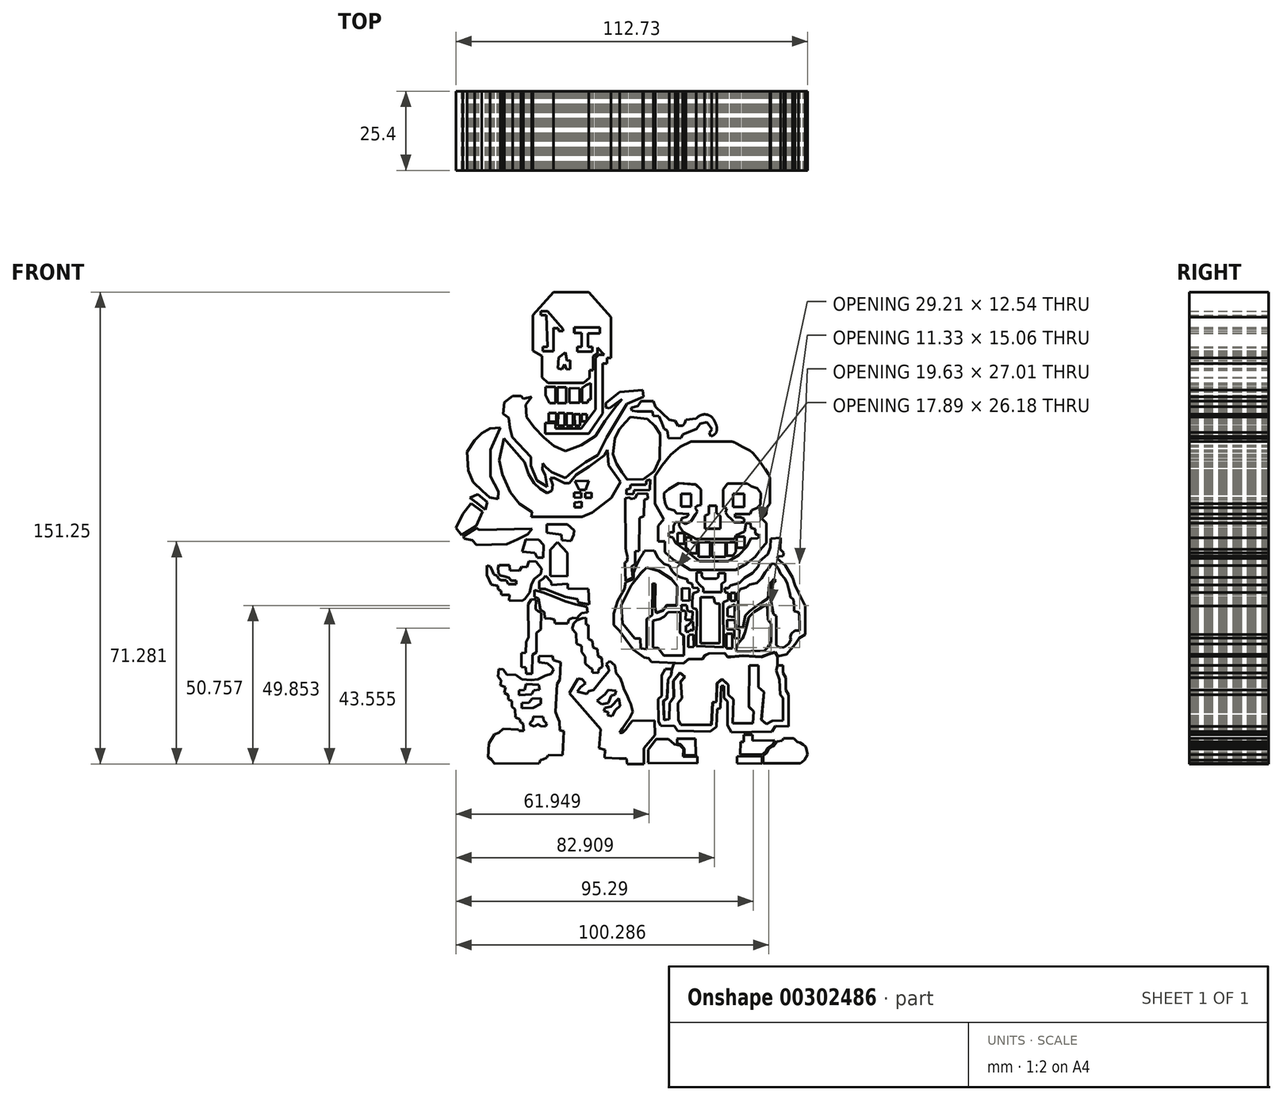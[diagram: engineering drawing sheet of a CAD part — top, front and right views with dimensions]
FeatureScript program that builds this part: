
annotation { "Feature Type Name" : "Feature", "Feature Type Description" : "" }
export const myFeature = defineFeature(function(context is Context, id is Id, definition is map)
    precondition{}
    {
        {
            var Q0;
            Q0=qCreatedBy(makeId("Front.planeOp"),FACE);
            var sketch = newSketch(context, id + "F0", { "sketchPlane" : qUnion([Q0])});
            skLineSegment(sketch, "E0", {"start": v(-16.69, 75) * mm, "end": v(-28, 75) * mm});
            skLineSegment(sketch, "E1", {"start": v(-28, 75) * mm, "end": v(-34.64, 67.58) * mm});
            skLineSegment(sketch, "E2", {"start": v(-34.64, 67.58) * mm, "end": v(-34.64, 56.21) * mm});
            skLineSegment(sketch, "E3", {"start": v(-34.64, 56.21) * mm, "end": v(-31.66, 54.56) * mm});
            skLineSegment(sketch, "E4", {"start": v(-31.66, 54.56) * mm, "end": v(-31.66, 47.68) * mm});
            skLineSegment(sketch, "E5", {"start": v(-31.66, 47.68) * mm, "end": v(-29.8, 45.82) * mm});
            skLineSegment(sketch, "E6", {"start": v(-29.8, 45.82) * mm, "end": v(-18.33, 45.82) * mm});
            skLineSegment(sketch, "E7", {"start": v(-18.33, 45.82) * mm, "end": v(-16.52, 47.56) * mm});
            skLineSegment(sketch, "E8", {"start": v(-16.52, 47.56) * mm, "end": v(-16.52, 49.98) * mm});
            skLineSegment(sketch, "E9", {"start": v(-16.52, 49.98) * mm, "end": v(-15.38, 49.98) * mm});
            skLineSegment(sketch, "E10", {"start": v(-15.38, 49.98) * mm, "end": v(-15.38, 54.44) * mm});
            skLineSegment(sketch, "E11", {"start": v(-15.38, 54.44) * mm, "end": v(-14.6, 54.44) * mm});
            skLineSegment(sketch, "E12", {"start": v(-14.6, 54.44) * mm, "end": v(-14.6, 37.31) * mm});
            skLineSegment(sketch, "E13", {"start": v(-14.6, 37.31) * mm, "end": v(-19.11, 31.33) * mm});
            skLineSegment(sketch, "E14", {"start": v(-19.11, 31.33) * mm, "end": v(-27.42, 31.33) * mm});
            skLineSegment(sketch, "E15", {"start": v(-27.42, 31.33) * mm, "end": v(-27.42, 32.99) * mm});
            skLineSegment(sketch, "E16", {"start": v(-27.42, 32.99) * mm, "end": v(-30.74, 32.99) * mm});
            skLineSegment(sketch, "E17", {"start": v(-30.74, 32.99) * mm, "end": v(-30.74, 29.66) * mm});
            skLineSegment(sketch, "E18", {"start": v(-30.74, 29.66) * mm, "end": v(-16.75, 29.66) * mm});
            skLineSegment(sketch, "E19", {"start": v(-16.75, 29.66) * mm, "end": v(-12.34, 36.12) * mm});
            skLineSegment(sketch, "E20", {"start": v(-12.34, 36.12) * mm, "end": v(-12.34, 52.15) * mm});
            skLineSegment(sketch, "E21", {"start": v(-12.34, 52.15) * mm, "end": v(-10.87, 52.15) * mm});
            skLineSegment(sketch, "E22", {"start": v(-10.87, 52.15) * mm, "end": v(-10.87, 53.88) * mm});
            skLineSegment(sketch, "E23", {"start": v(-10.87, 53.88) * mm, "end": v(-9.6, 53.88) * mm});
            skLineSegment(sketch, "E24", {"start": v(-9.6, 53.88) * mm, "end": v(-9.6, 66.91) * mm});
            skLineSegment(sketch, "E25", {"start": v(-9.6, 66.91) * mm, "end": v(-16.69, 75) * mm});
            skLineSegment(sketch, "E26", {"start": v(-29.94, 57.5) * mm, "end": v(-31.48, 57.5) * mm});
            skLineSegment(sketch, "E27", {"start": v(-31.48, 57.5) * mm, "end": v(-31.48, 56.06) * mm});
            skLineSegment(sketch, "E28", {"start": v(-31.48, 56.06) * mm, "end": v(-28.08, 56.06) * mm});
            skLineSegment(sketch, "E29", {"start": v(-28.08, 56.06) * mm, "end": v(-28.08, 63.46) * mm});
            skLineSegment(sketch, "E30", {"start": v(-28.08, 63.46) * mm, "end": v(-26.52, 63.46) * mm});
            skLineSegment(sketch, "E31", {"start": v(-26.52, 63.46) * mm, "end": v(-26.44, 62.47) * mm});
            skLineSegment(sketch, "E32", {"start": v(-26.44, 62.47) * mm, "end": v(-24.97, 62.47) * mm});
            skLineSegment(sketch, "E33", {"start": v(-24.97, 62.47) * mm, "end": v(-24.97, 63.1) * mm});
            skLineSegment(sketch, "E34", {"start": v(-24.97, 63.1) * mm, "end": v(-29.96, 68.9) * mm});
            skLineSegment(sketch, "E35", {"start": v(-29.96, 68.9) * mm, "end": v(-32.1, 68.9) * mm});
            skLineSegment(sketch, "E36", {"start": v(-32.1, 68.9) * mm, "end": v(-32.1, 67.6) * mm});
            skLineSegment(sketch, "E37", {"start": v(-32.1, 67.6) * mm, "end": v(-30.3, 67.6) * mm});
            skLineSegment(sketch, "E38", {"start": v(-30.3, 67.6) * mm, "end": v(-29.94, 57.5) * mm});
            skLineSegment(sketch, "E39", {"start": v(-21.37, 63.41) * mm, "end": v(-21.37, 61.88) * mm});
            skLineSegment(sketch, "E40", {"start": v(-21.37, 61.88) * mm, "end": v(-19.04, 61.88) * mm});
            skLineSegment(sketch, "E41", {"start": v(-19.04, 61.88) * mm, "end": v(-19.04, 57.4) * mm});
            skLineSegment(sketch, "E42", {"start": v(-19.04, 57.4) * mm, "end": v(-20.43, 57.4) * mm});
            skLineSegment(sketch, "E43", {"start": v(-20.43, 57.4) * mm, "end": v(-20.43, 55.93) * mm});
            skLineSegment(sketch, "E44", {"start": v(-20.43, 55.93) * mm, "end": v(-15.62, 55.93) * mm});
            skLineSegment(sketch, "E45", {"start": v(-15.62, 55.93) * mm, "end": v(-15.62, 57.47) * mm});
            skLineSegment(sketch, "E46", {"start": v(-15.62, 57.47) * mm, "end": v(-16.99, 57.47) * mm});
            skLineSegment(sketch, "E47", {"start": v(-16.99, 57.47) * mm, "end": v(-16.99, 61.76) * mm});
            skLineSegment(sketch, "E48", {"start": v(-16.99, 61.76) * mm, "end": v(-13.12, 61.76) * mm});
            skLineSegment(sketch, "E49", {"start": v(-13.12, 61.76) * mm, "end": v(-13.12, 63.61) * mm});
            skLineSegment(sketch, "E50", {"start": v(-13.12, 63.61) * mm, "end": v(-21.37, 63.61) * mm});
            skLineSegment(sketch, "E51", {"start": v(-21.37, 63.61) * mm, "end": v(-21.37, 63.41) * mm});
            skLineSegment(sketch, "E52", {"start": v(-24.17, 55.7) * mm, "end": v(-23.76, 52.96) * mm});
            skLineSegment(sketch, "E53", {"start": v(-23.76, 52.96) * mm, "end": v(-22.73, 53.11) * mm});
            skLineSegment(sketch, "E54", {"start": v(-22.73, 53.11) * mm, "end": v(-22.73, 50.35) * mm});
            skLineSegment(sketch, "E55", {"start": v(-22.73, 50.35) * mm, "end": v(-23.86, 50.22) * mm});
            skLineSegment(sketch, "E56", {"start": v(-23.86, 50.22) * mm, "end": v(-24.5, 51.88) * mm});
            skLineSegment(sketch, "E57", {"start": v(-24.5, 51.88) * mm, "end": v(-25.32, 50.18) * mm});
            skLineSegment(sketch, "E58", {"start": v(-25.32, 50.18) * mm, "end": v(-26.67, 50.56) * mm});
            skLineSegment(sketch, "E59", {"start": v(-26.67, 50.56) * mm, "end": v(-26.33, 54.04) * mm});
            skLineSegment(sketch, "E60", {"start": v(-26.33, 54.04) * mm, "end": v(-24.17, 55.7) * mm});
            skLineSegment(sketch, "E61", {"start": v(-13.91, 57.13) * mm, "end": v(-13.91, 54.9) * mm});
            skLineSegment(sketch, "E62", {"start": v(-13.91, 54.9) * mm, "end": v(-11.83, 54.86) * mm});
            skLineSegment(sketch, "E63", {"start": v(-11.83, 54.86) * mm, "end": v(-13.91, 57.13) * mm});
            skLineSegment(sketch, "E64", {"start": v(-15.38, 54.44) * mm, "end": v(-13.91, 55.31) * mm});
            skLineSegment(sketch, "E65", {"start": v(-13.91, 55.31) * mm, "end": v(-13.91, 54.9) * mm});
            skLineSegment(sketch, "E66", {"start": v(-14.6, 53.9) * mm, "end": v(-13.52, 54.89) * mm});
            skLineSegment(sketch, "E67", {"start": v(-13.52, 54.89) * mm, "end": v(-13.91, 54.9) * mm});
            skLineSegment(sketch, "E68", {"start": v(-30.64, 44.3) * mm, "end": v(-30.64, 41.9) * mm});
            skLineSegment(sketch, "E69", {"start": v(-30.64, 41.9) * mm, "end": v(-29.36, 39.43) * mm});
            skLineSegment(sketch, "E70", {"start": v(-29.36, 39.43) * mm, "end": v(-27.4, 39.43) * mm});
            skLineSegment(sketch, "E71", {"start": v(-27.4, 39.43) * mm, "end": v(-27.4, 44.55) * mm});
            skLineSegment(sketch, "E72", {"start": v(-27.4, 44.55) * mm, "end": v(-30.64, 44.55) * mm});
            skLineSegment(sketch, "E73", {"start": v(-30.64, 44.55) * mm, "end": v(-30.64, 44.3) * mm});
            skLineSegment(sketch, "E74", {"start": v(-26.73, 44.47) * mm, "end": v(-26.73, 39.36) * mm});
            skLineSegment(sketch, "E75", {"start": v(-26.73, 39.36) * mm, "end": v(-23.91, 39.36) * mm});
            skLineSegment(sketch, "E76", {"start": v(-23.91, 39.36) * mm, "end": v(-23.91, 44.44) * mm});
            skLineSegment(sketch, "E77", {"start": v(-23.91, 44.44) * mm, "end": v(-26.73, 44.47) * mm});
            skLineSegment(sketch, "E78", {"start": v(-22.96, 44.18) * mm, "end": v(-22.96, 39.55) * mm});
            skLineSegment(sketch, "E79", {"start": v(-22.96, 39.55) * mm, "end": v(-19.7, 39.55) * mm});
            skLineSegment(sketch, "E80", {"start": v(-19.7, 39.55) * mm, "end": v(-19.7, 44.15) * mm});
            skLineSegment(sketch, "E81", {"start": v(-19.7, 44.15) * mm, "end": v(-22.96, 44.18) * mm});
            skLineSegment(sketch, "E82", {"start": v(-18.87, 44.28) * mm, "end": v(-18.87, 39.55) * mm});
            skLineSegment(sketch, "E83", {"start": v(-18.87, 39.55) * mm, "end": v(-17.17, 39.55) * mm});
            skLineSegment(sketch, "E84", {"start": v(-17.17, 39.55) * mm, "end": v(-16.82, 40.54) * mm});
            skLineSegment(sketch, "E85", {"start": v(-16.82, 40.54) * mm, "end": v(-16.15, 40.54) * mm});
            skLineSegment(sketch, "E86", {"start": v(-16.15, 40.54) * mm, "end": v(-16.15, 45.78) * mm});
            skLineSegment(sketch, "E87", {"start": v(-16.15, 45.78) * mm, "end": v(-17.5, 45.27) * mm});
            skLineSegment(sketch, "E88", {"start": v(-17.5, 45.27) * mm, "end": v(-18.87, 44.28) * mm});
            skLineSegment(sketch, "E89", {"start": v(-29.52, 33.48) * mm, "end": v(-29.52, 36.2) * mm});
            skLineSegment(sketch, "E90", {"start": v(-29.52, 36.2) * mm, "end": v(-27.18, 36.2) * mm});
            skLineSegment(sketch, "E91", {"start": v(-27.18, 36.2) * mm, "end": v(-27.18, 33.48) * mm});
            skLineSegment(sketch, "E92", {"start": v(-27.18, 33.48) * mm, "end": v(-29.52, 33.48) * mm});
            skLineSegment(sketch, "E93", {"start": v(-26.62, 32.2) * mm, "end": v(-24.53, 32.2) * mm});
            skLineSegment(sketch, "E94", {"start": v(-24.53, 32.2) * mm, "end": v(-24.53, 36.2) * mm});
            skLineSegment(sketch, "E95", {"start": v(-24.53, 36.2) * mm, "end": v(-26.54, 36.2) * mm});
            skLineSegment(sketch, "E96", {"start": v(-26.54, 36.2) * mm, "end": v(-26.62, 32.2) * mm});
            skLineSegment(sketch, "E97", {"start": v(-23.9, 32.2) * mm, "end": v(-21.85, 32.2) * mm});
            skLineSegment(sketch, "E98", {"start": v(-21.85, 32.2) * mm, "end": v(-21.85, 36.03) * mm});
            skLineSegment(sketch, "E99", {"start": v(-21.85, 36.03) * mm, "end": v(-23.85, 36.03) * mm});
            skLineSegment(sketch, "E100", {"start": v(-23.85, 36.03) * mm, "end": v(-23.9, 32.2) * mm});
            skLineSegment(sketch, "E101", {"start": v(-21.17, 32.15) * mm, "end": v(-19.55, 32.15) * mm});
            skLineSegment(sketch, "E102", {"start": v(-19.55, 32.15) * mm, "end": v(-19.55, 35.86) * mm});
            skLineSegment(sketch, "E103", {"start": v(-19.55, 35.86) * mm, "end": v(-21.25, 35.86) * mm});
            skLineSegment(sketch, "E104", {"start": v(-21.25, 35.86) * mm, "end": v(-21.17, 32.15) * mm});
            skLineSegment(sketch, "E105", {"start": v(-19.03, 35.57) * mm, "end": v(-19.03, 33.6) * mm});
            skLineSegment(sketch, "E106", {"start": v(-19.03, 33.6) * mm, "end": v(-17.4, 33.6) * mm});
            skLineSegment(sketch, "E107", {"start": v(-17.4, 33.6) * mm, "end": v(-17.4, 35.86) * mm});
            skLineSegment(sketch, "E108", {"start": v(-17.4, 35.86) * mm, "end": v(-19.03, 35.86) * mm});
            skLineSegment(sketch, "E109", {"start": v(-19.03, 35.86) * mm, "end": v(-19.03, 35.57) * mm});
            skLineSegment(sketch, "E110", {"start": v(-35.03, 41.37) * mm, "end": v(-36.94, 38.85) * mm});
            skLineSegment(sketch, "E111", {"start": v(-36.94, 38.85) * mm, "end": v(-36.63, 34.91) * mm});
            skLineSegment(sketch, "E112", {"start": v(-36.63, 34.91) * mm, "end": v(-34.2, 31.65) * mm});
            skLineSegment(sketch, "E113", {"start": v(-34.2, 31.65) * mm, "end": v(-31.08, 28.3) * mm});
            skLineSegment(sketch, "E114", {"start": v(-31.08, 28.3) * mm, "end": v(-27.97, 25.64) * mm});
            skLineSegment(sketch, "E115", {"start": v(-27.97, 25.64) * mm, "end": v(-24.17, 24.05) * mm});
            skLineSegment(sketch, "E116", {"start": v(-24.17, 24.05) * mm, "end": v(-19.15, 25.87) * mm});
            skLineSegment(sketch, "E117", {"start": v(-19.15, 25.87) * mm, "end": v(-14.52, 28.83) * mm});
            skLineSegment(sketch, "E118", {"start": v(-14.52, 28.83) * mm, "end": v(-11.48, 33.7) * mm});
            skLineSegment(sketch, "E119", {"start": v(-11.48, 33.7) * mm, "end": v(-7.76, 38.71) * mm});
            skLineSegment(sketch, "E120", {"start": v(-7.76, 38.71) * mm, "end": v(-6.09, 40.61) * mm});
            skLineSegment(sketch, "E121", {"start": v(-6.09, 40.61) * mm, "end": v(-10.11, 37.72) * mm});
            skLineSegment(sketch, "E122", {"start": v(-10.11, 37.72) * mm, "end": v(-11.33, 38.03) * mm});
            skLineSegment(sketch, "E123", {"start": v(-11.33, 38.03) * mm, "end": v(-11.33, 39.4) * mm});
            skLineSegment(sketch, "E124", {"start": v(-11.33, 39.4) * mm, "end": v(-6.85, 42.97) * mm});
            skLineSegment(sketch, "E125", {"start": v(-6.85, 42.97) * mm, "end": v(0.6, 43.57) * mm});
            skLineSegment(sketch, "E126", {"start": v(0.6, 43.57) * mm, "end": v(0.77, 41.46) * mm});
            skLineSegment(sketch, "E127", {"start": v(0.77, 41.46) * mm, "end": v(-4.5, 39.1) * mm});
            skLineSegment(sketch, "E128", {"start": v(-4.5, 39.1) * mm, "end": v(-10.96, 28.4) * mm});
            skLineSegment(sketch, "E129", {"start": v(-10.96, 28.4) * mm, "end": v(-13.86, 22.7) * mm});
            skLineSegment(sketch, "E130", {"start": v(-13.86, 22.7) * mm, "end": v(-17.73, 20.45) * mm});
            skLineSegment(sketch, "E131", {"start": v(-17.73, 20.45) * mm, "end": v(-21.97, 17.44) * mm});
            skLineSegment(sketch, "E132", {"start": v(-21.97, 17.44) * mm, "end": v(-24.18, 15.4) * mm});
            skLineSegment(sketch, "E133", {"start": v(-24.18, 15.4) * mm, "end": v(-28.69, 17.33) * mm});
            skLineSegment(sketch, "E134", {"start": v(-28.69, 17.33) * mm, "end": v(-30.62, 18.95) * mm});
            skLineSegment(sketch, "E135", {"start": v(-30.62, 18.95) * mm, "end": v(-31.43, 20.08) * mm});
            skLineSegment(sketch, "E136", {"start": v(-31.43, 20.08) * mm, "end": v(-31.55, 18.1) * mm});
            skLineSegment(sketch, "E137", {"start": v(-31.55, 18.1) * mm, "end": v(-30.65, 16.38) * mm});
            skLineSegment(sketch, "E138", {"start": v(-30.65, 16.38) * mm, "end": v(-30.1, 12.59) * mm});
            skLineSegment(sketch, "E139", {"start": v(-30.1, 12.59) * mm, "end": v(-33.36, 14.66) * mm});
            skLineSegment(sketch, "E140", {"start": v(-33.36, 14.66) * mm, "end": v(-35.26, 19.36) * mm});
            skLineSegment(sketch, "E141", {"start": v(-35.26, 19.36) * mm, "end": v(-35.26, 22.16) * mm});
            skLineSegment(sketch, "E142", {"start": v(-35.26, 22.16) * mm, "end": v(-41.3, 28.49) * mm});
            skLineSegment(sketch, "E143", {"start": v(-41.3, 28.49) * mm, "end": v(-42.03, 31.47) * mm});
            skLineSegment(sketch, "E144", {"start": v(-42.03, 31.47) * mm, "end": v(-42.4, 34.72) * mm});
            skLineSegment(sketch, "E145", {"start": v(-42.4, 34.72) * mm, "end": v(-44.2, 35.99) * mm});
            skLineSegment(sketch, "E146", {"start": v(-44.2, 35.99) * mm, "end": v(-43.75, 39.6) * mm});
            skLineSegment(sketch, "E147", {"start": v(-43.75, 39.6) * mm, "end": v(-41.13, 41.68) * mm});
            skLineSegment(sketch, "E148", {"start": v(-41.13, 41.68) * mm, "end": v(-38.42, 41.68) * mm});
            skLineSegment(sketch, "E149", {"start": v(-38.42, 41.68) * mm, "end": v(-37.7, 40.78) * mm});
            skLineSegment(sketch, "E150", {"start": v(-37.7, 40.78) * mm, "end": v(-35.03, 41.37) * mm});
            skLineSegment(sketch, "E151", {"start": v(-3.09, 37.93) * mm, "end": v(-0.94, 38.5) * mm});
            skLineSegment(sketch, "E152", {"start": v(-0.94, 38.5) * mm, "end": v(0, 40.09) * mm});
            skLineSegment(sketch, "E153", {"start": v(0, 40.09) * mm, "end": v(3.94, 40.09) * mm});
            skLineSegment(sketch, "E154", {"start": v(3.94, 40.09) * mm, "end": v(4.66, 38.3) * mm});
            skLineSegment(sketch, "E155", {"start": v(4.66, 38.3) * mm, "end": v(9.1, 34.06) * mm});
            skLineSegment(sketch, "E156", {"start": v(9.1, 34.06) * mm, "end": v(10.9, 33.7) * mm});
            skLineSegment(sketch, "E157", {"start": v(10.9, 33.7) * mm, "end": v(11.83, 32.13) * mm});
            skLineSegment(sketch, "E158", {"start": v(11.83, 32.13) * mm, "end": v(13.4, 32.2) * mm});
            skLineSegment(sketch, "E159", {"start": v(13.4, 32.2) * mm, "end": v(13.98, 32.91) * mm});
            skLineSegment(sketch, "E160", {"start": v(13.98, 32.91) * mm, "end": v(14.4, 34.06) * mm});
            skLineSegment(sketch, "E161", {"start": v(14.4, 34.06) * mm, "end": v(17.64, 34.42) * mm});
            skLineSegment(sketch, "E162", {"start": v(17.64, 34.42) * mm, "end": v(18.5, 35.78) * mm});
            skLineSegment(sketch, "E163", {"start": v(18.5, 35.78) * mm, "end": v(21.72, 35.78) * mm});
            skLineSegment(sketch, "E164", {"start": v(21.72, 35.78) * mm, "end": v(23.09, 34.56) * mm});
            skLineSegment(sketch, "E165", {"start": v(23.09, 34.56) * mm, "end": v(24.02, 32.63) * mm});
            skLineSegment(sketch, "E166", {"start": v(24.02, 32.63) * mm, "end": v(24.6, 30.76) * mm});
            skLineSegment(sketch, "E167", {"start": v(24.6, 30.76) * mm, "end": v(23.66, 29.04) * mm});
            skLineSegment(sketch, "E168", {"start": v(23.66, 29.04) * mm, "end": v(22.44, 28.76) * mm});
            skLineSegment(sketch, "E169", {"start": v(22.44, 28.76) * mm, "end": v(21.87, 29.83) * mm});
            skLineSegment(sketch, "E170", {"start": v(21.87, 29.83) * mm, "end": v(22.73, 31.05) * mm});
            skLineSegment(sketch, "E171", {"start": v(22.73, 31.05) * mm, "end": v(21.15, 33.34) * mm});
            skLineSegment(sketch, "E172", {"start": v(21.15, 33.34) * mm, "end": v(19, 32.77) * mm});
            skLineSegment(sketch, "E173", {"start": v(19, 32.77) * mm, "end": v(17.78, 31.2) * mm});
            skLineSegment(sketch, "E174", {"start": v(17.78, 31.2) * mm, "end": v(15.05, 30.05) * mm});
            skLineSegment(sketch, "E175", {"start": v(15.05, 30.05) * mm, "end": v(13.4, 29.33) * mm});
            skLineSegment(sketch, "E176", {"start": v(13.4, 29.33) * mm, "end": v(12.83, 28.25) * mm});
            skLineSegment(sketch, "E177", {"start": v(12.83, 28.25) * mm, "end": v(8.81, 28.04) * mm});
            skLineSegment(sketch, "E178", {"start": v(8.81, 28.04) * mm, "end": v(8.38, 30.62) * mm});
            skLineSegment(sketch, "E179", {"start": v(8.38, 30.62) * mm, "end": v(7.38, 31.2) * mm});
            skLineSegment(sketch, "E180", {"start": v(7.38, 31.2) * mm, "end": v(6.66, 33.2) * mm});
            skLineSegment(sketch, "E181", {"start": v(6.66, 33.2) * mm, "end": v(5.8, 35.2) * mm});
            skLineSegment(sketch, "E182", {"start": v(5.8, 35.2) * mm, "end": v(3.87, 35.35) * mm});
            skLineSegment(sketch, "E183", {"start": v(3.87, 35.35) * mm, "end": v(3.72, 36.79) * mm});
            skLineSegment(sketch, "E184", {"start": v(3.72, 36.79) * mm, "end": v(-1.22, 36.79) * mm});
            skLineSegment(sketch, "E185", {"start": v(-1.22, 36.79) * mm, "end": v(-2.95, 36.93) * mm});
            skLineSegment(sketch, "E186", {"start": v(-2.95, 36.93) * mm, "end": v(-3.16, 37.8) * mm});
            skLineSegment(sketch, "E187", {"start": v(-3.16, 37.8) * mm, "end": v(-3.09, 37.93) * mm});
            skLineSegment(sketch, "E188", {"start": v(-3.09, 35.2) * mm, "end": v(-5.01, 33.2) * mm});
            skLineSegment(sketch, "E189", {"start": v(-5.01, 33.2) * mm, "end": v(-6.77, 31.12) * mm});
            skLineSegment(sketch, "E190", {"start": v(-6.77, 31.12) * mm, "end": v(-8.4, 28.28) * mm});
            skLineSegment(sketch, "E191", {"start": v(-8.4, 28.28) * mm, "end": v(-8.94, 23) * mm});
            skLineSegment(sketch, "E192", {"start": v(-8.94, 23) * mm, "end": v(-7.85, 20.02) * mm});
            skLineSegment(sketch, "E193", {"start": v(-7.85, 20.02) * mm, "end": v(-6.1, 17.1) * mm});
            skLineSegment(sketch, "E194", {"start": v(-6.1, 17.1) * mm, "end": v(-4.47, 14.87) * mm});
            skLineSegment(sketch, "E195", {"start": v(-4.47, 14.87) * mm, "end": v(0.81, 15.01) * mm});
            skLineSegment(sketch, "E196", {"start": v(0.81, 15.01) * mm, "end": v(4.2, 17.58) * mm});
            skLineSegment(sketch, "E197", {"start": v(4.2, 17.58) * mm, "end": v(5.95, 21.5) * mm});
            skLineSegment(sketch, "E198", {"start": v(5.95, 21.5) * mm, "end": v(6.1, 29.43) * mm});
            skLineSegment(sketch, "E199", {"start": v(6.1, 29.43) * mm, "end": v(4.53, 32.07) * mm});
            skLineSegment(sketch, "E200", {"start": v(4.53, 32.07) * mm, "end": v(2.03, 34.37) * mm});
            skLineSegment(sketch, "E201", {"start": v(2.03, 34.37) * mm, "end": v(-3.38, 34.9) * mm});
            skLineSegment(sketch, "E202", {"start": v(-3.38, 34.9) * mm, "end": v(-5.01, 33.2) * mm});
            skLineSegment(sketch, "E203", {"start": v(-43.86, 28.08) * mm, "end": v(-37.36, 20.49) * mm});
            skLineSegment(sketch, "E204", {"start": v(-37.36, 20.49) * mm, "end": v(-36.1, 16.7) * mm});
            skLineSegment(sketch, "E205", {"start": v(-36.1, 16.7) * mm, "end": v(-34.29, 13.8) * mm});
            skLineSegment(sketch, "E206", {"start": v(-34.29, 13.8) * mm, "end": v(-32.3, 12) * mm});
            skLineSegment(sketch, "E207", {"start": v(-32.3, 12) * mm, "end": v(-30.13, 10.55) * mm});
            skLineSegment(sketch, "E208", {"start": v(-30.13, 10.55) * mm, "end": v(-28.6, 11.27) * mm});
            skLineSegment(sketch, "E209", {"start": v(-28.6, 11.27) * mm, "end": v(-28.32, 13.26) * mm});
            skLineSegment(sketch, "E210", {"start": v(-28.32, 13.26) * mm, "end": v(-29.05, 15.34) * mm});
            skLineSegment(sketch, "E211", {"start": v(-29.05, 15.34) * mm, "end": v(-27.78, 15.34) * mm});
            skLineSegment(sketch, "E212", {"start": v(-27.78, 15.34) * mm, "end": v(-24.53, 13.7) * mm});
            skLineSegment(sketch, "E213", {"start": v(-24.53, 13.7) * mm, "end": v(-23, 13.7) * mm});
            skLineSegment(sketch, "E214", {"start": v(-23, 13.7) * mm, "end": v(-20.82, 16.42) * mm});
            skLineSegment(sketch, "E215", {"start": v(-20.82, 16.42) * mm, "end": v(-16.67, 19.13) * mm});
            skLineSegment(sketch, "E216", {"start": v(-16.67, 19.13) * mm, "end": v(-11.79, 22.65) * mm});
            skLineSegment(sketch, "E217", {"start": v(-11.79, 22.65) * mm, "end": v(-10.8, 24.37) * mm});
            skLineSegment(sketch, "E218", {"start": v(-10.8, 24.37) * mm, "end": v(-10.43, 19.4) * mm});
            skLineSegment(sketch, "E219", {"start": v(-10.43, 19.4) * mm, "end": v(-6.55, 14.16) * mm});
            skLineSegment(sketch, "E220", {"start": v(-6.55, 14.16) * mm, "end": v(-9.53, 9.1) * mm});
            skLineSegment(sketch, "E221", {"start": v(-9.53, 9.1) * mm, "end": v(-15.65, 4.36) * mm});
            skLineSegment(sketch, "E222", {"start": v(-15.65, 4.36) * mm, "end": v(-18.9, 2.9) * mm});
            skLineSegment(sketch, "E223", {"start": v(-18.9, 2.9) * mm, "end": v(-35.1, 2.9) * mm});
            skLineSegment(sketch, "E224", {"start": v(-35.1, 2.9) * mm, "end": v(-34.92, 4.53) * mm});
            skLineSegment(sketch, "E225", {"start": v(-34.92, 4.53) * mm, "end": v(-39.02, 7.09) * mm});
            skLineSegment(sketch, "E226", {"start": v(-39.02, 7.09) * mm, "end": v(-41.92, 10.84) * mm});
            skLineSegment(sketch, "E227", {"start": v(-41.92, 10.84) * mm, "end": v(-44.47, 16.55) * mm});
            skLineSegment(sketch, "E228", {"start": v(-44.47, 16.55) * mm, "end": v(-45.5, 21.07) * mm});
            skLineSegment(sketch, "E229", {"start": v(-45.5, 21.07) * mm, "end": v(-43.86, 28.08) * mm});
            skLineSegment(sketch, "E230", {"start": v(-20.94, 13.9) * mm, "end": v(-19.74, 11.6) * mm});
            skLineSegment(sketch, "E231", {"start": v(-19.74, 11.6) * mm, "end": v(-17.78, 11.6) * mm});
            skLineSegment(sketch, "E232", {"start": v(-17.78, 11.6) * mm, "end": v(-16.67, 14.5) * mm});
            skLineSegment(sketch, "E233", {"start": v(-16.67, 14.5) * mm, "end": v(-21.2, 14.42) * mm});
            skLineSegment(sketch, "E234", {"start": v(-21.2, 14.42) * mm, "end": v(-20.94, 13.9) * mm});
            skLineSegment(sketch, "E235", {"start": v(-21.4, 10.65) * mm, "end": v(-21.4, 9.15) * mm});
            skLineSegment(sketch, "E236", {"start": v(-21.4, 9.15) * mm, "end": v(-19.16, 9) * mm});
            skLineSegment(sketch, "E237", {"start": v(-19.16, 9) * mm, "end": v(-19.16, 10.65) * mm});
            skLineSegment(sketch, "E238", {"start": v(-19.16, 10.65) * mm, "end": v(-21.4, 10.65) * mm});
            skLineSegment(sketch, "E239", {"start": v(-17.82, 10.59) * mm, "end": v(-17.82, 9.05) * mm});
            skLineSegment(sketch, "E240", {"start": v(-17.82, 9.05) * mm, "end": v(-15.9, 9.05) * mm});
            skLineSegment(sketch, "E241", {"start": v(-15.9, 9.05) * mm, "end": v(-15.9, 10.65) * mm});
            skLineSegment(sketch, "E242", {"start": v(-15.9, 10.65) * mm, "end": v(-17.82, 10.59) * mm});
            skLineSegment(sketch, "E243", {"start": v(-21.27, 7.52) * mm, "end": v(-21.27, 5.96) * mm});
            skLineSegment(sketch, "E244", {"start": v(-21.27, 5.96) * mm, "end": v(-18.97, 5.96) * mm});
            skLineSegment(sketch, "E245", {"start": v(-18.97, 5.96) * mm, "end": v(-18.97, 7.71) * mm});
            skLineSegment(sketch, "E246", {"start": v(-18.97, 7.71) * mm, "end": v(-21.27, 7.52) * mm});
            skLineSegment(sketch, "E247", {"start": v(-45.15, 31.32) * mm, "end": v(-48.21, 24.4) * mm});
            skLineSegment(sketch, "E248", {"start": v(-48.21, 24.4) * mm, "end": v(-48.21, 15.87) * mm});
            skLineSegment(sketch, "E249", {"start": v(-48.21, 15.87) * mm, "end": v(-45.64, 11.04) * mm});
            skLineSegment(sketch, "E250", {"start": v(-45.64, 11.04) * mm, "end": v(-45.8, 8.63) * mm});
            skLineSegment(sketch, "E251", {"start": v(-45.8, 8.63) * mm, "end": v(-48.53, 9.1) * mm});
            skLineSegment(sketch, "E252", {"start": v(-48.53, 9.1) * mm, "end": v(-50.79, 11.2) * mm});
            skLineSegment(sketch, "E253", {"start": v(-50.79, 11.2) * mm, "end": v(-53.85, 14.1) * mm});
            skLineSegment(sketch, "E254", {"start": v(-53.85, 14.1) * mm, "end": v(-55.38, 17.8) * mm});
            skLineSegment(sketch, "E255", {"start": v(-55.38, 17.8) * mm, "end": v(-55.7, 23.76) * mm});
            skLineSegment(sketch, "E256", {"start": v(-55.7, 23.76) * mm, "end": v(-53.35, 27.5) * mm});
            skLineSegment(sketch, "E257", {"start": v(-53.35, 27.5) * mm, "end": v(-50.97, 29.74) * mm});
            skLineSegment(sketch, "E258", {"start": v(-50.97, 29.74) * mm, "end": v(-48.4, 31.3) * mm});
            skLineSegment(sketch, "E259", {"start": v(-48.4, 31.3) * mm, "end": v(-45, 31.49) * mm});
            skLineSegment(sketch, "E260", {"start": v(-45, 31.49) * mm, "end": v(-45.15, 31.32) * mm});
            skLineSegment(sketch, "E261", {"start": v(-54.84, 9.08) * mm, "end": v(-52.57, 7.43) * mm});
            skLineSegment(sketch, "E262", {"start": v(-52.57, 7.43) * mm, "end": v(-49.9, 5.21) * mm});
            skLineSegment(sketch, "E263", {"start": v(-49.9, 5.21) * mm, "end": v(-49.27, 7.6) * mm});
            skLineSegment(sketch, "E264", {"start": v(-49.27, 7.6) * mm, "end": v(-52.34, 10.17) * mm});
            skLineSegment(sketch, "E265", {"start": v(-52.34, 10.17) * mm, "end": v(-54.84, 9.08) * mm});
            skLineSegment(sketch, "E266", {"start": v(-54.44, 7.23) * mm, "end": v(-50.8, 4.6) * mm});
            skLineSegment(sketch, "E267", {"start": v(-50.8, 4.6) * mm, "end": v(-52.83, 0) * mm});
            skLineSegment(sketch, "E268", {"start": v(-52.83, 0) * mm, "end": v(-57.45, -2.87) * mm});
            skLineSegment(sketch, "E269", {"start": v(-57.45, -2.87) * mm, "end": v(-59.33, -0.67) * mm});
            skLineSegment(sketch, "E270", {"start": v(-59.33, -0.67) * mm, "end": v(-57.13, 3.8) * mm});
            skLineSegment(sketch, "E271", {"start": v(-57.13, 3.8) * mm, "end": v(-54.44, 7.23) * mm});
            skLineSegment(sketch, "E272", {"start": v(-56.92, -3.3) * mm, "end": v(-52.62, -0.61) * mm});
            skLineSegment(sketch, "E273", {"start": v(-52.62, -0.61) * mm, "end": v(-51.87, -1.26) * mm});
            skLineSegment(sketch, "E274", {"start": v(-51.87, -1.26) * mm, "end": v(-34.89, -0.83) * mm});
            skLineSegment(sketch, "E275", {"start": v(-34.89, -0.83) * mm, "end": v(-36.23, -2.66) * mm});
            skLineSegment(sketch, "E276", {"start": v(-36.23, -2.66) * mm, "end": v(-39.56, -4.27) * mm});
            skLineSegment(sketch, "E277", {"start": v(-39.56, -4.27) * mm, "end": v(-43.05, -5.88) * mm});
            skLineSegment(sketch, "E278", {"start": v(-43.05, -5.88) * mm, "end": v(-52.62, -6.1) * mm});
            skLineSegment(sketch, "E279", {"start": v(-52.62, -6.1) * mm, "end": v(-54.07, -4.48) * mm});
            skLineSegment(sketch, "E280", {"start": v(-54.07, -4.48) * mm, "end": v(-56.65, -4.05) * mm});
            skLineSegment(sketch, "E281", {"start": v(-56.65, -4.05) * mm, "end": v(-56.92, -3.3) * mm});
            skLineSegment(sketch, "E282", {"start": v(-36.96, -4.31) * mm, "end": v(-38, -8.25) * mm});
            skLineSegment(sketch, "E283", {"start": v(-38, -8.25) * mm, "end": v(-33.98, -8.58) * mm});
            skLineSegment(sketch, "E284", {"start": v(-33.98, -8.58) * mm, "end": v(-33.26, -10.19) * mm});
            skLineSegment(sketch, "E285", {"start": v(-33.26, -10.19) * mm, "end": v(-31.33, -10.19) * mm});
            skLineSegment(sketch, "E286", {"start": v(-31.33, -10.19) * mm, "end": v(-31.25, -6.08) * mm});
            skLineSegment(sketch, "E287", {"start": v(-31.25, -6.08) * mm, "end": v(-32.7, -4.47) * mm});
            skLineSegment(sketch, "E288", {"start": v(-32.7, -4.47) * mm, "end": v(-36.8, -4.31) * mm});
            skLineSegment(sketch, "E289", {"start": v(-36.8, -4.31) * mm, "end": v(-36.96, -4.31) * mm});
            skLineSegment(sketch, "E290", {"start": v(-30.2, 0.54) * mm, "end": v(-30.2, -2.15) * mm});
            skLineSegment(sketch, "E291", {"start": v(-30.2, -2.15) * mm, "end": v(-25.53, -2.8) * mm});
            skLineSegment(sketch, "E292", {"start": v(-25.53, -2.8) * mm, "end": v(-25.38, -4.58) * mm});
            skLineSegment(sketch, "E293", {"start": v(-25.38, -4.58) * mm, "end": v(-22.49, -4.79) * mm});
            skLineSegment(sketch, "E294", {"start": v(-22.49, -4.79) * mm, "end": v(-21.52, -2.76) * mm});
            skLineSegment(sketch, "E295", {"start": v(-21.52, -2.76) * mm, "end": v(-21.37, -1.39) * mm});
            skLineSegment(sketch, "E296", {"start": v(-21.37, -1.39) * mm, "end": v(-23.6, 0.49) * mm});
            skLineSegment(sketch, "E297", {"start": v(-23.6, 0.49) * mm, "end": v(-30.2, 0.54) * mm});
            skLineSegment(sketch, "E298", {"start": v(-29, -7.43) * mm, "end": v(-29, -15.95) * mm});
            skLineSegment(sketch, "E299", {"start": v(-29, -15.95) * mm, "end": v(-23.65, -16.05) * mm});
            skLineSegment(sketch, "E300", {"start": v(-23.65, -16.05) * mm, "end": v(-23.55, -8.58) * mm});
            skLineSegment(sketch, "E301", {"start": v(-23.55, -8.58) * mm, "end": v(-26.71, -5.23) * mm});
            skLineSegment(sketch, "E302", {"start": v(-26.71, -5.23) * mm, "end": v(-28.91, -7.43) * mm});
            skLineSegment(sketch, "E303", {"start": v(-28.91, -7.43) * mm, "end": v(-29, -7.43) * mm});
            skLineSegment(sketch, "E304", {"start": v(-44.86, -17.4) * mm, "end": v(-43.1, -17.4) * mm});
            skLineSegment(sketch, "E305", {"start": v(-43.1, -17.4) * mm, "end": v(-42.56, -18.68) * mm});
            skLineSegment(sketch, "E306", {"start": v(-42.56, -18.68) * mm, "end": v(-39.92, -18.61) * mm});
            skLineSegment(sketch, "E307", {"start": v(-39.92, -18.61) * mm, "end": v(-39.98, -17.53) * mm});
            skLineSegment(sketch, "E308", {"start": v(-39.98, -17.53) * mm, "end": v(-41.6, -17.46) * mm});
            skLineSegment(sketch, "E309", {"start": v(-41.6, -17.46) * mm, "end": v(-42.28, -16.58) * mm});
            skLineSegment(sketch, "E310", {"start": v(-42.28, -16.58) * mm, "end": v(-43.37, -16.18) * mm});
            skLineSegment(sketch, "E311", {"start": v(-43.37, -16.18) * mm, "end": v(-45, -15.9) * mm});
            skLineSegment(sketch, "E312", {"start": v(-45.4, -12.59) * mm, "end": v(-42.08, -12.59) * mm});
            skLineSegment(sketch, "E313", {"start": v(-42.08, -12.59) * mm, "end": v(-42.01, -14.21) * mm});
            skLineSegment(sketch, "E314", {"start": v(-42.01, -14.21) * mm, "end": v(-38.9, -14.35) * mm});
            skLineSegment(sketch, "E315", {"start": v(-38.9, -14.35) * mm, "end": v(-38.16, -13.06) * mm});
            skLineSegment(sketch, "E316", {"start": v(-38.16, -13.06) * mm, "end": v(-36.53, -13.13) * mm});
            skLineSegment(sketch, "E317", {"start": v(-36.53, -13.13) * mm, "end": v(-35.92, -11.3) * mm});
            skLineSegment(sketch, "E318", {"start": v(-35.92, -11.3) * mm, "end": v(-33.62, -11.37) * mm});
            skLineSegment(sketch, "E319", {"start": v(-33.62, -11.37) * mm, "end": v(-31.86, -13.67) * mm});
            skLineSegment(sketch, "E320", {"start": v(-31.86, -13.67) * mm, "end": v(-32.13, -15.3) * mm});
            skLineSegment(sketch, "E321", {"start": v(-32.13, -15.3) * mm, "end": v(-34.3, -16.99) * mm});
            skLineSegment(sketch, "E322", {"start": v(-34.3, -16.99) * mm, "end": v(-35.1, -18.95) * mm});
            skLineSegment(sketch, "E323", {"start": v(-35.1, -18.95) * mm, "end": v(-35.72, -21.25) * mm});
            skLineSegment(sketch, "E324", {"start": v(-35.72, -21.25) * mm, "end": v(-37.2, -23.28) * mm});
            skLineSegment(sketch, "E325", {"start": v(-37.2, -23.28) * mm, "end": v(-38.09, -24.03) * mm});
            skLineSegment(sketch, "E326", {"start": v(-38.09, -24.03) * mm, "end": v(-42.28, -23.82) * mm});
            skLineSegment(sketch, "E327", {"start": v(-42.28, -23.82) * mm, "end": v(-42.15, -22.06) * mm});
            skLineSegment(sketch, "E328", {"start": v(-42.15, -22.06) * mm, "end": v(-44.65, -22.06) * mm});
            skLineSegment(sketch, "E329", {"start": v(-44.65, -22.06) * mm, "end": v(-44.98, -20.62) * mm});
            skLineSegment(sketch, "E330", {"start": v(-44.98, -20.62) * mm, "end": v(-45.67, -20.37) * mm});
            skLineSegment(sketch, "E331", {"start": v(-45.67, -20.37) * mm, "end": v(-46, -19.16) * mm});
            skLineSegment(sketch, "E332", {"start": v(-46, -19.16) * mm, "end": v(-47.97, -18.75) * mm});
            skLineSegment(sketch, "E333", {"start": v(-47.97, -18.75) * mm, "end": v(-49.36, -15.76) * mm});
            skLineSegment(sketch, "E334", {"start": v(-32.67, -19.63) * mm, "end": v(-32.67, -17.7) * mm});
            skLineSegment(sketch, "E335", {"start": v(-32.67, -17.7) * mm, "end": v(-31.35, -16.85) * mm});
            skLineSegment(sketch, "E336", {"start": v(-31.35, -16.85) * mm, "end": v(-30.62, -16.01) * mm});
            skLineSegment(sketch, "E337", {"start": v(-30.62, -16.01) * mm, "end": v(-28.81, -17.82) * mm});
            skLineSegment(sketch, "E338", {"start": v(-28.81, -17.82) * mm, "end": v(-28.7, -18.9) * mm});
            skLineSegment(sketch, "E339", {"start": v(-28.7, -18.9) * mm, "end": v(-23.45, -18.48) * mm});
            skLineSegment(sketch, "E340", {"start": v(-23.45, -18.48) * mm, "end": v(-23.45, -20.05) * mm});
            skLineSegment(sketch, "E341", {"start": v(-23.45, -20.05) * mm, "end": v(-16.81, -20.11) * mm});
            skLineSegment(sketch, "E342", {"start": v(-16.81, -20.11) * mm, "end": v(-16.63, -25.12) * mm});
            skLineSegment(sketch, "E343", {"start": v(-16.63, -25.12) * mm, "end": v(-20.13, -24.51) * mm});
            skLineSegment(sketch, "E344", {"start": v(-20.13, -24.51) * mm, "end": v(-20.25, -23.43) * mm});
            skLineSegment(sketch, "E345", {"start": v(-20.25, -23.43) * mm, "end": v(-24.23, -22.7) * mm});
            skLineSegment(sketch, "E346", {"start": v(-24.23, -22.7) * mm, "end": v(-28.51, -21.02) * mm});
            skLineSegment(sketch, "E347", {"start": v(-28.51, -21.02) * mm, "end": v(-30.74, -20.11) * mm});
            skLineSegment(sketch, "E348", {"start": v(-30.74, -20.11) * mm, "end": v(-32.59, -20.17) * mm});
            skLineSegment(sketch, "E349", {"start": v(-32.59, -20.17) * mm, "end": v(-32.67, -19.63) * mm});
            skLineSegment(sketch, "E350", {"start": v(-34.08, -20.51) * mm, "end": v(-34.08, -22.75) * mm});
            skLineSegment(sketch, "E351", {"start": v(-34.08, -22.75) * mm, "end": v(-32.83, -23.2) * mm});
            skLineSegment(sketch, "E352", {"start": v(-32.83, -23.2) * mm, "end": v(-32.29, -26.77) * mm});
            skLineSegment(sketch, "E353", {"start": v(-32.29, -26.77) * mm, "end": v(-30.98, -27.6) * mm});
            skLineSegment(sketch, "E354", {"start": v(-30.98, -27.6) * mm, "end": v(-30.79, -29.52) * mm});
            skLineSegment(sketch, "E355", {"start": v(-30.79, -29.52) * mm, "end": v(-28.9, -29.65) * mm});
            skLineSegment(sketch, "E356", {"start": v(-28.9, -29.65) * mm, "end": v(-27.85, -30) * mm});
            skLineSegment(sketch, "E357", {"start": v(-27.85, -30) * mm, "end": v(-27.53, -31.18) * mm});
            skLineSegment(sketch, "E358", {"start": v(-27.53, -31.18) * mm, "end": v(-23.44, -31.24) * mm});
            skLineSegment(sketch, "E359", {"start": v(-23.44, -31.24) * mm, "end": v(-23.02, -29.9) * mm});
            skLineSegment(sketch, "E360", {"start": v(-23.02, -29.9) * mm, "end": v(-21.78, -29.49) * mm});
            skLineSegment(sketch, "E361", {"start": v(-21.78, -29.49) * mm, "end": v(-20.6, -29.58) * mm});
            skLineSegment(sketch, "E362", {"start": v(-20.6, -29.58) * mm, "end": v(-19.73, -28.69) * mm});
            skLineSegment(sketch, "E363", {"start": v(-19.73, -28.69) * mm, "end": v(-19, -27.92) * mm});
            skLineSegment(sketch, "E364", {"start": v(-19, -27.92) * mm, "end": v(-17.18, -27.6) * mm});
            skLineSegment(sketch, "E365", {"start": v(-17.18, -27.6) * mm, "end": v(-17.37, -25.88) * mm});
            skLineSegment(sketch, "E366", {"start": v(-17.37, -25.88) * mm, "end": v(-20.95, -25.15) * mm});
            skLineSegment(sketch, "E367", {"start": v(-20.95, -25.15) * mm, "end": v(-24.4, -24.16) * mm});
            skLineSegment(sketch, "E368", {"start": v(-24.4, -24.16) * mm, "end": v(-27.4, -22.89) * mm});
            skLineSegment(sketch, "E369", {"start": v(-27.4, -22.89) * mm, "end": v(-31.3, -21.26) * mm});
            skLineSegment(sketch, "E370", {"start": v(-31.3, -21.26) * mm, "end": v(-34.08, -20.51) * mm});
            skLineSegment(sketch, "E371", {"start": v(-35.14, -23.44) * mm, "end": v(-33.6, -23.65) * mm});
            skLineSegment(sketch, "E372", {"start": v(-33.6, -23.65) * mm, "end": v(-33.72, -26.62) * mm});
            skLineSegment(sketch, "E373", {"start": v(-33.72, -26.62) * mm, "end": v(-33.05, -27.31) * mm});
            skLineSegment(sketch, "E374", {"start": v(-33.05, -27.31) * mm, "end": v(-31.98, -27.74) * mm});
            skLineSegment(sketch, "E375", {"start": v(-31.98, -27.74) * mm, "end": v(-32.08, -33.15) * mm});
            skLineSegment(sketch, "E376", {"start": v(-32.08, -33.15) * mm, "end": v(-33.44, -34.33) * mm});
            skLineSegment(sketch, "E377", {"start": v(-33.44, -34.33) * mm, "end": v(-33.44, -40.42) * mm});
            skLineSegment(sketch, "E378", {"start": v(-33.44, -40.42) * mm, "end": v(-34.8, -41.19) * mm});
            skLineSegment(sketch, "E379", {"start": v(-34.8, -41.19) * mm, "end": v(-34.95, -47.34) * mm});
            skLineSegment(sketch, "E380", {"start": v(-34.95, -47.34) * mm, "end": v(-36.81, -47.3) * mm});
            skLineSegment(sketch, "E381", {"start": v(-36.81, -47.3) * mm, "end": v(-36.89, -45.33) * mm});
            skLineSegment(sketch, "E382", {"start": v(-36.89, -45.33) * mm, "end": v(-38.3, -45.18) * mm});
            skLineSegment(sketch, "E383", {"start": v(-38.3, -45.18) * mm, "end": v(-38.33, -40.7) * mm});
            skLineSegment(sketch, "E384", {"start": v(-38.33, -40.7) * mm, "end": v(-36.96, -40.58) * mm});
            skLineSegment(sketch, "E385", {"start": v(-36.96, -40.58) * mm, "end": v(-36.85, -37.16) * mm});
            skLineSegment(sketch, "E386", {"start": v(-36.85, -37.16) * mm, "end": v(-36.1, -35.68) * mm});
            skLineSegment(sketch, "E387", {"start": v(-36.1, -35.68) * mm, "end": v(-36.13, -25.16) * mm});
            skLineSegment(sketch, "E388", {"start": v(-36.13, -25.16) * mm, "end": v(-35.14, -23.44) * mm});
            skLineSegment(sketch, "E389", {"start": v(-20.58, -30.2) * mm, "end": v(-21.6, -31.18) * mm});
            skLineSegment(sketch, "E390", {"start": v(-21.6, -31.18) * mm, "end": v(-22.09, -33.03) * mm});
            skLineSegment(sketch, "E391", {"start": v(-22.09, -33.03) * mm, "end": v(-20.76, -34.35) * mm});
            skLineSegment(sketch, "E392", {"start": v(-20.76, -34.35) * mm, "end": v(-20.64, -37.73) * mm});
            skLineSegment(sketch, "E393", {"start": v(-20.64, -37.73) * mm, "end": v(-19.01, -38.4) * mm});
            skLineSegment(sketch, "E394", {"start": v(-19.01, -38.4) * mm, "end": v(-19.07, -40.32) * mm});
            skLineSegment(sketch, "E395", {"start": v(-19.07, -40.32) * mm, "end": v(-17.93, -41.83) * mm});
            skLineSegment(sketch, "E396", {"start": v(-17.93, -41.83) * mm, "end": v(-17.86, -44.07) * mm});
            skLineSegment(sketch, "E397", {"start": v(-17.86, -44.07) * mm, "end": v(-16.38, -45.38) * mm});
            skLineSegment(sketch, "E398", {"start": v(-16.38, -45.38) * mm, "end": v(-15.64, -45.78) * mm});
            skLineSegment(sketch, "E399", {"start": v(-15.64, -45.78) * mm, "end": v(-15.58, -46.92) * mm});
            skLineSegment(sketch, "E400", {"start": v(-15.58, -46.92) * mm, "end": v(-13.65, -47.15) * mm});
            skLineSegment(sketch, "E401", {"start": v(-13.65, -47.15) * mm, "end": v(-13.53, -45.78) * mm});
            skLineSegment(sketch, "E402", {"start": v(-13.53, -45.78) * mm, "end": v(-12.4, -45.16) * mm});
            skLineSegment(sketch, "E403", {"start": v(-12.4, -45.16) * mm, "end": v(-12.51, -42.37) * mm});
            skLineSegment(sketch, "E404", {"start": v(-12.51, -42.37) * mm, "end": v(-13.88, -41.68) * mm});
            skLineSegment(sketch, "E405", {"start": v(-13.88, -41.68) * mm, "end": v(-13.99, -39.4) * mm});
            skLineSegment(sketch, "E406", {"start": v(-13.99, -39.4) * mm, "end": v(-15.3, -38.95) * mm});
            skLineSegment(sketch, "E407", {"start": v(-15.3, -38.95) * mm, "end": v(-15.58, -36.79) * mm});
            skLineSegment(sketch, "E408", {"start": v(-15.58, -36.79) * mm, "end": v(-16.84, -36.22) * mm});
            skLineSegment(sketch, "E409", {"start": v(-16.84, -36.22) * mm, "end": v(-16.84, -31.72) * mm});
            skLineSegment(sketch, "E410", {"start": v(-16.84, -31.72) * mm, "end": v(-17.58, -31.55) * mm});
            skLineSegment(sketch, "E411", {"start": v(-17.58, -31.55) * mm, "end": v(-17.63, -29.4) * mm});
            skLineSegment(sketch, "E412", {"start": v(-17.63, -29.4) * mm, "end": v(-18.83, -29.62) * mm});
            skLineSegment(sketch, "E413", {"start": v(-18.83, -29.62) * mm, "end": v(-20.58, -30.2) * mm});
            skLineSegment(sketch, "E414", {"start": v(-32.71, -41.74) * mm, "end": v(-32.71, -43.67) * mm});
            skLineSegment(sketch, "E415", {"start": v(-32.71, -43.67) * mm, "end": v(-29.92, -44.05) * mm});
            skLineSegment(sketch, "E416", {"start": v(-29.92, -44.05) * mm, "end": v(-28.63, -45.12) * mm});
            skLineSegment(sketch, "E417", {"start": v(-28.63, -45.12) * mm, "end": v(-28.04, -45.98) * mm});
            skLineSegment(sketch, "E418", {"start": v(-28.04, -45.98) * mm, "end": v(-28.63, -47.38) * mm});
            skLineSegment(sketch, "E419", {"start": v(-28.63, -47.38) * mm, "end": v(-30.67, -47.92) * mm});
            skLineSegment(sketch, "E420", {"start": v(-30.67, -47.92) * mm, "end": v(-32.98, -49.1) * mm});
            skLineSegment(sketch, "E421", {"start": v(-32.98, -49.1) * mm, "end": v(-35.19, -49.37) * mm});
            skLineSegment(sketch, "E422", {"start": v(-35.19, -49.37) * mm, "end": v(-38.2, -49.1) * mm});
            skLineSegment(sketch, "E423", {"start": v(-38.2, -49.1) * mm, "end": v(-40.07, -47.76) * mm});
            skLineSegment(sketch, "E424", {"start": v(-40.07, -47.76) * mm, "end": v(-43.03, -47.54) * mm});
            skLineSegment(sketch, "E425", {"start": v(-43.03, -47.54) * mm, "end": v(-44.1, -45.93) * mm});
            skLineSegment(sketch, "E426", {"start": v(-44.1, -45.93) * mm, "end": v(-45.6, -45.82) * mm});
            skLineSegment(sketch, "E427", {"start": v(-45.6, -45.82) * mm, "end": v(-45.82, -48.24) * mm});
            skLineSegment(sketch, "E428", {"start": v(-45.82, -48.24) * mm, "end": v(-44.75, -49.53) * mm});
            skLineSegment(sketch, "E429", {"start": v(-44.75, -49.53) * mm, "end": v(-45.02, -50.98) * mm});
            skLineSegment(sketch, "E430", {"start": v(-45.02, -50.98) * mm, "end": v(-43.35, -51.63) * mm});
            skLineSegment(sketch, "E431", {"start": v(-43.35, -51.63) * mm, "end": v(-43.78, -53.45) * mm});
            skLineSegment(sketch, "E432", {"start": v(-43.78, -53.45) * mm, "end": v(-42.5, -54.2) * mm});
            skLineSegment(sketch, "E433", {"start": v(-42.5, -54.2) * mm, "end": v(-42.5, -55.6) * mm});
            skLineSegment(sketch, "E434", {"start": v(-42.5, -55.6) * mm, "end": v(-41.42, -56.08) * mm});
            skLineSegment(sketch, "E435", {"start": v(-41.42, -56.08) * mm, "end": v(-41.36, -57.91) * mm});
            skLineSegment(sketch, "E436", {"start": v(-41.36, -57.91) * mm, "end": v(-40.34, -58.77) * mm});
            skLineSegment(sketch, "E437", {"start": v(-40.34, -58.77) * mm, "end": v(-40.18, -61.3) * mm});
            skLineSegment(sketch, "E438", {"start": v(-40.18, -61.3) * mm, "end": v(-38.9, -61.94) * mm});
            skLineSegment(sketch, "E439", {"start": v(-38.9, -61.94) * mm, "end": v(-38.52, -63.01) * mm});
            skLineSegment(sketch, "E440", {"start": v(-38.52, -63.01) * mm, "end": v(-37.76, -63.23) * mm});
            skLineSegment(sketch, "E441", {"start": v(-37.76, -63.23) * mm, "end": v(-37.55, -65.65) * mm});
            skLineSegment(sketch, "E442", {"start": v(-37.55, -65.65) * mm, "end": v(-39.05, -65.6) * mm});
            skLineSegment(sketch, "E443", {"start": v(-39.05, -65.6) * mm, "end": v(-39.22, -65.22) * mm});
            skLineSegment(sketch, "E444", {"start": v(-39.22, -65.22) * mm, "end": v(-44.21, -65.06) * mm});
            skLineSegment(sketch, "E445", {"start": v(-44.21, -65.06) * mm, "end": v(-45.5, -66.24) * mm});
            skLineSegment(sketch, "E446", {"start": v(-45.5, -66.24) * mm, "end": v(-47, -66.72) * mm});
            skLineSegment(sketch, "E447", {"start": v(-47, -66.72) * mm, "end": v(-48.78, -69.72) * mm});
            skLineSegment(sketch, "E448", {"start": v(-48.78, -69.72) * mm, "end": v(-49, -74.13) * mm});
            skLineSegment(sketch, "E449", {"start": v(-49, -74.13) * mm, "end": v(-47.92, -74.77) * mm});
            skLineSegment(sketch, "E450", {"start": v(-47.92, -74.77) * mm, "end": v(-46.9, -76.12) * mm});
            skLineSegment(sketch, "E451", {"start": v(-46.9, -76.12) * mm, "end": v(-32.55, -76.06) * mm});
            skLineSegment(sketch, "E452", {"start": v(-32.55, -76.06) * mm, "end": v(-32.28, -75.04) * mm});
            skLineSegment(sketch, "E453", {"start": v(-32.28, -75.04) * mm, "end": v(-31.32, -74.72) * mm});
            skLineSegment(sketch, "E454", {"start": v(-31.32, -74.72) * mm, "end": v(-30.24, -74.24) * mm});
            skLineSegment(sketch, "E455", {"start": v(-30.24, -74.24) * mm, "end": v(-29.81, -73.48) * mm});
            skLineSegment(sketch, "E456", {"start": v(-29.81, -73.48) * mm, "end": v(-25.14, -73.38) * mm});
            skLineSegment(sketch, "E457", {"start": v(-25.14, -73.38) * mm, "end": v(-24.7, -65.75) * mm});
            skLineSegment(sketch, "E458", {"start": v(-24.7, -65.75) * mm, "end": v(-26, -65.48) * mm});
            skLineSegment(sketch, "E459", {"start": v(-26, -65.48) * mm, "end": v(-26.16, -62.74) * mm});
            skLineSegment(sketch, "E460", {"start": v(-26.16, -62.74) * mm, "end": v(-26.86, -60.97) * mm});
            skLineSegment(sketch, "E461", {"start": v(-26.86, -60.97) * mm, "end": v(-27.34, -59.52) * mm});
            skLineSegment(sketch, "E462", {"start": v(-27.34, -59.52) * mm, "end": v(-26.91, -50.6) * mm});
            skLineSegment(sketch, "E463", {"start": v(-26.91, -50.6) * mm, "end": v(-25.95, -49.3) * mm});
            skLineSegment(sketch, "E464", {"start": v(-25.95, -49.3) * mm, "end": v(-25.73, -43.67) * mm});
            skLineSegment(sketch, "E465", {"start": v(-25.73, -43.67) * mm, "end": v(-28.04, -43.08) * mm});
            skLineSegment(sketch, "E466", {"start": v(-28.04, -43.08) * mm, "end": v(-28.42, -41.68) * mm});
            skLineSegment(sketch, "E467", {"start": v(-28.42, -41.68) * mm, "end": v(-32.71, -41.74) * mm});
            skLineSegment(sketch, "E468", {"start": v(-39.07, -52.71) * mm, "end": v(-39.07, -54.2) * mm});
            skLineSegment(sketch, "E469", {"start": v(-39.07, -54.2) * mm, "end": v(-35.03, -53.96) * mm});
            skLineSegment(sketch, "E470", {"start": v(-35.03, -53.96) * mm, "end": v(-34.4, -52.71) * mm});
            skLineSegment(sketch, "E471", {"start": v(-34.4, -52.71) * mm, "end": v(-32.46, -52.48) * mm});
            skLineSegment(sketch, "E472", {"start": v(-32.46, -52.48) * mm, "end": v(-32.7, -50.95) * mm});
            skLineSegment(sketch, "E473", {"start": v(-32.7, -50.95) * mm, "end": v(-36.85, -50.66) * mm});
            skLineSegment(sketch, "E474", {"start": v(-36.85, -50.66) * mm, "end": v(-37.36, -52.6) * mm});
            skLineSegment(sketch, "E475", {"start": v(-37.36, -52.6) * mm, "end": v(-39.07, -52.71) * mm});
            skLineSegment(sketch, "E476", {"start": v(-38.15, -56.74) * mm, "end": v(-38.15, -58.4) * mm});
            skLineSegment(sketch, "E477", {"start": v(-38.15, -58.4) * mm, "end": v(-34.49, -58.21) * mm});
            skLineSegment(sketch, "E478", {"start": v(-34.49, -58.21) * mm, "end": v(-32.05, -57.04) * mm});
            skLineSegment(sketch, "E479", {"start": v(-32.05, -57.04) * mm, "end": v(-32.12, -55.23) * mm});
            skLineSegment(sketch, "E480", {"start": v(-32.12, -55.23) * mm, "end": v(-34.85, -55.34) * mm});
            skLineSegment(sketch, "E481", {"start": v(-34.85, -55.34) * mm, "end": v(-35.87, -56.59) * mm});
            skLineSegment(sketch, "E482", {"start": v(-35.87, -56.59) * mm, "end": v(-38.15, -56.74) * mm});
            skLineSegment(sketch, "E483", {"start": v(-35.47, -63.71) * mm, "end": v(-34.16, -64.23) * mm});
            skLineSegment(sketch, "E484", {"start": v(-34.16, -64.23) * mm, "end": v(-33.24, -63.59) * mm});
            skLineSegment(sketch, "E485", {"start": v(-33.24, -63.59) * mm, "end": v(-32.76, -63.59) * mm});
            skLineSegment(sketch, "E486", {"start": v(-32.76, -63.59) * mm, "end": v(-32.18, -64.16) * mm});
            skLineSegment(sketch, "E487", {"start": v(-32.18, -64.16) * mm, "end": v(-30.55, -64.23) * mm});
            skLineSegment(sketch, "E488", {"start": v(-30.55, -64.23) * mm, "end": v(-30.14, -63.33) * mm});
            skLineSegment(sketch, "E489", {"start": v(-30.14, -63.33) * mm, "end": v(-31.2, -62.37) * mm});
            skLineSegment(sketch, "E490", {"start": v(-31.2, -62.37) * mm, "end": v(-31.35, -61.22) * mm});
            skLineSegment(sketch, "E491", {"start": v(-31.35, -61.22) * mm, "end": v(-34.45, -61.1) * mm});
            skLineSegment(sketch, "E492", {"start": v(-34.45, -61.1) * mm, "end": v(-34.58, -62.25) * mm});
            skLineSegment(sketch, "E493", {"start": v(-34.58, -62.25) * mm, "end": v(-35.5, -63.08) * mm});
            skLineSegment(sketch, "E494", {"start": v(-35.5, -63.08) * mm, "end": v(-35.47, -63.71) * mm});
            skLineSegment(sketch, "E495", {"start": v(-4.98, -17.64) * mm, "end": v(-2.7, -16.54) * mm});
            skLineSegment(sketch, "E496", {"start": v(-2.7, -16.54) * mm, "end": v(-3.05, -12.91) * mm});
            skLineSegment(sketch, "E497", {"start": v(-3.05, -12.91) * mm, "end": v(-1.9, -12.13) * mm});
            skLineSegment(sketch, "E498", {"start": v(-1.9, -12.13) * mm, "end": v(-1.93, -8.15) * mm});
            skLineSegment(sketch, "E499", {"start": v(-1.93, -8.15) * mm, "end": v(-0.57, -7.94) * mm});
            skLineSegment(sketch, "E500", {"start": v(-0.57, -7.94) * mm, "end": v(-0.43, 2.6) * mm});
            skLineSegment(sketch, "E501", {"start": v(-0.43, 2.6) * mm, "end": v(0.98, 3.24) * mm});
            skLineSegment(sketch, "E502", {"start": v(0.98, 3.24) * mm, "end": v(1, 8.37) * mm});
            skLineSegment(sketch, "E503", {"start": v(1, 8.37) * mm, "end": v(2.2, 8.73) * mm});
            skLineSegment(sketch, "E504", {"start": v(2.2, 8.73) * mm, "end": v(2.08, 10.42) * mm});
            skLineSegment(sketch, "E505", {"start": v(2.08, 10.42) * mm, "end": v(-1.3, 10.36) * mm});
            skLineSegment(sketch, "E506", {"start": v(-1.3, 10.36) * mm, "end": v(-1.83, 8.91) * mm});
            skLineSegment(sketch, "E507", {"start": v(-1.83, 8.91) * mm, "end": v(-3.4, 8.64) * mm});
            skLineSegment(sketch, "E508", {"start": v(-3.4, 8.64) * mm, "end": v(-3.55, 9.21) * mm});
            skLineSegment(sketch, "E509", {"start": v(-3.55, 9.21) * mm, "end": v(-5.1, 8.97) * mm});
            skLineSegment(sketch, "E510", {"start": v(-5.1, 8.97) * mm, "end": v(-4.96, -7.04) * mm});
            skLineSegment(sketch, "E511", {"start": v(-4.96, -7.04) * mm, "end": v(-4.79, -8) * mm});
            skLineSegment(sketch, "E512", {"start": v(-4.79, -8) * mm, "end": v(-4.24, -9.95) * mm});
            skLineSegment(sketch, "E513", {"start": v(-4.24, -9.95) * mm, "end": v(-4.51, -11.45) * mm});
            skLineSegment(sketch, "E514", {"start": v(-4.51, -11.45) * mm, "end": v(-5.15, -11.64) * mm});
            skLineSegment(sketch, "E515", {"start": v(-5.15, -11.64) * mm, "end": v(-4.98, -17.64) * mm});
            skLineSegment(sketch, "E516", {"start": v(-4.63, 11.7) * mm, "end": v(-4.63, 10.16) * mm});
            skLineSegment(sketch, "E517", {"start": v(-4.63, 10.16) * mm, "end": v(-2.33, 10.28) * mm});
            skLineSegment(sketch, "E518", {"start": v(-2.33, 10.28) * mm, "end": v(-2.22, 11.47) * mm});
            skLineSegment(sketch, "E519", {"start": v(-2.22, 11.47) * mm, "end": v(2.8, 11.61) * mm});
            skLineSegment(sketch, "E520", {"start": v(2.8, 11.61) * mm, "end": v(2.94, 14.94) * mm});
            skLineSegment(sketch, "E521", {"start": v(2.94, 14.94) * mm, "end": v(1.8, 14.66) * mm});
            skLineSegment(sketch, "E522", {"start": v(1.8, 14.66) * mm, "end": v(1.57, 13.24) * mm});
            skLineSegment(sketch, "E523", {"start": v(1.57, 13.24) * mm, "end": v(-3.27, 13.24) * mm});
            skLineSegment(sketch, "E524", {"start": v(-3.27, 13.24) * mm, "end": v(-3.5, 11.96) * mm});
            skLineSegment(sketch, "E525", {"start": v(-3.5, 11.96) * mm, "end": v(-4.63, 11.7) * mm});
            skLineSegment(sketch, "E526", {"start": v(-17.76, -50.4) * mm, "end": v(-19.43, -51.69) * mm});
            skLineSegment(sketch, "E527", {"start": v(-19.43, -51.69) * mm, "end": v(-20.36, -53.1) * mm});
            skLineSegment(sketch, "E528", {"start": v(-20.36, -53.1) * mm, "end": v(-17.39, -53.86) * mm});
            skLineSegment(sketch, "E529", {"start": v(-17.39, -53.86) * mm, "end": v(-16.72, -52.9) * mm});
            skLineSegment(sketch, "E530", {"start": v(-16.72, -52.9) * mm, "end": v(-15.19, -52.61) * mm});
            skLineSegment(sketch, "E531", {"start": v(-15.19, -52.61) * mm, "end": v(-12.32, -48.88) * mm});
            skLineSegment(sketch, "E532", {"start": v(-12.32, -48.88) * mm, "end": v(-10.22, -46.43) * mm});
            skLineSegment(sketch, "E533", {"start": v(-10.22, -46.43) * mm, "end": v(-10.4, -45.63) * mm});
            skLineSegment(sketch, "E534", {"start": v(-10.4, -45.63) * mm, "end": v(-11.17, -44.29) * mm});
            skLineSegment(sketch, "E535", {"start": v(-11.17, -44.29) * mm, "end": v(-10.02, -43.23) * mm});
            skLineSegment(sketch, "E536", {"start": v(-10.02, -43.23) * mm, "end": v(-8.3, -44.67) * mm});
            skLineSegment(sketch, "E537", {"start": v(-8.3, -44.67) * mm, "end": v(-7.91, -47.16) * mm});
            skLineSegment(sketch, "E538", {"start": v(-7.91, -47.16) * mm, "end": v(-6.67, -48.6) * mm});
            skLineSegment(sketch, "E539", {"start": v(-6.67, -48.6) * mm, "end": v(-6.1, -50.32) * mm});
            skLineSegment(sketch, "E540", {"start": v(-6.1, -50.32) * mm, "end": v(-5.42, -52.42) * mm});
            skLineSegment(sketch, "E541", {"start": v(-5.42, -52.42) * mm, "end": v(-4.47, -54.34) * mm});
            skLineSegment(sketch, "E542", {"start": v(-4.47, -54.34) * mm, "end": v(-3.9, -55.68) * mm});
            skLineSegment(sketch, "E543", {"start": v(-3.9, -55.68) * mm, "end": v(-3.32, -57.02) * mm});
            skLineSegment(sketch, "E544", {"start": v(-3.32, -57.02) * mm, "end": v(-2.65, -59.5) * mm});
            skLineSegment(sketch, "E545", {"start": v(-2.65, -59.5) * mm, "end": v(-3.7, -61.61) * mm});
            skLineSegment(sketch, "E546", {"start": v(-3.7, -61.61) * mm, "end": v(-4.4, -62.58) * mm});
            skLineSegment(sketch, "E547", {"start": v(-4.4, -62.58) * mm, "end": v(-5.92, -64.86) * mm});
            skLineSegment(sketch, "E548", {"start": v(-5.92, -64.86) * mm, "end": v(-6.86, -66.3) * mm});
            skLineSegment(sketch, "E549", {"start": v(-6.86, -66.3) * mm, "end": v(-6, -66.3) * mm});
            skLineSegment(sketch, "E550", {"start": v(-6, -66.3) * mm, "end": v(-4.85, -65.15) * mm});
            skLineSegment(sketch, "E551", {"start": v(-4.85, -65.15) * mm, "end": v(-3.6, -63.43) * mm});
            skLineSegment(sketch, "E552", {"start": v(-3.6, -63.43) * mm, "end": v(-2.74, -62.47) * mm});
            skLineSegment(sketch, "E553", {"start": v(-2.74, -62.47) * mm, "end": v(4.34, -62.38) * mm});
            skLineSegment(sketch, "E554", {"start": v(4.34, -62.38) * mm, "end": v(4.53, -67.07) * mm});
            skLineSegment(sketch, "E555", {"start": v(4.53, -67.07) * mm, "end": v(0.9, -71.28) * mm});
            skLineSegment(sketch, "E556", {"start": v(0.9, -71.28) * mm, "end": v(0.9, -76.26) * mm});
            skLineSegment(sketch, "E557", {"start": v(0.9, -76.26) * mm, "end": v(-4.37, -76.26) * mm});
            skLineSegment(sketch, "E558", {"start": v(-4.37, -76.26) * mm, "end": v(-4.66, -74.54) * mm});
            skLineSegment(sketch, "E559", {"start": v(-4.66, -74.54) * mm, "end": v(-6.96, -74.54) * mm});
            skLineSegment(sketch, "E560", {"start": v(-6.96, -74.54) * mm, "end": v(-11.65, -74.25) * mm});
            skLineSegment(sketch, "E561", {"start": v(-11.65, -74.25) * mm, "end": v(-11.55, -71.76) * mm});
            skLineSegment(sketch, "E562", {"start": v(-11.55, -71.76) * mm, "end": v(-13.46, -71.18) * mm});
            skLineSegment(sketch, "E563", {"start": v(-13.46, -71.18) * mm, "end": v(-12.99, -65.15) * mm});
            skLineSegment(sketch, "E564", {"start": v(-12.99, -65.15) * mm, "end": v(-22.94, -53.57) * mm});
            skLineSegment(sketch, "E565", {"start": v(-22.94, -53.57) * mm, "end": v(-20.16, -48.88) * mm});
            skLineSegment(sketch, "E566", {"start": v(-20.16, -48.88) * mm, "end": v(-18.85, -49.07) * mm});
            skLineSegment(sketch, "E567", {"start": v(-18.85, -49.07) * mm, "end": v(-17.76, -50.4) * mm});
            skLineSegment(sketch, "E568", {"start": v(-14.04, -55.98) * mm, "end": v(-12.71, -57.07) * mm});
            skLineSegment(sketch, "E569", {"start": v(-12.71, -57.07) * mm, "end": v(-10.54, -56.7) * mm});
            skLineSegment(sketch, "E570", {"start": v(-10.54, -56.7) * mm, "end": v(-9.5, -54.3) * mm});
            skLineSegment(sketch, "E571", {"start": v(-9.5, -54.3) * mm, "end": v(-8.33, -54.09) * mm});
            skLineSegment(sketch, "E572", {"start": v(-8.33, -54.09) * mm, "end": v(-7.97, -52.76) * mm});
            skLineSegment(sketch, "E573", {"start": v(-7.97, -52.76) * mm, "end": v(-10.54, -52.52) * mm});
            skLineSegment(sketch, "E574", {"start": v(-10.54, -52.52) * mm, "end": v(-11.55, -53.89) * mm});
            skLineSegment(sketch, "E575", {"start": v(-11.55, -53.89) * mm, "end": v(-13.12, -55.18) * mm});
            skLineSegment(sketch, "E576", {"start": v(-13.12, -55.18) * mm, "end": v(-14.04, -55.98) * mm});
            skLineSegment(sketch, "E577", {"start": v(-11.95, -59.26) * mm, "end": v(-10.48, -59.65) * mm});
            skLineSegment(sketch, "E578", {"start": v(-10.48, -59.65) * mm, "end": v(-10.59, -60.73) * mm});
            skLineSegment(sketch, "E579", {"start": v(-10.59, -60.73) * mm, "end": v(-9.19, -60.94) * mm});
            skLineSegment(sketch, "E580", {"start": v(-9.19, -60.94) * mm, "end": v(-8.22, -58.97) * mm});
            skLineSegment(sketch, "E581", {"start": v(-8.22, -58.97) * mm, "end": v(-6.64, -57.6) * mm});
            skLineSegment(sketch, "E582", {"start": v(-6.64, -57.6) * mm, "end": v(-7.04, -55.17) * mm});
            skLineSegment(sketch, "E583", {"start": v(-7.04, -55.17) * mm, "end": v(-9.65, -57.86) * mm});
            skLineSegment(sketch, "E584", {"start": v(-9.65, -57.86) * mm, "end": v(-11.52, -58.25) * mm});
            skLineSegment(sketch, "E585", {"start": v(-11.52, -58.25) * mm, "end": v(-11.95, -59.26) * mm});
            skLineSegment(sketch, "E586", {"start": v(-49.36, -15.76) * mm, "end": v(-49.36, -12.65) * mm});
            skLineSegment(sketch, "E587", {"start": v(-49.36, -12.65) * mm, "end": v(-48.34, -12.88) * mm});
            skLineSegment(sketch, "E588", {"start": v(-48.34, -12.88) * mm, "end": v(-47.76, -14.1) * mm});
            skLineSegment(sketch, "E589", {"start": v(-47.76, -14.1) * mm, "end": v(-47.17, -15.45) * mm});
            skLineSegment(sketch, "E590", {"start": v(-47.17, -15.45) * mm, "end": v(-46.13, -15.95) * mm});
            skLineSegment(sketch, "E591", {"start": v(-46.13, -15.95) * mm, "end": v(-45.61, -17.04) * mm});
            skLineSegment(sketch, "E592", {"start": v(-45.61, -17.04) * mm, "end": v(-44.86, -17.4) * mm});
            skLineSegment(sketch, "E593", {"start": v(-45, -15.9) * mm, "end": v(-45.7, -15.13) * mm});
            skLineSegment(sketch, "E594", {"start": v(-45.7, -15.13) * mm, "end": v(-45.75, -13.14) * mm});
            skLineSegment(sketch, "E595", {"start": v(-45.75, -13.14) * mm, "end": v(-45.4, -12.59) * mm});
            skLineSegment(sketch, "E596", {"start": v(-28.08, 56.06) * mm, "end": v(-28.1, 63.47) * mm});
            skLineSegment(sketch, "E597", {"start": v(-28.1, 63.47) * mm, "end": v(-26.5, 63.46) * mm});
            skLineSegment(sketch, "E598", {"start": v(-26.5, 63.46) * mm, "end": v(-26.44, 62.47) * mm});
            skLineSegment(sketch, "E599", {"start": v(-21.37, 63.6) * mm, "end": v(-21.37, 61.88) * mm});
            skLineSegment(sketch, "E600", {"start": v(-20.43, 55.93) * mm, "end": v(-15.63, 55.93) * mm});
            skLineSegment(sketch, "E601", {"start": v(-15.63, 55.93) * mm, "end": v(-15.63, 57.46) * mm});
            skLineSegment(sketch, "E602", {"start": v(-15.63, 57.46) * mm, "end": v(-17, 57.46) * mm});
            skLineSegment(sketch, "E603", {"start": v(-17, 57.46) * mm, "end": v(-17, 61.77) * mm});
            skLineSegment(sketch, "E604", {"start": v(-17, 61.77) * mm, "end": v(-13.12, 61.77) * mm});
            skLineSegment(sketch, "E605", {"start": v(-13.12, 61.77) * mm, "end": v(-13.12, 63.61) * mm});
            skLineSegment(sketch, "E606", {"start": v(-13.12, 63.61) * mm, "end": v(-21.37, 63.6) * mm});
            skSolve(sketch);
        }
        {
            var Q0;
            Q0=makeQuery(id+"F0.imprint","IMPRINT",FACE,{"disambiguationData":[TD([[makeQuery(id+"F0.imprint","IMPRINT",EDGE,{"derivedFrom":sQuery(id+"F0.wireOp",EDGE,"E0")}),1.0]])]});
            var Q1;
            Q1=makeQuery(id+"F0.imprint","IMPRINT",FACE,{"disambiguationData":[TD([[makeQuery(id+"F0.imprint","IMPRINT",EDGE,{"derivedFrom":sQuery(id+"F0.wireOp",EDGE,"E68")}),1.0]])]});
            var Q2;
            Q2=makeQuery(id+"F0.imprint","IMPRINT",FACE,{"disambiguationData":[TD([[makeQuery(id+"F0.imprint","IMPRINT",EDGE,{"derivedFrom":sQuery(id+"F0.wireOp",EDGE,"E74")}),1.0]])]});
            var Q3;
            Q3=makeQuery(id+"F0.imprint","IMPRINT",FACE,{"disambiguationData":[TD([[makeQuery(id+"F0.imprint","IMPRINT",EDGE,{"derivedFrom":sQuery(id+"F0.wireOp",EDGE,"E78")}),1.0]])]});
            var Q4;
            Q4=makeQuery(id+"F0.imprint","IMPRINT",FACE,{"disambiguationData":[TD([[makeQuery(id+"F0.imprint","IMPRINT",EDGE,{"derivedFrom":sQuery(id+"F0.wireOp",EDGE,"E82")}),1.0]])]});
            var Q5;
            Q5=makeQuery(id+"F0.imprint","IMPRINT",FACE,{"disambiguationData":[TD([[makeQuery(id+"F0.imprint","IMPRINT",EDGE,{"derivedFrom":sQuery(id+"F0.wireOp",EDGE,"E105")}),1.0]])]});
            var Q6;
            Q6=makeQuery(id+"F0.imprint","IMPRINT",FACE,{"disambiguationData":[TD([[makeQuery(id+"F0.imprint","IMPRINT",EDGE,{"derivedFrom":sQuery(id+"F0.wireOp",EDGE,"E101")}),1.0]])]});
            var Q7;
            Q7=makeQuery(id+"F0.imprint","IMPRINT",FACE,{"disambiguationData":[TD([[makeQuery(id+"F0.imprint","IMPRINT",EDGE,{"derivedFrom":sQuery(id+"F0.wireOp",EDGE,"E97")}),1.0]])]});
            var Q8;
            Q8=makeQuery(id+"F0.imprint","IMPRINT",FACE,{"disambiguationData":[TD([[makeQuery(id+"F0.imprint","IMPRINT",EDGE,{"derivedFrom":sQuery(id+"F0.wireOp",EDGE,"E93")}),1.0]])]});
            var Q9;
            Q9=makeQuery(id+"F0.imprint","IMPRINT",FACE,{"disambiguationData":[TD([[makeQuery(id+"F0.imprint","IMPRINT",EDGE,{"derivedFrom":sQuery(id+"F0.wireOp",EDGE,"E89")}),-1.0]])]});
            var Q10;
            Q10=makeQuery(id+"F0.imprint","IMPRINT",FACE,{"disambiguationData":[TD([[makeQuery(id+"F0.imprint","IMPRINT",EDGE,{"derivedFrom":sQuery(id+"F0.wireOp",EDGE,"E110")}),-1.0]])]});
            var Q11;
            Q11=makeQuery(id+"F0.imprint","IMPRINT",FACE,{"disambiguationData":[TD([[makeQuery(id+"F0.imprint","IMPRINT",EDGE,{"derivedFrom":sQuery(id+"F0.wireOp",EDGE,"E151")}),-1.0]])]});
            var Q12;
            Q12=makeQuery(id+"F0.imprint","IMPRINT",FACE,{"disambiguationData":[TD([[makeQuery(id+"F0.imprint","IMPRINT",EDGE,{"derivedFrom":sQuery(id+"F0.wireOp",EDGE,"E189")}),1.0]])]});
            var Q13;
            Q13=makeQuery(id+"F0.imprint","IMPRINT",FACE,{"disambiguationData":[TD([[makeQuery(id+"F0.imprint","IMPRINT",EDGE,{"derivedFrom":sQuery(id+"F0.wireOp",EDGE,"E203")}),-1.0]])]});
            var Q14;
            Q14=makeQuery(id+"F0.imprint","IMPRINT",FACE,{"disambiguationData":[TD([[makeQuery(id+"F0.imprint","IMPRINT",EDGE,{"derivedFrom":sQuery(id+"F0.wireOp",EDGE,"E247")}),-1.0]])]});
            var Q15;
            Q15=makeQuery(id+"F0.imprint","IMPRINT",FACE,{"disambiguationData":[TD([[makeQuery(id+"F0.imprint","IMPRINT",EDGE,{"derivedFrom":sQuery(id+"F0.wireOp",EDGE,"E261")}),1.0]])]});
            var Q16;
            Q16=makeQuery(id+"F0.imprint","IMPRINT",FACE,{"disambiguationData":[TD([[makeQuery(id+"F0.imprint","IMPRINT",EDGE,{"derivedFrom":sQuery(id+"F0.wireOp",EDGE,"E266")}),-1.0]])]});
            var Q17;
            Q17=makeQuery(id+"F0.imprint","IMPRINT",FACE,{"disambiguationData":[TD([[makeQuery(id+"F0.imprint","IMPRINT",EDGE,{"derivedFrom":sQuery(id+"F0.wireOp",EDGE,"E272")}),-1.0]])]});
            var Q18;
            Q18=makeQuery(id+"F0.imprint","IMPRINT",FACE,{"disambiguationData":[TD([[makeQuery(id+"F0.imprint","IMPRINT",EDGE,{"derivedFrom":sQuery(id+"F0.wireOp",EDGE,"E290")}),1.0]])]});
            var Q19;
            Q19=makeQuery(id+"F0.imprint","IMPRINT",FACE,{"disambiguationData":[TD([[makeQuery(id+"F0.imprint","IMPRINT",EDGE,{"derivedFrom":sQuery(id+"F0.wireOp",EDGE,"E282")}),1.0]])]});
            var Q20;
            Q20=makeQuery(id+"F0.imprint","IMPRINT",FACE,{"disambiguationData":[TD([[makeQuery(id+"F0.imprint","IMPRINT",EDGE,{"derivedFrom":sQuery(id+"F0.wireOp",EDGE,"E298")}),1.0]])]});
            var Q21;
            Q21=makeQuery(id+"F0.imprint","IMPRINT",FACE,{"disambiguationData":[TD([[makeQuery(id+"F0.imprint","IMPRINT",EDGE,{"derivedFrom":sQuery(id+"F0.wireOp",EDGE,"E495")}),1.0]])]});
            var Q22;
            Q22=makeQuery(id+"F0.imprint","IMPRINT",FACE,{"disambiguationData":[TD([[makeQuery(id+"F0.imprint","IMPRINT",EDGE,{"derivedFrom":sQuery(id+"F0.wireOp",EDGE,"E516")}),1.0]])]});
            var Q23;
            Q23=makeQuery(id+"F0.imprint","IMPRINT",FACE,{"disambiguationData":[TD([[makeQuery(id+"F0.imprint","IMPRINT",EDGE,{"derivedFrom":sQuery(id+"F0.wireOp",EDGE,"E334")}),-1.0]])]});
            var Q24;
            Q24=makeQuery(id+"F0.imprint","IMPRINT",FACE,{"disambiguationData":[TD([[makeQuery(id+"F0.imprint","IMPRINT",EDGE,{"derivedFrom":sQuery(id+"F0.wireOp",EDGE,"E350")}),1.0]])]});
            var Q25;
            Q25=makeQuery(id+"F0.imprint","IMPRINT",FACE,{"disambiguationData":[TD([[makeQuery(id+"F0.imprint","IMPRINT",EDGE,{"derivedFrom":sQuery(id+"F0.wireOp",EDGE,"E304")}),-1.0]])]});
            var Q26;
            Q26=makeQuery(id+"F0.imprint","IMPRINT",FACE,{"disambiguationData":[TD([[makeQuery(id+"F0.imprint","IMPRINT",EDGE,{"derivedFrom":sQuery(id+"F0.wireOp",EDGE,"E371")}),-1.0]])]});
            var Q27;
            Q27=makeQuery(id+"F0.imprint","IMPRINT",FACE,{"disambiguationData":[TD([[makeQuery(id+"F0.imprint","IMPRINT",EDGE,{"derivedFrom":sQuery(id+"F0.wireOp",EDGE,"E389")}),1.0]])]});
            var Q28;
            Q28=makeQuery(id+"F0.imprint","IMPRINT",FACE,{"disambiguationData":[TD([[makeQuery(id+"F0.imprint","IMPRINT",EDGE,{"derivedFrom":sQuery(id+"F0.wireOp",EDGE,"E414")}),1.0]])]});
            var Q29;
            Q29=makeQuery(id+"F0.imprint","IMPRINT",FACE,{"disambiguationData":[TD([[makeQuery(id+"F0.imprint","IMPRINT",EDGE,{"derivedFrom":sQuery(id+"F0.wireOp",EDGE,"E526")}),-1.0]])]});
            var Q30;
            Q30=makeQuery(id+"F0.imprint","IMPRINT",FACE,{"disambiguationData":[TD([[makeQuery(id+"F0.imprint","IMPRINT",EDGE,{"derivedFrom":sQuery(id+"F0.wireOp",EDGE,"E36")}),1.0]])]});
            var Q31;
            Q31=makeQuery(id+"F0.imprint","IMPRINT",FACE,{"disambiguationData":[TD([[makeQuery(id+"F0.imprint","IMPRINT",EDGE,{"derivedFrom":sQuery(id+"F0.wireOp",EDGE,"E599")}),1.0]])]});
            extrude(context, id + "F1", {"entities" : qUnion([Q0, Q1, Q2, Q3, Q4, Q5, Q6, Q7, Q8, Q9, Q10, Q11, Q12, Q13, Q14, Q15, Q16, Q17, Q18, Q19, Q20, Q21, Q22, Q23, Q24, Q25, Q26, Q27, Q28, Q29, Q30, Q31]), "depth" : 12.7 * mm, "hasSecondDirection" : true, "secondDirectionOppositeDirection" : true, "secondDirectionDepth" : 12.7 * mm});
        }
        {
            var Q0;
            Q0=qCreatedBy(makeId("Front.planeOp"),FACE);
            var sketch = newSketch(context, id + "F2", { "sketchPlane" : qUnion([Q0])});
            skLineSegment(sketch, "E607", {"start": v(15.98, 27.1) * mm, "end": v(29.52, 27.1) * mm});
            skLineSegment(sketch, "E608", {"start": v(29.52, 27.1) * mm, "end": v(32.1, 25.6) * mm});
            skLineSegment(sketch, "E609", {"start": v(32.1, 25.6) * mm, "end": v(35.53, 23.77) * mm});
            skLineSegment(sketch, "E610", {"start": v(35.53, 23.77) * mm, "end": v(37.79, 21.09) * mm});
            skLineSegment(sketch, "E611", {"start": v(37.79, 21.09) * mm, "end": v(39.72, 18.3) * mm});
            skLineSegment(sketch, "E612", {"start": v(39.72, 18.3) * mm, "end": v(41.33, 15.82) * mm});
            skLineSegment(sketch, "E613", {"start": v(41.33, 15.82) * mm, "end": v(41.33, 7.12) * mm});
            skLineSegment(sketch, "E614", {"start": v(41.33, 7.12) * mm, "end": v(40.26, 5.83) * mm});
            skLineSegment(sketch, "E615", {"start": v(40.26, 5.83) * mm, "end": v(40.15, 3.9) * mm});
            skLineSegment(sketch, "E616", {"start": v(40.15, 3.9) * mm, "end": v(38.65, 2.4) * mm});
            skLineSegment(sketch, "E617", {"start": v(38.65, 2.4) * mm, "end": v(40.15, 0.89) * mm});
            skLineSegment(sketch, "E618", {"start": v(40.15, 0.89) * mm, "end": v(40.15, -5.45) * mm});
            skLineSegment(sketch, "E619", {"start": v(40.15, -5.45) * mm, "end": v(38.65, -7.06) * mm});
            skLineSegment(sketch, "E620", {"start": v(38.65, -7.06) * mm, "end": v(36.6, -9.86) * mm});
            skLineSegment(sketch, "E621", {"start": v(36.6, -9.86) * mm, "end": v(33.81, -12) * mm});
            skLineSegment(sketch, "E622", {"start": v(33.81, -12) * mm, "end": v(30.37, -14.05) * mm});
            skLineSegment(sketch, "E623", {"start": v(30.37, -14.05) * mm, "end": v(15.76, -14.05) * mm});
            skLineSegment(sketch, "E624", {"start": v(15.76, -14.05) * mm, "end": v(12.97, -12.33) * mm});
            skLineSegment(sketch, "E625", {"start": v(12.97, -12.33) * mm, "end": v(10.5, -10.93) * mm});
            skLineSegment(sketch, "E626", {"start": v(10.5, -10.93) * mm, "end": v(7.6, -8.35) * mm});
            skLineSegment(sketch, "E627", {"start": v(7.6, -8.35) * mm, "end": v(7.6, -4.92) * mm});
            skLineSegment(sketch, "E628", {"start": v(7.6, -4.92) * mm, "end": v(5.45, -4.92) * mm});
            skLineSegment(sketch, "E629", {"start": v(5.45, -4.92) * mm, "end": v(5.45, 0) * mm});
            skLineSegment(sketch, "E630", {"start": v(5.45, 0) * mm, "end": v(7.27, 2.18) * mm});
            skLineSegment(sketch, "E631", {"start": v(7.27, 2.18) * mm, "end": v(5.98, 4.43) * mm});
            skLineSegment(sketch, "E632", {"start": v(5.98, 4.43) * mm, "end": v(4.48, 7.12) * mm});
            skLineSegment(sketch, "E633", {"start": v(4.48, 7.12) * mm, "end": v(4.48, 16.04) * mm});
            skLineSegment(sketch, "E634", {"start": v(4.48, 16.04) * mm, "end": v(6.74, 19.47) * mm});
            skLineSegment(sketch, "E635", {"start": v(6.74, 19.47) * mm, "end": v(9.53, 22.91) * mm});
            skLineSegment(sketch, "E636", {"start": v(9.53, 22.91) * mm, "end": v(12.54, 25.38) * mm});
            skLineSegment(sketch, "E637", {"start": v(12.54, 25.38) * mm, "end": v(15.98, 27.1) * mm});
            skLineSegment(sketch, "E638", {"start": v(9.54, -1.97) * mm, "end": v(10.47, -1.97) * mm});
            skLineSegment(sketch, "E639", {"start": v(10.47, -1.97) * mm, "end": v(10.47, 0.01) * mm});
            skLineSegment(sketch, "E640", {"start": v(10.47, 0.01) * mm, "end": v(11.02, 1.29) * mm});
            skLineSegment(sketch, "E641", {"start": v(11.02, 1.29) * mm, "end": v(12.22, 1.12) * mm});
            skLineSegment(sketch, "E642", {"start": v(12.22, 1.12) * mm, "end": v(12.22, 0) * mm});
            skLineSegment(sketch, "E643", {"start": v(12.22, 0) * mm, "end": v(13.5, -1.9) * mm});
            skLineSegment(sketch, "E644", {"start": v(13.5, -1.9) * mm, "end": v(17.7, -4.2) * mm});
            skLineSegment(sketch, "E645", {"start": v(17.7, -4.2) * mm, "end": v(23.54, -4.2) * mm});
            skLineSegment(sketch, "E646", {"start": v(23.54, -4.2) * mm, "end": v(29.97, -4.2) * mm});
            skLineSegment(sketch, "E647", {"start": v(30.34, -3.05) * mm, "end": v(31.77, -2.4) * mm});
            skLineSegment(sketch, "E648", {"start": v(31.77, -2.4) * mm, "end": v(33.2, -1.7) * mm});
            skLineSegment(sketch, "E649", {"start": v(33.2, -1.7) * mm, "end": v(33.7, 0.86) * mm});
            skLineSegment(sketch, "E650", {"start": v(33.7, 0.86) * mm, "end": v(35.07, 0.95) * mm});
            skLineSegment(sketch, "E651", {"start": v(35.07, 0.95) * mm, "end": v(35.2, -0.63) * mm});
            skLineSegment(sketch, "E652", {"start": v(35.2, -0.63) * mm, "end": v(36.6, -1.01) * mm});
            skLineSegment(sketch, "E653", {"start": v(36.6, -1.01) * mm, "end": v(36.6, -2.38) * mm});
            skLineSegment(sketch, "E654", {"start": v(36.6, -2.38) * mm, "end": v(38.19, -3.23) * mm});
            skLineSegment(sketch, "E655", {"start": v(38.19, -3.23) * mm, "end": v(37.08, -4.08) * mm});
            skLineSegment(sketch, "E656", {"start": v(37.08, -4.08) * mm, "end": v(35.24, -3.96) * mm});
            skLineSegment(sketch, "E657", {"start": v(35.24, -3.96) * mm, "end": v(33.88, -6.56) * mm});
            skLineSegment(sketch, "E658", {"start": v(33.88, -6.56) * mm, "end": v(31.24, -9.37) * mm});
            skLineSegment(sketch, "E659", {"start": v(31.24, -9.37) * mm, "end": v(28.8, -10.73) * mm});
            skLineSegment(sketch, "E660", {"start": v(28.8, -10.73) * mm, "end": v(27.82, -11.25) * mm});
            skLineSegment(sketch, "E661", {"start": v(27.82, -11.25) * mm, "end": v(18.74, -11.25) * mm});
            skLineSegment(sketch, "E662", {"start": v(18.74, -11.25) * mm, "end": v(17.12, -10.14) * mm});
            skLineSegment(sketch, "E663", {"start": v(17.12, -10.14) * mm, "end": v(14.9, -8.18) * mm});
            skLineSegment(sketch, "E664", {"start": v(14.9, -8.18) * mm, "end": v(12.43, -6.43) * mm});
            skLineSegment(sketch, "E665", {"start": v(8.97, -3.36) * mm, "end": v(8.97, -2.12) * mm});
            skLineSegment(sketch, "E666", {"start": v(8.97, -2.12) * mm, "end": v(9.54, -1.97) * mm});
            skLineSegment(sketch, "E667", {"start": v(8.97, -3.36) * mm, "end": v(10.15, -3.7) * mm});
            skLineSegment(sketch, "E668", {"start": v(10.15, -3.7) * mm, "end": v(11.04, -5.42) * mm});
            skLineSegment(sketch, "E669", {"start": v(11.04, -5.42) * mm, "end": v(12.43, -6.43) * mm});
            skLineSegment(sketch, "E670", {"start": v(29.97, -4.2) * mm, "end": v(30.34, -3.05) * mm});
            skLineSegment(sketch, "E671", {"start": v(15.4, 3.88) * mm, "end": v(14.64, 2.97) * mm});
            skLineSegment(sketch, "E672", {"start": v(14.64, 2.97) * mm, "end": v(13.01, 2.48) * mm});
            skLineSegment(sketch, "E673", {"start": v(13.01, 2.48) * mm, "end": v(12.88, 1.4) * mm});
            skLineSegment(sketch, "E674", {"start": v(12.88, 1.4) * mm, "end": v(14.28, 0.72) * mm});
            skLineSegment(sketch, "E675", {"start": v(14.28, 0.72) * mm, "end": v(16, 1.53) * mm});
            skLineSegment(sketch, "E676", {"start": v(16, 1.53) * mm, "end": v(17.44, 3.7) * mm});
            skLineSegment(sketch, "E677", {"start": v(17.7, 5.37) * mm, "end": v(17.28, 5.85) * mm});
            skLineSegment(sketch, "E678", {"start": v(17.28, 5.85) * mm, "end": v(18.04, 6.53) * mm});
            skLineSegment(sketch, "E679", {"start": v(18.04, 6.53) * mm, "end": v(19.23, 6.7) * mm});
            skLineSegment(sketch, "E680", {"start": v(19.23, 6.7) * mm, "end": v(19.23, 11.74) * mm});
            skLineSegment(sketch, "E681", {"start": v(19.23, 11.74) * mm, "end": v(17.53, 13.32) * mm});
            skLineSegment(sketch, "E682", {"start": v(17.53, 13.32) * mm, "end": v(12.1, 13.73) * mm});
            skLineSegment(sketch, "E683", {"start": v(12.1, 13.73) * mm, "end": v(8.86, 11.87) * mm});
            skLineSegment(sketch, "E684", {"start": v(8.86, 11.87) * mm, "end": v(7.41, 10.52) * mm});
            skLineSegment(sketch, "E685", {"start": v(7.41, 10.52) * mm, "end": v(7.41, 9.12) * mm});
            skLineSegment(sketch, "E686", {"start": v(7.41, 9.12) * mm, "end": v(7.77, 7.18) * mm});
            skLineSegment(sketch, "E687", {"start": v(7.77, 7.18) * mm, "end": v(8.58, 5.64) * mm});
            skLineSegment(sketch, "E688", {"start": v(8.58, 5.64) * mm, "end": v(10.66, 4.96) * mm});
            skLineSegment(sketch, "E689", {"start": v(10.66, 4.96) * mm, "end": v(11.3, 4.06) * mm});
            skLineSegment(sketch, "E690", {"start": v(11.3, 4.06) * mm, "end": v(15.4, 3.88) * mm});
            skLineSegment(sketch, "E691", {"start": v(17.44, 3.7) * mm, "end": v(18, 4.57) * mm});
            skLineSegment(sketch, "E692", {"start": v(18, 4.57) * mm, "end": v(17.7, 5.37) * mm});
            skLineSegment(sketch, "E693", {"start": v(21.77, 6.56) * mm, "end": v(21.77, 3.87) * mm});
            skLineSegment(sketch, "E694", {"start": v(21.77, 3.87) * mm, "end": v(20.42, 3.4) * mm});
            skLineSegment(sketch, "E695", {"start": v(20.42, 3.4) * mm, "end": v(20.42, -0.9) * mm});
            skLineSegment(sketch, "E696", {"start": v(20.42, -0.9) * mm, "end": v(25.47, -0.9) * mm});
            skLineSegment(sketch, "E697", {"start": v(25.47, -0.9) * mm, "end": v(25.47, 3.2) * mm});
            skLineSegment(sketch, "E698", {"start": v(25.47, 3.2) * mm, "end": v(24.18, 4.2) * mm});
            skLineSegment(sketch, "E699", {"start": v(24.18, 4.2) * mm, "end": v(24.18, 6.5) * mm});
            skLineSegment(sketch, "E700", {"start": v(24.18, 6.5) * mm, "end": v(21.77, 6.56) * mm});
            skLineSegment(sketch, "E701", {"start": v(31.84, 2.77) * mm, "end": v(33.04, 2.31) * mm});
            skLineSegment(sketch, "E702", {"start": v(33.04, 2.31) * mm, "end": v(33.04, 1.18) * mm});
            skLineSegment(sketch, "E703", {"start": v(33.04, 1.18) * mm, "end": v(29.9, 1.18) * mm});
            skLineSegment(sketch, "E704", {"start": v(29.9, 1.18) * mm, "end": v(28.83, 2.31) * mm});
            skLineSegment(sketch, "E705", {"start": v(28.83, 2.31) * mm, "end": v(27.86, 3.22) * mm});
            skLineSegment(sketch, "E706", {"start": v(27.86, 3.22) * mm, "end": v(27.06, 4.36) * mm});
            skLineSegment(sketch, "E707", {"start": v(27.06, 4.36) * mm, "end": v(27.52, 5.61) * mm});
            skLineSegment(sketch, "E708", {"start": v(27.52, 5.61) * mm, "end": v(26.36, 6.04) * mm});
            skLineSegment(sketch, "E709", {"start": v(26.36, 6.04) * mm, "end": v(26.36, 11.65) * mm});
            skLineSegment(sketch, "E710", {"start": v(26.36, 11.65) * mm, "end": v(27.69, 13.58) * mm});
            skLineSegment(sketch, "E711", {"start": v(27.69, 13.58) * mm, "end": v(34.12, 13.58) * mm});
            skLineSegment(sketch, "E712", {"start": v(34.12, 13.58) * mm, "end": v(35.32, 12.67) * mm});
            skLineSegment(sketch, "E713", {"start": v(35.32, 12.67) * mm, "end": v(37.2, 12.05) * mm});
            skLineSegment(sketch, "E714", {"start": v(37.2, 12.05) * mm, "end": v(38.33, 10.5) * mm});
            skLineSegment(sketch, "E715", {"start": v(38.33, 10.5) * mm, "end": v(38.22, 6.87) * mm});
            skLineSegment(sketch, "E716", {"start": v(38.22, 6.87) * mm, "end": v(37.08, 5.73) * mm});
            skLineSegment(sketch, "E717", {"start": v(37.08, 5.73) * mm, "end": v(35.43, 5.05) * mm});
            skLineSegment(sketch, "E718", {"start": v(35.43, 5.05) * mm, "end": v(34.92, 3.85) * mm});
            skLineSegment(sketch, "E719", {"start": v(34.92, 3.85) * mm, "end": v(30.14, 3.85) * mm});
            skLineSegment(sketch, "E720", {"start": v(30.14, 3.85) * mm, "end": v(30.14, 2.88) * mm});
            skLineSegment(sketch, "E721", {"start": v(30.14, 2.88) * mm, "end": v(31.84, 2.77) * mm});
            skLineSegment(sketch, "E722", {"start": v(17.84, -14.9) * mm, "end": v(19.41, -14.9) * mm});
            skLineSegment(sketch, "E723", {"start": v(19.41, -14.9) * mm, "end": v(19.41, -16.16) * mm});
            skLineSegment(sketch, "E724", {"start": v(19.41, -16.16) * mm, "end": v(20.2, -16.88) * mm});
            skLineSegment(sketch, "E725", {"start": v(20.2, -16.88) * mm, "end": v(24.18, -16.88) * mm});
            skLineSegment(sketch, "E726", {"start": v(24.18, -16.88) * mm, "end": v(24.78, -16.4) * mm});
            skLineSegment(sketch, "E727", {"start": v(24.78, -16.4) * mm, "end": v(24.78, -15.07) * mm});
            skLineSegment(sketch, "E728", {"start": v(24.78, -15.07) * mm, "end": v(26.95, -15.07) * mm});
            skLineSegment(sketch, "E729", {"start": v(26.95, -15.07) * mm, "end": v(26.95, -17.73) * mm});
            skLineSegment(sketch, "E730", {"start": v(26.95, -17.73) * mm, "end": v(25.8, -18.57) * mm});
            skLineSegment(sketch, "E731", {"start": v(25.8, -18.57) * mm, "end": v(25.8, -21.22) * mm});
            skLineSegment(sketch, "E732", {"start": v(25.8, -21.22) * mm, "end": v(20.01, -21.22) * mm});
            skLineSegment(sketch, "E733", {"start": v(20.01, -21.22) * mm, "end": v(20.01, -19.9) * mm});
            skLineSegment(sketch, "E734", {"start": v(20.01, -19.9) * mm, "end": v(18.99, -19.05) * mm});
            skLineSegment(sketch, "E735", {"start": v(18.99, -19.05) * mm, "end": v(17.84, -17.73) * mm});
            skLineSegment(sketch, "E736", {"start": v(17.84, -17.73) * mm, "end": v(17.84, -14.9) * mm});
            skLineSegment(sketch, "E737", {"start": v(19.11, -22.8) * mm, "end": v(19.11, -37.51) * mm});
            skLineSegment(sketch, "E738", {"start": v(25.14, -37.51) * mm, "end": v(25.14, -24.91) * mm});
            skLineSegment(sketch, "E739", {"start": v(25.14, -24.91) * mm, "end": v(24.3, -24.85) * mm});
            skLineSegment(sketch, "E740", {"start": v(24.3, -24.85) * mm, "end": v(23.7, -24.55) * mm});
            skLineSegment(sketch, "E741", {"start": v(23.7, -24.55) * mm, "end": v(23.4, -23.28) * mm});
            skLineSegment(sketch, "E742", {"start": v(19.11, -22.8) * mm, "end": v(23.24, -22.8) * mm});
            skLineSegment(sketch, "E743", {"start": v(23.24, -22.8) * mm, "end": v(23.4, -23.28) * mm});
            skLineSegment(sketch, "E744", {"start": v(19.11, -37.51) * mm, "end": v(25.14, -37.51) * mm});
            skLineSegment(sketch, "E745", {"start": v(4.22, -7.85) * mm, "end": v(5.5, -10.22) * mm});
            skLineSegment(sketch, "E746", {"start": v(5.5, -10.22) * mm, "end": v(7.37, -12.23) * mm});
            skLineSegment(sketch, "E747", {"start": v(7.37, -12.23) * mm, "end": v(9.02, -12.73) * mm});
            skLineSegment(sketch, "E748", {"start": v(9.02, -12.73) * mm, "end": v(10.1, -14.6) * mm});
            skLineSegment(sketch, "E749", {"start": v(10.1, -14.6) * mm, "end": v(11.1, -15.6) * mm});
            skLineSegment(sketch, "E750", {"start": v(11.1, -15.6) * mm, "end": v(12.53, -16.39) * mm});
            skLineSegment(sketch, "E751", {"start": v(12.53, -16.39) * mm, "end": v(14.83, -17.18) * mm});
            skLineSegment(sketch, "E752", {"start": v(14.83, -17.18) * mm, "end": v(14.9, -18.04) * mm});
            skLineSegment(sketch, "E753", {"start": v(14.9, -18.04) * mm, "end": v(16.4, -18.47) * mm});
            skLineSegment(sketch, "E754", {"start": v(16.4, -18.47) * mm, "end": v(16.55, -19.76) * mm});
            skLineSegment(sketch, "E755", {"start": v(16.55, -19.76) * mm, "end": v(18.27, -19.9) * mm});
            skLineSegment(sketch, "E756", {"start": v(18.27, -19.9) * mm, "end": v(18.41, -20.9) * mm});
            skLineSegment(sketch, "E757", {"start": v(18.41, -20.9) * mm, "end": v(17.48, -21.34) * mm});
            skLineSegment(sketch, "E758", {"start": v(17.48, -21.34) * mm, "end": v(16.62, -21.62) * mm});
            skLineSegment(sketch, "E759", {"start": v(16.62, -21.62) * mm, "end": v(16.4, -24.2) * mm});
            skLineSegment(sketch, "E760", {"start": v(16.4, -24.2) * mm, "end": v(16.4, -26.07) * mm});
            skLineSegment(sketch, "E761", {"start": v(16.4, -26.07) * mm, "end": v(16.84, -26.43) * mm});
            skLineSegment(sketch, "E762", {"start": v(16.84, -26.43) * mm, "end": v(17.84, -26.64) * mm});
            skLineSegment(sketch, "E763", {"start": v(17.84, -26.64) * mm, "end": v(17.91, -27.72) * mm});
            skLineSegment(sketch, "E764", {"start": v(17.91, -27.72) * mm, "end": v(17.98, -31.6) * mm});
            skLineSegment(sketch, "E765", {"start": v(17.98, -31.6) * mm, "end": v(17.7, -34.03) * mm});
            skLineSegment(sketch, "E766", {"start": v(17.7, -34.03) * mm, "end": v(17.71, -38.42) * mm});
            skLineSegment(sketch, "E767", {"start": v(17.71, -38.42) * mm, "end": v(26.44, -38.78) * mm});
            skLineSegment(sketch, "E768", {"start": v(26.44, -38.78) * mm, "end": v(26.37, -24.5) * mm});
            skLineSegment(sketch, "E769", {"start": v(26.37, -24.5) * mm, "end": v(28.02, -23.77) * mm});
            skLineSegment(sketch, "E770", {"start": v(28.02, -23.77) * mm, "end": v(27.95, -21.4) * mm});
            skLineSegment(sketch, "E771", {"start": v(27.95, -21.4) * mm, "end": v(27.02, -21.26) * mm});
            skLineSegment(sketch, "E772", {"start": v(27.02, -21.26) * mm, "end": v(26.8, -19.9) * mm});
            skLineSegment(sketch, "E773", {"start": v(26.8, -19.9) * mm, "end": v(28.02, -19.97) * mm});
            skLineSegment(sketch, "E774", {"start": v(28.02, -19.97) * mm, "end": v(28.67, -18.97) * mm});
            skLineSegment(sketch, "E775", {"start": v(28.67, -18.97) * mm, "end": v(31.54, -18.25) * mm});
            skLineSegment(sketch, "E776", {"start": v(31.54, -18.25) * mm, "end": v(33.11, -16.6) * mm});
            skLineSegment(sketch, "E777", {"start": v(33.11, -16.6) * mm, "end": v(35.77, -15.1) * mm});
            skLineSegment(sketch, "E778", {"start": v(35.77, -15.1) * mm, "end": v(37.63, -12.95) * mm});
            skLineSegment(sketch, "E779", {"start": v(37.63, -12.95) * mm, "end": v(37.92, -11.37) * mm});
            skLineSegment(sketch, "E780", {"start": v(37.92, -11.37) * mm, "end": v(40.72, -8.93) * mm});
            skLineSegment(sketch, "E781", {"start": v(40.72, -8.93) * mm, "end": v(41.43, -6.85) * mm});
            skLineSegment(sketch, "E782", {"start": v(41.43, -6.85) * mm, "end": v(41.58, -4.05) * mm});
            skLineSegment(sketch, "E783", {"start": v(41.58, -4.05) * mm, "end": v(44.73, -3.77) * mm});
            skLineSegment(sketch, "E784", {"start": v(44.73, -3.77) * mm, "end": v(44.59, -7.5) * mm});
            skLineSegment(sketch, "E785", {"start": v(44.59, -7.5) * mm, "end": v(45.74, -8.64) * mm});
            skLineSegment(sketch, "E786", {"start": v(45.74, -8.64) * mm, "end": v(45.52, -9.65) * mm});
            skLineSegment(sketch, "E787", {"start": v(45.52, -9.65) * mm, "end": v(43.94, -9.8) * mm});
            skLineSegment(sketch, "E788", {"start": v(43.94, -9.8) * mm, "end": v(43.58, -10.36) * mm});
            skLineSegment(sketch, "E789", {"start": v(43.58, -10.36) * mm, "end": v(46.3, -12.73) * mm});
            skLineSegment(sketch, "E790", {"start": v(46.3, -12.73) * mm, "end": v(48.6, -16.46) * mm});
            skLineSegment(sketch, "E791", {"start": v(48.6, -16.46) * mm, "end": v(49.25, -18.9) * mm});
            skLineSegment(sketch, "E792", {"start": v(49.25, -18.9) * mm, "end": v(50.4, -21.34) * mm});
            skLineSegment(sketch, "E793", {"start": v(50.4, -21.34) * mm, "end": v(51.83, -24.06) * mm});
            skLineSegment(sketch, "E794", {"start": v(51.83, -24.06) * mm, "end": v(52.65, -25.59) * mm});
            skLineSegment(sketch, "E795", {"start": v(52.65, -25.59) * mm, "end": v(52.55, -34.82) * mm});
            skLineSegment(sketch, "E796", {"start": v(52.55, -34.82) * mm, "end": v(50.76, -35.96) * mm});
            skLineSegment(sketch, "E797", {"start": v(50.76, -35.96) * mm, "end": v(49.47, -37.83) * mm});
            skLineSegment(sketch, "E798", {"start": v(49.47, -37.83) * mm, "end": v(46.6, -41.13) * mm});
            skLineSegment(sketch, "E799", {"start": v(46.6, -41.13) * mm, "end": v(43.8, -41.7) * mm});
            skLineSegment(sketch, "E800", {"start": v(43.8, -41.7) * mm, "end": v(43.01, -40.34) * mm});
            skLineSegment(sketch, "E801", {"start": v(43.01, -40.34) * mm, "end": v(40.86, -41.06) * mm});
            skLineSegment(sketch, "E802", {"start": v(40.86, -41.06) * mm, "end": v(38.56, -41.92) * mm});
            skLineSegment(sketch, "E803", {"start": v(38.56, -41.92) * mm, "end": v(32.68, -41.56) * mm});
            skLineSegment(sketch, "E804", {"start": v(32.68, -41.56) * mm, "end": v(28.81, -41.92) * mm});
            skLineSegment(sketch, "E805", {"start": v(28.81, -41.92) * mm, "end": v(27.66, -41.92) * mm});
            skLineSegment(sketch, "E806", {"start": v(27.66, -41.92) * mm, "end": v(26.8, -40.7) * mm});
            skLineSegment(sketch, "E807", {"start": v(26.8, -40.7) * mm, "end": v(21.78, -40.84) * mm});
            skLineSegment(sketch, "E808", {"start": v(21.78, -40.84) * mm, "end": v(20.35, -41.56) * mm});
            skLineSegment(sketch, "E809", {"start": v(20.35, -41.56) * mm, "end": v(19.63, -42.63) * mm});
            skLineSegment(sketch, "E810", {"start": v(19.63, -42.63) * mm, "end": v(15.19, -42.7) * mm});
            skLineSegment(sketch, "E811", {"start": v(15.19, -42.7) * mm, "end": v(13.6, -44) * mm});
            skLineSegment(sketch, "E812", {"start": v(13.6, -44) * mm, "end": v(3.35, -43.57) * mm});
            skLineSegment(sketch, "E813", {"start": v(3.35, -43.57) * mm, "end": v(2.5, -42.35) * mm});
            skLineSegment(sketch, "E814", {"start": v(2.5, -42.35) * mm, "end": v(0.99, -42.13) * mm});
            skLineSegment(sketch, "E815", {"start": v(0.99, -42.13) * mm, "end": v(-2.45, -39.55) * mm});
            skLineSegment(sketch, "E816", {"start": v(-2.45, -39.55) * mm, "end": v(-4.96, -36.32) * mm});
            skLineSegment(sketch, "E817", {"start": v(-4.96, -36.32) * mm, "end": v(-6.9, -33.45) * mm});
            skLineSegment(sketch, "E818", {"start": v(-6.9, -33.45) * mm, "end": v(-8.7, -31.66) * mm});
            skLineSegment(sketch, "E819", {"start": v(-8.7, -31.66) * mm, "end": v(-8.7, -28.08) * mm});
            skLineSegment(sketch, "E820", {"start": v(-8.7, -28.08) * mm, "end": v(-7.47, -23.99) * mm});
            skLineSegment(sketch, "E821", {"start": v(-7.47, -23.99) * mm, "end": v(-5.32, -20.19) * mm});
            skLineSegment(sketch, "E822", {"start": v(-5.32, -20.19) * mm, "end": v(-4.9, -17.97) * mm});
            skLineSegment(sketch, "E823", {"start": v(-4.9, -17.97) * mm, "end": v(-2.41, -17.03) * mm});
            skLineSegment(sketch, "E824", {"start": v(-2.41, -17.03) * mm, "end": v(-2.41, -15.02) * mm});
            skLineSegment(sketch, "E825", {"start": v(-2.41, -15.02) * mm, "end": v(-1.45, -12.66) * mm});
            skLineSegment(sketch, "E826", {"start": v(-1.45, -12.66) * mm, "end": v(-0.52, -10.5) * mm});
            skLineSegment(sketch, "E827", {"start": v(-0.52, -10.5) * mm, "end": v(0.85, -8.64) * mm});
            skLineSegment(sketch, "E828", {"start": v(0.85, -8.64) * mm, "end": v(0.99, -7.93) * mm});
            skLineSegment(sketch, "E829", {"start": v(0.99, -7.93) * mm, "end": v(4.22, -7.85) * mm});
            skLineSegment(sketch, "E830", {"start": v(1.78, -13.32) * mm, "end": v(5.69, -14.32) * mm});
            skLineSegment(sketch, "E831", {"start": v(5.69, -14.32) * mm, "end": v(9.65, -16.88) * mm});
            skLineSegment(sketch, "E832", {"start": v(9.65, -16.88) * mm, "end": v(11.56, -19.3) * mm});
            skLineSegment(sketch, "E833", {"start": v(11.56, -19.3) * mm, "end": v(11.46, -25.49) * mm});
            skLineSegment(sketch, "E834", {"start": v(11.46, -25.49) * mm, "end": v(8.24, -25.44) * mm});
            skLineSegment(sketch, "E835", {"start": v(8.24, -25.44) * mm, "end": v(7, -27.16) * mm});
            skLineSegment(sketch, "E836", {"start": v(7, -27.16) * mm, "end": v(4.8, -27.9) * mm});
            skLineSegment(sketch, "E837", {"start": v(4.8, -27.9) * mm, "end": v(4.46, -25.97) * mm});
            skLineSegment(sketch, "E838", {"start": v(4.46, -25.97) * mm, "end": v(4.55, -18.5) * mm});
            skLineSegment(sketch, "E839", {"start": v(4.55, -18.5) * mm, "end": v(3.78, -18.46) * mm});
            skLineSegment(sketch, "E840", {"start": v(3.78, -18.46) * mm, "end": v(3.62, -28.6) * mm});
            skLineSegment(sketch, "E841", {"start": v(3.62, -28.6) * mm, "end": v(1.85, -29.79) * mm});
            skLineSegment(sketch, "E842", {"start": v(1.85, -29.79) * mm, "end": v(1.85, -39.5) * mm});
            skLineSegment(sketch, "E843", {"start": v(1.85, -39.5) * mm, "end": v(-0.1, -39.16) * mm});
            skLineSegment(sketch, "E844", {"start": v(-0.1, -39.16) * mm, "end": v(-0.2, -36.05) * mm});
            skLineSegment(sketch, "E845", {"start": v(-0.2, -36.05) * mm, "end": v(-1.98, -36.05) * mm});
            skLineSegment(sketch, "E846", {"start": v(-1.98, -36.05) * mm, "end": v(-5.94, -31.2) * mm});
            skLineSegment(sketch, "E847", {"start": v(-5.94, -31.2) * mm, "end": v(-6.33, -25.31) * mm});
            skLineSegment(sketch, "E848", {"start": v(-6.33, -25.31) * mm, "end": v(-3.19, -19.02) * mm});
            skLineSegment(sketch, "E849", {"start": v(-3.19, -19.02) * mm, "end": v(0, -15.02) * mm});
            skLineSegment(sketch, "E850", {"start": v(0, -15.02) * mm, "end": v(1.78, -13.32) * mm});
            skLineSegment(sketch, "E851", {"start": v(3.79, -30.34) * mm, "end": v(3.79, -38.96) * mm});
            skLineSegment(sketch, "E852", {"start": v(3.79, -38.96) * mm, "end": v(5.48, -39.04) * mm});
            skLineSegment(sketch, "E853", {"start": v(5.48, -39.04) * mm, "end": v(7.25, -41.53) * mm});
            skLineSegment(sketch, "E854", {"start": v(7.25, -41.53) * mm, "end": v(13.69, -41.53) * mm});
            skLineSegment(sketch, "E855", {"start": v(13.69, -41.53) * mm, "end": v(13.69, -35.1) * mm});
            skLineSegment(sketch, "E856", {"start": v(13.69, -35.1) * mm, "end": v(12.48, -34.29) * mm});
            skLineSegment(sketch, "E857", {"start": v(12.48, -34.29) * mm, "end": v(12.56, -27.53) * mm});
            skLineSegment(sketch, "E858", {"start": v(12.56, -27.53) * mm, "end": v(8.7, -27.6) * mm});
            skLineSegment(sketch, "E859", {"start": v(8.7, -27.6) * mm, "end": v(7.4, -29.05) * mm});
            skLineSegment(sketch, "E860", {"start": v(7.4, -29.05) * mm, "end": v(6.04, -29.78) * mm});
            skLineSegment(sketch, "E861", {"start": v(6.04, -29.78) * mm, "end": v(3.79, -30.34) * mm});
            skLineSegment(sketch, "E862", {"start": v(13.11, -19.96) * mm, "end": v(13.11, -23.88) * mm});
            skLineSegment(sketch, "E863", {"start": v(13.11, -23.88) * mm, "end": v(15.58, -23.94) * mm});
            skLineSegment(sketch, "E864", {"start": v(15.58, -23.94) * mm, "end": v(15.58, -20.02) * mm});
            skLineSegment(sketch, "E865", {"start": v(15.58, -20.02) * mm, "end": v(13.11, -19.96) * mm});
            skLineSegment(sketch, "E866", {"start": v(12.95, -26.09) * mm, "end": v(12.95, -27.12) * mm});
            skLineSegment(sketch, "E867", {"start": v(12.95, -27.12) * mm, "end": v(14.03, -27.2) * mm});
            skLineSegment(sketch, "E868", {"start": v(14.03, -27.2) * mm, "end": v(14.4, -27.68) * mm});
            skLineSegment(sketch, "E869", {"start": v(14.4, -27.68) * mm, "end": v(14.3, -30.1) * mm});
            skLineSegment(sketch, "E870", {"start": v(14.3, -30.1) * mm, "end": v(16.41, -30.1) * mm});
            skLineSegment(sketch, "E871", {"start": v(16.41, -30.1) * mm, "end": v(16.56, -27.42) * mm});
            skLineSegment(sketch, "E872", {"start": v(16.56, -27.42) * mm, "end": v(15.37, -27.35) * mm});
            skLineSegment(sketch, "E873", {"start": v(15.37, -27.35) * mm, "end": v(14.84, -26.97) * mm});
            skLineSegment(sketch, "E874", {"start": v(14.84, -26.97) * mm, "end": v(14.66, -25.4) * mm});
            skLineSegment(sketch, "E875", {"start": v(14.66, -25.4) * mm, "end": v(12.91, -25.4) * mm});
            skLineSegment(sketch, "E876", {"start": v(12.91, -25.4) * mm, "end": v(12.95, -26.09) * mm});
            skLineSegment(sketch, "E877", {"start": v(14.33, -31.97) * mm, "end": v(14.33, -33.94) * mm});
            skLineSegment(sketch, "E878", {"start": v(14.33, -33.94) * mm, "end": v(15.43, -33.94) * mm});
            skLineSegment(sketch, "E879", {"start": v(15.43, -33.94) * mm, "end": v(15.67, -33.38) * mm});
            skLineSegment(sketch, "E880", {"start": v(15.67, -33.38) * mm, "end": v(16.8, -33.4) * mm});
            skLineSegment(sketch, "E881", {"start": v(16.8, -33.4) * mm, "end": v(16.72, -30.66) * mm});
            skLineSegment(sketch, "E882", {"start": v(16.72, -30.66) * mm, "end": v(16.1, -30.58) * mm});
            skLineSegment(sketch, "E883", {"start": v(16.1, -30.58) * mm, "end": v(15.57, -31.4) * mm});
            skLineSegment(sketch, "E884", {"start": v(15.57, -31.4) * mm, "end": v(14.83, -31.97) * mm});
            skLineSegment(sketch, "E885", {"start": v(14.83, -31.97) * mm, "end": v(14.33, -31.97) * mm});
            skLineSegment(sketch, "E886", {"start": v(15.12, -35.6) * mm, "end": v(15.12, -38.78) * mm});
            skLineSegment(sketch, "E887", {"start": v(15.12, -38.78) * mm, "end": v(16.9, -38.75) * mm});
            skLineSegment(sketch, "E888", {"start": v(16.9, -38.75) * mm, "end": v(16.83, -34.82) * mm});
            skLineSegment(sketch, "E889", {"start": v(16.83, -34.82) * mm, "end": v(15.45, -34.85) * mm});
            skLineSegment(sketch, "E890", {"start": v(15.45, -34.85) * mm, "end": v(15.12, -35.6) * mm});
            skLineSegment(sketch, "E891", {"start": v(31.22, -32.46) * mm, "end": v(32.7, -32.46) * mm});
            skLineSegment(sketch, "E892", {"start": v(32.7, -32.46) * mm, "end": v(33.5, -28.66) * mm});
            skLineSegment(sketch, "E893", {"start": v(33.5, -28.66) * mm, "end": v(34.83, -27.25) * mm});
            skLineSegment(sketch, "E894", {"start": v(34.83, -27.25) * mm, "end": v(36.5, -26.04) * mm});
            skLineSegment(sketch, "E895", {"start": v(36.5, -26.04) * mm, "end": v(38.94, -24.33) * mm});
            skLineSegment(sketch, "E896", {"start": v(38.94, -24.33) * mm, "end": v(40.66, -23.2) * mm});
            skLineSegment(sketch, "E897", {"start": v(40.66, -23.2) * mm, "end": v(41.02, -18.77) * mm});
            skLineSegment(sketch, "E898", {"start": v(41.02, -18.77) * mm, "end": v(42.51, -17.05) * mm});
            skLineSegment(sketch, "E899", {"start": v(42.51, -17.05) * mm, "end": v(43.19, -17.46) * mm});
            skLineSegment(sketch, "E900", {"start": v(43.19, -17.46) * mm, "end": v(41.74, -19.13) * mm});
            skLineSegment(sketch, "E901", {"start": v(41.74, -19.13) * mm, "end": v(41.6, -23.56) * mm});
            skLineSegment(sketch, "E902", {"start": v(41.6, -23.56) * mm, "end": v(42.47, -28.26) * mm});
            skLineSegment(sketch, "E903", {"start": v(42.47, -28.26) * mm, "end": v(43.33, -28.8) * mm});
            skLineSegment(sketch, "E904", {"start": v(43.33, -28.8) * mm, "end": v(43.33, -38.26) * mm});
            skLineSegment(sketch, "E905", {"start": v(43.33, -38.26) * mm, "end": v(44.48, -39) * mm});
            skLineSegment(sketch, "E906", {"start": v(44.48, -39) * mm, "end": v(45.83, -38.87) * mm});
            skLineSegment(sketch, "E907", {"start": v(45.83, -38.87) * mm, "end": v(47.39, -37.72) * mm});
            skLineSegment(sketch, "E908", {"start": v(47.39, -37.72) * mm, "end": v(48.06, -36.3) * mm});
            skLineSegment(sketch, "E909", {"start": v(48.06, -36.3) * mm, "end": v(47.72, -35.7) * mm});
            skLineSegment(sketch, "E910", {"start": v(47.72, -35.7) * mm, "end": v(48.2, -34.47) * mm});
            skLineSegment(sketch, "E911", {"start": v(48.2, -34.47) * mm, "end": v(49.35, -33.46) * mm});
            skLineSegment(sketch, "E912", {"start": v(49.35, -33.46) * mm, "end": v(50.77, -33.52) * mm});
            skLineSegment(sketch, "E913", {"start": v(50.77, -33.52) * mm, "end": v(50.77, -31.63) * mm});
            skLineSegment(sketch, "E914", {"start": v(50.77, -31.63) * mm, "end": v(50.7, -28.92) * mm});
            skLineSegment(sketch, "E915", {"start": v(50.7, -28.92) * mm, "end": v(50.64, -27.7) * mm});
            skLineSegment(sketch, "E916", {"start": v(50.64, -27.7) * mm, "end": v(49.01, -27.3) * mm});
            skLineSegment(sketch, "E917", {"start": v(49.01, -27.3) * mm, "end": v(49.08, -25.4) * mm});
            skLineSegment(sketch, "E918", {"start": v(49.08, -25.4) * mm, "end": v(48.8, -23.5) * mm});
            skLineSegment(sketch, "E919", {"start": v(48.8, -23.5) * mm, "end": v(47.93, -22.83) * mm});
            skLineSegment(sketch, "E920", {"start": v(47.93, -22.83) * mm, "end": v(47.66, -21.48) * mm});
            skLineSegment(sketch, "E921", {"start": v(47.66, -21.48) * mm, "end": v(47.25, -19.99) * mm});
            skLineSegment(sketch, "E922", {"start": v(47.25, -19.99) * mm, "end": v(46.91, -18.5) * mm});
            skLineSegment(sketch, "E923", {"start": v(46.91, -18.5) * mm, "end": v(46.17, -16.87) * mm});
            skLineSegment(sketch, "E924", {"start": v(46.17, -16.87) * mm, "end": v(44.75, -15.38) * mm});
            skLineSegment(sketch, "E925", {"start": v(44.75, -15.38) * mm, "end": v(43.93, -13.62) * mm});
            skLineSegment(sketch, "E926", {"start": v(43.93, -13.62) * mm, "end": v(42.78, -12.2) * mm});
            skLineSegment(sketch, "E927", {"start": v(42.78, -12.2) * mm, "end": v(41.77, -12) * mm});
            skLineSegment(sketch, "E928", {"start": v(41.77, -12) * mm, "end": v(40.89, -13.42) * mm});
            skLineSegment(sketch, "E929", {"start": v(40.89, -13.42) * mm, "end": v(39.74, -14.84) * mm});
            skLineSegment(sketch, "E930", {"start": v(39.74, -14.84) * mm, "end": v(38.59, -16.74) * mm});
            skLineSegment(sketch, "E931", {"start": v(38.59, -16.74) * mm, "end": v(37.1, -18.3) * mm});
            skLineSegment(sketch, "E932", {"start": v(37.1, -18.3) * mm, "end": v(34.86, -18.77) * mm});
            skLineSegment(sketch, "E933", {"start": v(34.86, -18.77) * mm, "end": v(33.71, -19.65) * mm});
            skLineSegment(sketch, "E934", {"start": v(33.71, -19.65) * mm, "end": v(31.62, -20.33) * mm});
            skLineSegment(sketch, "E935", {"start": v(31.62, -20.33) * mm, "end": v(31.14, -21.4) * mm});
            skLineSegment(sketch, "E936", {"start": v(31.14, -21.4) * mm, "end": v(31.22, -32.46) * mm});
            skLineSegment(sketch, "E937", {"start": v(30.3, -39.66) * mm, "end": v(31.08, -37.58) * mm});
            skLineSegment(sketch, "E938", {"start": v(31.08, -37.58) * mm, "end": v(32.59, -35.93) * mm});
            skLineSegment(sketch, "E939", {"start": v(32.59, -35.93) * mm, "end": v(33.38, -33.78) * mm});
            skLineSegment(sketch, "E940", {"start": v(33.38, -33.78) * mm, "end": v(33.98, -31.18) * mm});
            skLineSegment(sketch, "E941", {"start": v(33.98, -31.18) * mm, "end": v(34.53, -29.2) * mm});
            skLineSegment(sketch, "E942", {"start": v(34.53, -29.2) * mm, "end": v(36.17, -27.54) * mm});
            skLineSegment(sketch, "E943", {"start": v(36.17, -27.54) * mm, "end": v(38.68, -26.04) * mm});
            skLineSegment(sketch, "E944", {"start": v(38.68, -26.04) * mm, "end": v(40.48, -25.18) * mm});
            skLineSegment(sketch, "E945", {"start": v(40.48, -25.18) * mm, "end": v(40.62, -30.12) * mm});
            skLineSegment(sketch, "E946", {"start": v(40.62, -30.12) * mm, "end": v(41.62, -31.34) * mm});
            skLineSegment(sketch, "E947", {"start": v(41.62, -31.34) * mm, "end": v(41.62, -37.15) * mm});
            skLineSegment(sketch, "E948", {"start": v(41.62, -37.15) * mm, "end": v(40.7, -38.8) * mm});
            skLineSegment(sketch, "E949", {"start": v(40.7, -38.8) * mm, "end": v(39.47, -39.95) * mm});
            skLineSegment(sketch, "E950", {"start": v(39.47, -39.95) * mm, "end": v(30.87, -40.23) * mm});
            skLineSegment(sketch, "E951", {"start": v(30.87, -40.23) * mm, "end": v(30.3, -39.66) * mm});
            skLineSegment(sketch, "E952.bottom", {"start": v(28.71, -21.41) * mm, "end": v(30.22, -21.41) * mm});
            skLineSegment(sketch, "E952.top", {"start": v(28.71, -24) * mm, "end": v(30.22, -24) * mm});
            skLineSegment(sketch, "E952.left", {"start": v(28.71, -21.41) * mm, "end": v(28.71, -24) * mm});
            skLineSegment(sketch, "E952.right", {"start": v(30.22, -21.41) * mm, "end": v(30.22, -24) * mm});
            skLineSegment(sketch, "E953.bottom", {"start": v(27.36, -34.55) * mm, "end": v(29.23, -34.55) * mm});
            skLineSegment(sketch, "E953.top", {"start": v(27.36, -39.2) * mm, "end": v(29.23, -39.2) * mm});
            skLineSegment(sketch, "E953.left", {"start": v(27.36, -34.55) * mm, "end": v(27.36, -39.2) * mm});
            skLineSegment(sketch, "E953.right", {"start": v(29.23, -34.55) * mm, "end": v(29.23, -39.2) * mm});
            skLineSegment(sketch, "E954", {"start": v(27.72, -26.23) * mm, "end": v(27.73, -28.94) * mm});
            skLineSegment(sketch, "E955", {"start": v(27.73, -28.94) * mm, "end": v(30.01, -29.12) * mm});
            skLineSegment(sketch, "E956", {"start": v(30.01, -29.12) * mm, "end": v(29.95, -25.14) * mm});
            skLineSegment(sketch, "E957", {"start": v(29.95, -25.14) * mm, "end": v(27.72, -26.23) * mm});
            skLineSegment(sketch, "E958", {"start": v(27.54, -30.09) * mm, "end": v(27.54, -33.1) * mm});
            skLineSegment(sketch, "E959", {"start": v(27.54, -33.1) * mm, "end": v(29.54, -33.26) * mm});
            skLineSegment(sketch, "E960", {"start": v(29.54, -33.26) * mm, "end": v(29.92, -33.45) * mm});
            skLineSegment(sketch, "E961", {"start": v(29.92, -33.45) * mm, "end": v(29.83, -35.94) * mm});
            skLineSegment(sketch, "E962", {"start": v(29.83, -35.94) * mm, "end": v(31.4, -36.06) * mm});
            skLineSegment(sketch, "E963", {"start": v(31.4, -36.06) * mm, "end": v(31.52, -33.29) * mm});
            skLineSegment(sketch, "E964", {"start": v(31.52, -33.29) * mm, "end": v(30.25, -32.62) * mm});
            skLineSegment(sketch, "E965", {"start": v(30.25, -32.62) * mm, "end": v(30.13, -30.21) * mm});
            skLineSegment(sketch, "E966", {"start": v(30.13, -30.21) * mm, "end": v(27.54, -30.09) * mm});
            skLineSegment(sketch, "E967", {"start": v(7.75, -45.8) * mm, "end": v(9.85, -45.8) * mm});
            skLineSegment(sketch, "E968", {"start": v(9.85, -45.8) * mm, "end": v(9.66, -47.8) * mm});
            skLineSegment(sketch, "E969", {"start": v(9.66, -47.8) * mm, "end": v(8.6, -49.14) * mm});
            skLineSegment(sketch, "E970", {"start": v(8.6, -49.14) * mm, "end": v(8.33, -55.16) * mm});
            skLineSegment(sketch, "E971", {"start": v(8.33, -55.16) * mm, "end": v(7.17, -56.03) * mm});
            skLineSegment(sketch, "E972", {"start": v(7.17, -56.03) * mm, "end": v(7.36, -62.16) * mm});
            skLineSegment(sketch, "E973", {"start": v(7.36, -62.16) * mm, "end": v(9.09, -61.97) * mm});
            skLineSegment(sketch, "E974", {"start": v(9.09, -61.97) * mm, "end": v(9.18, -56.7) * mm});
            skLineSegment(sketch, "E975", {"start": v(9.18, -56.7) * mm, "end": v(10.52, -54.79) * mm});
            skLineSegment(sketch, "E976", {"start": v(10.52, -54.79) * mm, "end": v(10.43, -49.62) * mm});
            skLineSegment(sketch, "E977", {"start": v(10.43, -49.62) * mm, "end": v(12.44, -47.13) * mm});
            skLineSegment(sketch, "E978", {"start": v(12.44, -47.13) * mm, "end": v(13.97, -48.37) * mm});
            skLineSegment(sketch, "E979", {"start": v(13.97, -48.37) * mm, "end": v(12.72, -49.81) * mm});
            skLineSegment(sketch, "E980", {"start": v(12.72, -49.81) * mm, "end": v(13.1, -55.17) * mm});
            skLineSegment(sketch, "E981", {"start": v(13.1, -55.17) * mm, "end": v(11.86, -56.7) * mm});
            skLineSegment(sketch, "E982", {"start": v(11.86, -56.7) * mm, "end": v(11.96, -62.25) * mm});
            skLineSegment(sketch, "E983", {"start": v(11.96, -62.25) * mm, "end": v(12.72, -63.7) * mm});
            skLineSegment(sketch, "E984", {"start": v(12.72, -63.7) * mm, "end": v(22.58, -63.79) * mm});
            skLineSegment(sketch, "E985", {"start": v(22.58, -63.79) * mm, "end": v(22.97, -56.6) * mm});
            skLineSegment(sketch, "E986", {"start": v(22.97, -56.6) * mm, "end": v(24.21, -56.42) * mm});
            skLineSegment(sketch, "E987", {"start": v(24.21, -56.42) * mm, "end": v(24.4, -50.48) * mm});
            skLineSegment(sketch, "E988", {"start": v(24.4, -50.48) * mm, "end": v(25.93, -49.14) * mm});
            skLineSegment(sketch, "E989", {"start": v(25.93, -49.14) * mm, "end": v(27.94, -50.86) * mm});
            skLineSegment(sketch, "E990", {"start": v(27.94, -50.86) * mm, "end": v(27.94, -54.02) * mm});
            skLineSegment(sketch, "E991", {"start": v(27.94, -54.02) * mm, "end": v(29.57, -55.65) * mm});
            skLineSegment(sketch, "E992", {"start": v(29.57, -55.65) * mm, "end": v(29.38, -63.21) * mm});
            skLineSegment(sketch, "E993", {"start": v(29.38, -63.21) * mm, "end": v(35.89, -63.21) * mm});
            skLineSegment(sketch, "E994", {"start": v(35.89, -63.21) * mm, "end": v(36.08, -59.38) * mm});
            skLineSegment(sketch, "E995", {"start": v(36.08, -59.38) * mm, "end": v(34.55, -57.95) * mm});
            skLineSegment(sketch, "E996", {"start": v(34.55, -57.95) * mm, "end": v(34.74, -44.64) * mm});
            skLineSegment(sketch, "E997", {"start": v(34.74, -44.64) * mm, "end": v(37.61, -44.74) * mm});
            skLineSegment(sketch, "E998", {"start": v(37.61, -44.74) * mm, "end": v(37.61, -51.73) * mm});
            skLineSegment(sketch, "E999", {"start": v(37.61, -51.73) * mm, "end": v(39.34, -53.16) * mm});
            skLineSegment(sketch, "E1000", {"start": v(39.34, -53.16) * mm, "end": v(38.57, -62.06) * mm});
            skLineSegment(sketch, "E1001", {"start": v(38.57, -62.06) * mm, "end": v(40.2, -63.5) * mm});
            skLineSegment(sketch, "E1002", {"start": v(40.2, -63.5) * mm, "end": v(42.02, -62.45) * mm});
            skLineSegment(sketch, "E1003", {"start": v(42.02, -62.45) * mm, "end": v(45.56, -62.35) * mm});
            skLineSegment(sketch, "E1004", {"start": v(45.56, -62.35) * mm, "end": v(45.56, -55.08) * mm});
            skLineSegment(sketch, "E1005", {"start": v(45.56, -55.08) * mm, "end": v(44.6, -54.02) * mm});
            skLineSegment(sketch, "E1006", {"start": v(44.6, -54.02) * mm, "end": v(44.4, -49.24) * mm});
            skLineSegment(sketch, "E1007", {"start": v(44.4, -49.24) * mm, "end": v(43.36, -46.27) * mm});
            skLineSegment(sketch, "E1008", {"start": v(43.36, -46.27) * mm, "end": v(43.74, -44.64) * mm});
            skLineSegment(sketch, "E1009", {"start": v(43.74, -44.64) * mm, "end": v(45.46, -44.74) * mm});
            skLineSegment(sketch, "E1010", {"start": v(45.46, -44.74) * mm, "end": v(45.46, -47.03) * mm});
            skLineSegment(sketch, "E1011", {"start": v(45.46, -47.03) * mm, "end": v(46.42, -48.57) * mm});
            skLineSegment(sketch, "E1012", {"start": v(46.42, -48.57) * mm, "end": v(46.32, -52.59) * mm});
            skLineSegment(sketch, "E1013", {"start": v(46.32, -52.59) * mm, "end": v(47.28, -54.12) * mm});
            skLineSegment(sketch, "E1014", {"start": v(47.28, -54.12) * mm, "end": v(47.28, -64.26) * mm});
            skLineSegment(sketch, "E1015", {"start": v(47.28, -64.26) * mm, "end": v(43.07, -64.07) * mm});
            skLineSegment(sketch, "E1016", {"start": v(43.07, -64.07) * mm, "end": v(41.92, -65.9) * mm});
            skLineSegment(sketch, "E1017", {"start": v(41.92, -65.9) * mm, "end": v(29, -66.18) * mm});
            skLineSegment(sketch, "E1018", {"start": v(29, -66.18) * mm, "end": v(27.66, -63.88) * mm});
            skLineSegment(sketch, "E1019", {"start": v(27.66, -63.88) * mm, "end": v(27.66, -56.22) * mm});
            skLineSegment(sketch, "E1020", {"start": v(27.66, -56.22) * mm, "end": v(26.5, -55.08) * mm});
            skLineSegment(sketch, "E1021", {"start": v(26.5, -55.08) * mm, "end": v(26.6, -51.25) * mm});
            skLineSegment(sketch, "E1022", {"start": v(26.6, -51.25) * mm, "end": v(25.63, -51.22) * mm});
            skLineSegment(sketch, "E1023", {"start": v(25.63, -51.22) * mm, "end": v(25.38, -58.34) * mm});
            skLineSegment(sketch, "E1024", {"start": v(25.38, -58.34) * mm, "end": v(24.42, -58.64) * mm});
            skLineSegment(sketch, "E1025", {"start": v(24.42, -58.64) * mm, "end": v(24.18, -64.3) * mm});
            skLineSegment(sketch, "E1026", {"start": v(24.18, -64.3) * mm, "end": v(22.19, -65.87) * mm});
            skLineSegment(sketch, "E1027", {"start": v(22.19, -65.87) * mm, "end": v(11.7, -65.57) * mm});
            skLineSegment(sketch, "E1028", {"start": v(11.7, -65.57) * mm, "end": v(10.66, -64.13) * mm});
            skLineSegment(sketch, "E1029", {"start": v(10.66, -64.13) * mm, "end": v(6.2, -64.03) * mm});
            skLineSegment(sketch, "E1030", {"start": v(6.2, -64.03) * mm, "end": v(5.6, -62.56) * mm});
            skLineSegment(sketch, "E1031", {"start": v(5.6, -62.56) * mm, "end": v(5.55, -55.5) * mm});
            skLineSegment(sketch, "E1032", {"start": v(5.55, -55.5) * mm, "end": v(6.57, -54.42) * mm});
            skLineSegment(sketch, "E1033", {"start": v(6.57, -54.42) * mm, "end": v(6.63, -47.9) * mm});
            skLineSegment(sketch, "E1034", {"start": v(6.63, -47.9) * mm, "end": v(7.75, -45.8) * mm});
            skLineSegment(sketch, "E1035", {"start": v(2.25, -75.54) * mm, "end": v(2.25, -71.7) * mm});
            skLineSegment(sketch, "E1036", {"start": v(2.25, -71.7) * mm, "end": v(4.8, -68.32) * mm});
            skLineSegment(sketch, "E1037", {"start": v(4.8, -68.32) * mm, "end": v(8.83, -68.32) * mm});
            skLineSegment(sketch, "E1038", {"start": v(8.83, -68.32) * mm, "end": v(10.68, -69.98) * mm});
            skLineSegment(sketch, "E1039", {"start": v(10.68, -69.98) * mm, "end": v(12.54, -70.36) * mm});
            skLineSegment(sketch, "E1040", {"start": v(12.54, -70.36) * mm, "end": v(13.56, -71.51) * mm});
            skLineSegment(sketch, "E1041", {"start": v(13.56, -71.51) * mm, "end": v(13.45, -73.94) * mm});
            skLineSegment(sketch, "E1042", {"start": v(13.45, -73.94) * mm, "end": v(18.03, -73.88) * mm});
            skLineSegment(sketch, "E1043", {"start": v(18.03, -73.88) * mm, "end": v(18.1, -75.98) * mm});
            skLineSegment(sketch, "E1044", {"start": v(18.1, -75.98) * mm, "end": v(2.25, -75.96) * mm});
            skLineSegment(sketch, "E1045", {"start": v(2.25, -75.96) * mm, "end": v(2.25, -75.54) * mm});
            skLineSegment(sketch, "E1046", {"start": v(11.54, -68.35) * mm, "end": v(11.54, -69.68) * mm});
            skLineSegment(sketch, "E1047", {"start": v(11.54, -69.68) * mm, "end": v(12.62, -69.9) * mm});
            skLineSegment(sketch, "E1048", {"start": v(12.62, -69.9) * mm, "end": v(13.9, -71.3) * mm});
            skLineSegment(sketch, "E1049", {"start": v(13.9, -71.3) * mm, "end": v(13.92, -73.48) * mm});
            skLineSegment(sketch, "E1050", {"start": v(13.92, -73.48) * mm, "end": v(17.54, -73.42) * mm});
            skLineSegment(sketch, "E1051", {"start": v(17.54, -73.42) * mm, "end": v(17.39, -68.23) * mm});
            skLineSegment(sketch, "E1052", {"start": v(17.39, -68.23) * mm, "end": v(11.5, -68.11) * mm});
            skLineSegment(sketch, "E1053", {"start": v(11.5, -68.11) * mm, "end": v(11.54, -68.35) * mm});
            skLineSegment(sketch, "E1054", {"start": v(30.75, -73.84) * mm, "end": v(30.75, -76.04) * mm});
            skLineSegment(sketch, "E1055", {"start": v(30.75, -76.04) * mm, "end": v(38.8, -76.16) * mm});
            skLineSegment(sketch, "E1056", {"start": v(38.8, -76.16) * mm, "end": v(38.73, -73.72) * mm});
            skLineSegment(sketch, "E1057", {"start": v(38.73, -73.72) * mm, "end": v(30.75, -73.84) * mm});
            skLineSegment(sketch, "E1058", {"start": v(32.87, -66.87) * mm, "end": v(32.87, -69.13) * mm});
            skLineSegment(sketch, "E1059", {"start": v(32.87, -69.13) * mm, "end": v(31.86, -69.2) * mm});
            skLineSegment(sketch, "E1060", {"start": v(31.86, -69.2) * mm, "end": v(31.78, -73.31) * mm});
            skLineSegment(sketch, "E1061", {"start": v(31.78, -73.31) * mm, "end": v(38.82, -73.27) * mm});
            skLineSegment(sketch, "E1062", {"start": v(38.82, -73.27) * mm, "end": v(39.87, -72.43) * mm});
            skLineSegment(sketch, "E1063", {"start": v(39.87, -72.43) * mm, "end": v(40.47, -71.3) * mm});
            skLineSegment(sketch, "E1064", {"start": v(40.47, -71.3) * mm, "end": v(41.2, -70.7) * mm});
            skLineSegment(sketch, "E1065", {"start": v(41.2, -70.7) * mm, "end": v(42.32, -69.97) * mm});
            skLineSegment(sketch, "E1066", {"start": v(42.32, -69.97) * mm, "end": v(42.77, -68.72) * mm});
            skLineSegment(sketch, "E1067", {"start": v(42.77, -68.72) * mm, "end": v(35.72, -68.8) * mm});
            skLineSegment(sketch, "E1068", {"start": v(35.72, -68.8) * mm, "end": v(35.76, -66.95) * mm});
            skLineSegment(sketch, "E1069", {"start": v(35.76, -66.95) * mm, "end": v(32.87, -66.87) * mm});
            skLineSegment(sketch, "E1070", {"start": v(39.3, -73.5) * mm, "end": v(40.25, -72.79) * mm});
            skLineSegment(sketch, "E1071", {"start": v(40.25, -72.79) * mm, "end": v(40.8, -71.56) * mm});
            skLineSegment(sketch, "E1072", {"start": v(40.8, -71.56) * mm, "end": v(41.66, -70.82) * mm});
            skLineSegment(sketch, "E1073", {"start": v(41.66, -70.82) * mm, "end": v(42.57, -70.46) * mm});
            skLineSegment(sketch, "E1074", {"start": v(42.57, -70.46) * mm, "end": v(43.53, -69) * mm});
            skLineSegment(sketch, "E1075", {"start": v(43.53, -69) * mm, "end": v(45.2, -68.78) * mm});
            skLineSegment(sketch, "E1076", {"start": v(45.2, -68.78) * mm, "end": v(45.66, -68.08) * mm});
            skLineSegment(sketch, "E1077", {"start": v(45.66, -68.08) * mm, "end": v(48.93, -68.05) * mm});
            skLineSegment(sketch, "E1078", {"start": v(48.93, -68.05) * mm, "end": v(50.01, -69.2) * mm});
            skLineSegment(sketch, "E1079", {"start": v(50.01, -69.2) * mm, "end": v(50.9, -69.43) * mm});
            skLineSegment(sketch, "E1080", {"start": v(50.9, -69.43) * mm, "end": v(52.02, -70.02) * mm});
            skLineSegment(sketch, "E1081", {"start": v(52.02, -70.02) * mm, "end": v(52.69, -70.72) * mm});
            skLineSegment(sketch, "E1082", {"start": v(52.69, -70.72) * mm, "end": v(53.01, -71.45) * mm});
            skLineSegment(sketch, "E1083", {"start": v(53.01, -71.45) * mm, "end": v(53.4, -73.26) * mm});
            skLineSegment(sketch, "E1084", {"start": v(53.4, -73.26) * mm, "end": v(52.4, -75.1) * mm});
            skLineSegment(sketch, "E1085", {"start": v(52.4, -75.1) * mm, "end": v(51.08, -76.02) * mm});
            skLineSegment(sketch, "E1086", {"start": v(51.08, -76.02) * mm, "end": v(39.2, -76.08) * mm});
            skLineSegment(sketch, "E1087", {"start": v(39.2, -76.08) * mm, "end": v(39.14, -73.7) * mm});
            skLineSegment(sketch, "E1088", {"start": v(39.14, -73.7) * mm, "end": v(39.3, -73.5) * mm});
            skLineSegment(sketch, "E1089", {"start": v(4.88, -27.78) * mm, "end": v(6.96, -27.07) * mm});
            skLineSegment(sketch, "E1090", {"start": v(6.96, -27.07) * mm, "end": v(8.17, -25.39) * mm});
            skLineSegment(sketch, "E1091", {"start": v(8.17, -25.39) * mm, "end": v(11.4, -25.42) * mm});
            skLineSegment(sketch, "E1092", {"start": v(11.4, -25.42) * mm, "end": v(11.53, -19.33) * mm});
            skLineSegment(sketch, "E1093", {"start": v(11.53, -19.33) * mm, "end": v(9.65, -16.96) * mm});
            skLineSegment(sketch, "E1094", {"start": v(9.65, -16.96) * mm, "end": v(5.7, -14.4) * mm});
            skLineSegment(sketch, "E1095", {"start": v(5.7, -14.4) * mm, "end": v(1.78, -13.36) * mm});
            skLineSegment(sketch, "E1096", {"start": v(1.78, -13.36) * mm, "end": v(0.02, -15.05) * mm});
            skLineSegment(sketch, "E1097", {"start": v(0.02, -15.05) * mm, "end": v(-3.17, -19.03) * mm});
            skLineSegment(sketch, "E1098", {"start": v(-3.17, -19.03) * mm, "end": v(-6.3, -25.31) * mm});
            skLineSegment(sketch, "E1099", {"start": v(-6.3, -25.31) * mm, "end": v(-5.92, -31.2) * mm});
            skLineSegment(sketch, "E1100", {"start": v(-5.92, -31.2) * mm, "end": v(-1.98, -36.04) * mm});
            skLineSegment(sketch, "E1101", {"start": v(-1.98, -36.04) * mm, "end": v(-0.19, -36.05) * mm});
            skLineSegment(sketch, "E1102", {"start": v(-0.19, -36.05) * mm, "end": v(-0.1, -39.15) * mm});
            skLineSegment(sketch, "E1103", {"start": v(-0.1, -39.15) * mm, "end": v(1.83, -39.49) * mm});
            skLineSegment(sketch, "E1104", {"start": v(1.83, -39.49) * mm, "end": v(1.85, -39.5) * mm});
            skLineSegment(sketch, "E1105", {"start": v(1.85, -39.5) * mm, "end": v(1.85, -29.78) * mm});
            skLineSegment(sketch, "E1106", {"start": v(1.85, -29.78) * mm, "end": v(3.61, -28.6) * mm});
            skLineSegment(sketch, "E1107", {"start": v(3.61, -28.6) * mm, "end": v(3.77, -18.46) * mm});
            skLineSegment(sketch, "E1108", {"start": v(3.77, -18.46) * mm, "end": v(3.77, -18.45) * mm});
            skLineSegment(sketch, "E1109", {"start": v(3.77, -18.45) * mm, "end": v(4.56, -18.5) * mm});
            skLineSegment(sketch, "E1110", {"start": v(4.56, -18.5) * mm, "end": v(4.46, -25.97) * mm});
            skLineSegment(sketch, "E1111", {"start": v(4.46, -25.97) * mm, "end": v(4.81, -27.9) * mm});
            skLineSegment(sketch, "E1112", {"start": v(4.81, -27.9) * mm, "end": v(4.88, -27.78) * mm});
            skLineSegment(sketch, "E1113", {"start": v(8.7, -27.61) * mm, "end": v(12.55, -27.53) * mm});
            skLineSegment(sketch, "E1114", {"start": v(12.55, -27.53) * mm, "end": v(12.47, -34.3) * mm});
            skLineSegment(sketch, "E1115", {"start": v(12.47, -34.3) * mm, "end": v(13.68, -35.1) * mm});
            skLineSegment(sketch, "E1116", {"start": v(13.68, -35.1) * mm, "end": v(13.69, -41.53) * mm});
            skLineSegment(sketch, "E1117", {"start": v(13.69, -41.53) * mm, "end": v(7.25, -41.53) * mm});
            skLineSegment(sketch, "E1118", {"start": v(7.25, -41.53) * mm, "end": v(5.48, -39.04) * mm});
            skLineSegment(sketch, "E1119", {"start": v(5.48, -39.04) * mm, "end": v(3.79, -38.95) * mm});
            skLineSegment(sketch, "E1120", {"start": v(3.79, -38.95) * mm, "end": v(3.79, -30.34) * mm});
            skLineSegment(sketch, "E1121", {"start": v(3.79, -30.34) * mm, "end": v(6.04, -29.78) * mm});
            skLineSegment(sketch, "E1122", {"start": v(6.04, -29.78) * mm, "end": v(7.41, -29.06) * mm});
            skLineSegment(sketch, "E1123", {"start": v(7.41, -29.06) * mm, "end": v(8.7, -27.61) * mm});
            skLineSegment(sketch, "E1124", {"start": v(7.45, 10.52) * mm, "end": v(8.87, 11.85) * mm});
            skLineSegment(sketch, "E1125", {"start": v(8.87, 11.85) * mm, "end": v(12.1, 13.7) * mm});
            skLineSegment(sketch, "E1126", {"start": v(12.1, 13.7) * mm, "end": v(17.56, 13.29) * mm});
            skLineSegment(sketch, "E1127", {"start": v(17.56, 13.29) * mm, "end": v(19.23, 11.74) * mm});
            skLineSegment(sketch, "E1128", {"start": v(19.23, 11.74) * mm, "end": v(19.23, 6.7) * mm});
            skLineSegment(sketch, "E1129", {"start": v(19.23, 6.7) * mm, "end": v(18.04, 6.53) * mm});
            skLineSegment(sketch, "E1130", {"start": v(18.04, 6.53) * mm, "end": v(17.28, 5.85) * mm});
            skLineSegment(sketch, "E1131", {"start": v(17.28, 5.85) * mm, "end": v(17.7, 5.37) * mm});
            skLineSegment(sketch, "E1132", {"start": v(17.7, 5.37) * mm, "end": v(18, 4.57) * mm});
            skLineSegment(sketch, "E1133", {"start": v(18, 4.57) * mm, "end": v(15.98, 1.54) * mm});
            skLineSegment(sketch, "E1134", {"start": v(15.98, 1.54) * mm, "end": v(14.28, 0.73) * mm});
            skLineSegment(sketch, "E1135", {"start": v(14.28, 0.73) * mm, "end": v(12.9, 1.4) * mm});
            skLineSegment(sketch, "E1136", {"start": v(12.9, 1.4) * mm, "end": v(13.01, 2.47) * mm});
            skLineSegment(sketch, "E1137", {"start": v(13.01, 2.47) * mm, "end": v(14.64, 2.97) * mm});
            skLineSegment(sketch, "E1138", {"start": v(14.64, 2.97) * mm, "end": v(15.4, 3.88) * mm});
            skLineSegment(sketch, "E1139", {"start": v(15.4, 3.88) * mm, "end": v(11.3, 4.06) * mm});
            skLineSegment(sketch, "E1140", {"start": v(11.3, 4.06) * mm, "end": v(10.66, 4.96) * mm});
            skLineSegment(sketch, "E1141", {"start": v(10.66, 4.96) * mm, "end": v(8.59, 5.64) * mm});
            skLineSegment(sketch, "E1142", {"start": v(8.59, 5.64) * mm, "end": v(7.77, 7.18) * mm});
            skLineSegment(sketch, "E1143", {"start": v(7.77, 7.18) * mm, "end": v(7.41, 9.12) * mm});
            skLineSegment(sketch, "E1144", {"start": v(7.41, 9.12) * mm, "end": v(7.45, 10.52) * mm});
            skLineSegment(sketch, "E1145", {"start": v(26.37, 6.04) * mm, "end": v(26.36, 11.65) * mm});
            skLineSegment(sketch, "E1146", {"start": v(27.06, 4.36) * mm, "end": v(27.52, 5.62) * mm});
            skLineSegment(sketch, "E1147", {"start": v(27.52, 5.62) * mm, "end": v(26.37, 6.04) * mm});
            skLineSegment(sketch, "E1148", {"start": v(12.92, -25.4) * mm, "end": v(12.96, -26.1) * mm});
            skLineSegment(sketch, "E1149", {"start": v(12.96, -26.1) * mm, "end": v(12.96, -27.1) * mm});
            skLineSegment(sketch, "E1150", {"start": v(12.96, -27.1) * mm, "end": v(14.03, -27.2) * mm});
            skLineSegment(sketch, "E1151", {"start": v(16.56, -27.42) * mm, "end": v(15.37, -27.36) * mm});
            skLineSegment(sketch, "E1152", {"start": v(15.37, -27.36) * mm, "end": v(14.84, -26.97) * mm});
            skLineSegment(sketch, "E1153", {"start": v(14.66, -25.4) * mm, "end": v(12.92, -25.4) * mm});
            skLineSegment(sketch, "E1154", {"start": v(16.72, -30.66) * mm, "end": v(16.1, -30.59) * mm});
            skLineSegment(sketch, "E1155", {"start": v(16.1, -30.59) * mm, "end": v(15.57, -31.4) * mm});
            skLineSegment(sketch, "E1156", {"start": v(14.33, -31.97) * mm, "end": v(14.33, -33.93) * mm});
            skLineSegment(sketch, "E1157", {"start": v(14.33, -33.93) * mm, "end": v(15.43, -33.93) * mm});
            skLineSegment(sketch, "E1158", {"start": v(15.43, -33.93) * mm, "end": v(15.67, -33.38) * mm});
            skLineSegment(sketch, "E1159", {"start": v(15.67, -33.38) * mm, "end": v(16.79, -33.4) * mm});
            skLineSegment(sketch, "E1160", {"start": v(16.79, -33.4) * mm, "end": v(16.72, -30.66) * mm});
            skLineSegment(sketch, "E1161.left", {"start": v(28.71, -24) * mm, "end": v(28.71, -21.41) * mm});
            skLineSegment(sketch, "E1161.right", {"start": v(30.22, -24) * mm, "end": v(30.22, -21.41) * mm});
            skLineSegment(sketch, "E1162", {"start": v(29.95, -25.15) * mm, "end": v(27.72, -26.23) * mm});
            skLineSegment(sketch, "E1163", {"start": v(30.01, -29.12) * mm, "end": v(29.95, -25.15) * mm});
            skLineSegment(sketch, "E1164", {"start": v(30.13, -30.21) * mm, "end": v(27.54, -30.1) * mm});
            skLineSegment(sketch, "E1165", {"start": v(27.54, -30.1) * mm, "end": v(27.54, -33.1) * mm});
            skLineSegment(sketch, "E1166.bottom", {"start": v(29.23, -34.55) * mm, "end": v(27.36, -34.55) * mm});
            skLineSegment(sketch, "E1166.top", {"start": v(29.23, -39.2) * mm, "end": v(27.36, -39.2) * mm});
            skLineSegment(sketch, "E1167", {"start": v(30.36, -39.66) * mm, "end": v(31.14, -37.58) * mm});
            skLineSegment(sketch, "E1168", {"start": v(31.14, -37.58) * mm, "end": v(32.66, -35.93) * mm});
            skLineSegment(sketch, "E1169", {"start": v(32.66, -35.93) * mm, "end": v(33.41, -33.78) * mm});
            skLineSegment(sketch, "E1170", {"start": v(33.41, -33.78) * mm, "end": v(34.02, -31.19) * mm});
            skLineSegment(sketch, "E1171", {"start": v(34.02, -31.19) * mm, "end": v(34.57, -29.2) * mm});
            skLineSegment(sketch, "E1172", {"start": v(34.57, -29.2) * mm, "end": v(36.22, -27.54) * mm});
            skLineSegment(sketch, "E1173", {"start": v(36.22, -27.54) * mm, "end": v(38.7, -26.05) * mm});
            skLineSegment(sketch, "E1174", {"start": v(38.7, -26.05) * mm, "end": v(40.46, -25.21) * mm});
            skLineSegment(sketch, "E1175", {"start": v(40.46, -25.21) * mm, "end": v(40.62, -30.12) * mm});
            skLineSegment(sketch, "E1176", {"start": v(30.87, -40.23) * mm, "end": v(30.36, -39.66) * mm});
            skLineSegment(sketch, "E1177", {"start": v(32.7, -32.46) * mm, "end": v(31.22, -32.46) * mm});
            skLineSegment(sketch, "E1178", {"start": v(31.22, -32.46) * mm, "end": v(31.14, -21.4) * mm});
            skLineSegment(sketch, "E1179", {"start": v(31.14, -21.4) * mm, "end": v(31.62, -20.33) * mm});
            skLineSegment(sketch, "E1180", {"start": v(31.62, -20.33) * mm, "end": v(33.71, -19.65) * mm});
            skLineSegment(sketch, "E1181", {"start": v(33.71, -19.65) * mm, "end": v(34.86, -18.77) * mm});
            skLineSegment(sketch, "E1182", {"start": v(34.86, -18.77) * mm, "end": v(37.1, -18.3) * mm});
            skLineSegment(sketch, "E1183", {"start": v(37.1, -18.3) * mm, "end": v(38.59, -16.74) * mm});
            skLineSegment(sketch, "E1184", {"start": v(38.59, -16.74) * mm, "end": v(39.74, -14.84) * mm});
            skLineSegment(sketch, "E1185", {"start": v(39.74, -14.84) * mm, "end": v(40.89, -13.42) * mm});
            skLineSegment(sketch, "E1186", {"start": v(40.89, -13.42) * mm, "end": v(41.77, -12) * mm});
            skLineSegment(sketch, "E1187", {"start": v(41.77, -12) * mm, "end": v(42.78, -12.2) * mm});
            skLineSegment(sketch, "E1188", {"start": v(42.78, -12.2) * mm, "end": v(43.93, -13.62) * mm});
            skLineSegment(sketch, "E1189", {"start": v(43.93, -13.62) * mm, "end": v(44.75, -15.38) * mm});
            skLineSegment(sketch, "E1190", {"start": v(44.75, -15.38) * mm, "end": v(46.17, -16.87) * mm});
            skLineSegment(sketch, "E1191", {"start": v(46.17, -16.87) * mm, "end": v(46.91, -18.5) * mm});
            skLineSegment(sketch, "E1192", {"start": v(46.91, -18.5) * mm, "end": v(47.25, -19.99) * mm});
            skLineSegment(sketch, "E1193", {"start": v(47.25, -19.99) * mm, "end": v(47.66, -21.48) * mm});
            skLineSegment(sketch, "E1194", {"start": v(47.66, -21.48) * mm, "end": v(47.93, -22.83) * mm});
            skLineSegment(sketch, "E1195", {"start": v(47.93, -22.83) * mm, "end": v(48.8, -23.5) * mm});
            skLineSegment(sketch, "E1196", {"start": v(48.8, -23.5) * mm, "end": v(49.08, -25.4) * mm});
            skLineSegment(sketch, "E1197", {"start": v(49.08, -25.4) * mm, "end": v(49, -27.3) * mm});
            skLineSegment(sketch, "E1198", {"start": v(49, -27.3) * mm, "end": v(50.63, -27.7) * mm});
            skLineSegment(sketch, "E1199", {"start": v(50.63, -27.7) * mm, "end": v(50.7, -28.92) * mm});
            skLineSegment(sketch, "E1200", {"start": v(50.7, -28.92) * mm, "end": v(50.77, -31.63) * mm});
            skLineSegment(sketch, "E1201", {"start": v(50.77, -31.63) * mm, "end": v(50.77, -33.52) * mm});
            skLineSegment(sketch, "E1202", {"start": v(50.77, -33.52) * mm, "end": v(49.35, -33.46) * mm});
            skLineSegment(sketch, "E1203", {"start": v(49.35, -33.46) * mm, "end": v(48.2, -34.47) * mm});
            skLineSegment(sketch, "E1204", {"start": v(48.2, -34.47) * mm, "end": v(47.72, -35.7) * mm});
            skLineSegment(sketch, "E1205", {"start": v(47.72, -35.7) * mm, "end": v(48.06, -36.3) * mm});
            skLineSegment(sketch, "E1206", {"start": v(48.06, -36.3) * mm, "end": v(47.39, -37.72) * mm});
            skLineSegment(sketch, "E1207", {"start": v(47.39, -37.72) * mm, "end": v(45.83, -38.87) * mm});
            skLineSegment(sketch, "E1208", {"start": v(45.83, -38.87) * mm, "end": v(44.48, -39) * mm});
            skLineSegment(sketch, "E1209", {"start": v(44.48, -39) * mm, "end": v(43.33, -38.26) * mm});
            skLineSegment(sketch, "E1210", {"start": v(43.33, -38.26) * mm, "end": v(43.33, -28.8) * mm});
            skLineSegment(sketch, "E1211", {"start": v(43.33, -28.8) * mm, "end": v(42.47, -28.26) * mm});
            skLineSegment(sketch, "E1212", {"start": v(42.47, -28.26) * mm, "end": v(41.6, -23.56) * mm});
            skLineSegment(sketch, "E1213", {"start": v(41.6, -23.56) * mm, "end": v(41.74, -19.13) * mm});
            skLineSegment(sketch, "E1214", {"start": v(41.74, -19.13) * mm, "end": v(43.2, -17.46) * mm});
            skLineSegment(sketch, "E1215", {"start": v(43.2, -17.46) * mm, "end": v(42.51, -17.05) * mm});
            skLineSegment(sketch, "E1216", {"start": v(42.51, -17.05) * mm, "end": v(41.02, -18.77) * mm});
            skLineSegment(sketch, "E1217", {"start": v(41.02, -18.77) * mm, "end": v(40.66, -23.2) * mm});
            skLineSegment(sketch, "E1218", {"start": v(40.66, -23.2) * mm, "end": v(38.94, -24.33) * mm});
            skLineSegment(sketch, "E1219", {"start": v(38.94, -24.33) * mm, "end": v(36.5, -26.04) * mm});
            skLineSegment(sketch, "E1220", {"start": v(36.5, -26.04) * mm, "end": v(34.83, -27.25) * mm});
            skLineSegment(sketch, "E1221", {"start": v(34.83, -27.25) * mm, "end": v(33.49, -28.66) * mm});
            skLineSegment(sketch, "E1222", {"start": v(33.49, -28.66) * mm, "end": v(32.7, -32.46) * mm});
            skLineSegment(sketch, "E1223.bottom", {"start": v(12.84, 10.33) * mm, "end": v(16.02, 10.33) * mm});
            skLineSegment(sketch, "E1223.top", {"start": v(12.84, 6.3) * mm, "end": v(16.02, 6.3) * mm});
            skLineSegment(sketch, "E1223.left", {"start": v(12.84, 10.33) * mm, "end": v(12.84, 6.3) * mm});
            skLineSegment(sketch, "E1223.right", {"start": v(16.02, 10.33) * mm, "end": v(16.02, 6.3) * mm});
            skLineSegment(sketch, "E1224.left", {"start": v(12.84, 6.3) * mm, "end": v(12.84, 10.33) * mm});
            skLineSegment(sketch, "E1224.right", {"start": v(16.02, 6.3) * mm, "end": v(16.02, 10.33) * mm});
            skLineSegment(sketch, "E1225.bottom", {"start": v(29.46, 10.33) * mm, "end": v(33.1, 10.33) * mm});
            skLineSegment(sketch, "E1225.top", {"start": v(29.46, 6.1) * mm, "end": v(33.1, 6.1) * mm});
            skLineSegment(sketch, "E1225.left", {"start": v(29.46, 10.33) * mm, "end": v(29.46, 6.1) * mm});
            skLineSegment(sketch, "E1225.right", {"start": v(33.1, 10.33) * mm, "end": v(33.1, 6.1) * mm});
            skLineSegment(sketch, "E1226", {"start": v(20.42, 3.4) * mm, "end": v(21.77, 3.87) * mm});
            skLineSegment(sketch, "E1227", {"start": v(21.77, 3.87) * mm, "end": v(21.77, 6.56) * mm});
            skLineSegment(sketch, "E1228", {"start": v(21.77, 6.56) * mm, "end": v(24.18, 6.5) * mm});
            skLineSegment(sketch, "E1229", {"start": v(24.18, 6.5) * mm, "end": v(24.18, 4.2) * mm});
            skLineSegment(sketch, "E1230", {"start": v(24.18, 4.2) * mm, "end": v(25.47, 3.2) * mm});
            skLineSegment(sketch, "E1231", {"start": v(25.47, 3.2) * mm, "end": v(25.47, -0.9) * mm});
            skLineSegment(sketch, "E1232", {"start": v(25.47, -0.9) * mm, "end": v(20.42, -0.9) * mm});
            skLineSegment(sketch, "E1233", {"start": v(20.42, -0.9) * mm, "end": v(20.42, 3.4) * mm});
            skLineSegment(sketch, "E1234", {"start": v(10.47, 0.01) * mm, "end": v(11.03, 1.29) * mm});
            skLineSegment(sketch, "E1235", {"start": v(11.03, 1.29) * mm, "end": v(12.22, 1.12) * mm});
            skLineSegment(sketch, "E1236", {"start": v(17.7, -4.2) * mm, "end": v(29.97, -4.2) * mm});
            skLineSegment(sketch, "E1237", {"start": v(30.34, -3.05) * mm, "end": v(31.78, -2.4) * mm});
            skLineSegment(sketch, "E1238", {"start": v(31.78, -2.4) * mm, "end": v(33.2, -1.7) * mm});
            skLineSegment(sketch, "E1239", {"start": v(36.6, -2.38) * mm, "end": v(38.18, -3.23) * mm});
            skLineSegment(sketch, "E1240", {"start": v(38.18, -3.23) * mm, "end": v(37.08, -4.08) * mm});
            skLineSegment(sketch, "E1241", {"start": v(37.08, -4.08) * mm, "end": v(35.24, -3.95) * mm});
            skLineSegment(sketch, "E1242", {"start": v(35.24, -3.95) * mm, "end": v(35.24, -3.95) * mm});
            skLineSegment(sketch, "E1243", {"start": v(35.24, -3.95) * mm, "end": v(33.88, -6.56) * mm});
            skLineSegment(sketch, "E1244", {"start": v(33.88, -6.56) * mm, "end": v(31.23, -9.37) * mm});
            skLineSegment(sketch, "E1245", {"start": v(31.23, -9.37) * mm, "end": v(28.8, -10.73) * mm});
            skLineSegment(sketch, "E1246", {"start": v(12.43, -6.43) * mm, "end": v(11.04, -5.42) * mm});
            skLineSegment(sketch, "E1247", {"start": v(11.04, -5.42) * mm, "end": v(10.15, -3.7) * mm});
            skLineSegment(sketch, "E1248", {"start": v(10.15, -3.7) * mm, "end": v(10.15, -3.7) * mm});
            skLineSegment(sketch, "E1249", {"start": v(10.15, -3.7) * mm, "end": v(8.97, -3.36) * mm});
            skLineSegment(sketch, "E1250.bottom", {"start": v(11.72, -2.3) * mm, "end": v(13.94, -2.3) * mm});
            skLineSegment(sketch, "E1250.top", {"start": v(11.72, -5.74) * mm, "end": v(13.94, -5.74) * mm});
            skLineSegment(sketch, "E1250.left", {"start": v(11.72, -2.3) * mm, "end": v(11.72, -5.74) * mm});
            skLineSegment(sketch, "E1250.right", {"start": v(13.94, -2.3) * mm, "end": v(13.94, -5.74) * mm});
            skLineSegment(sketch, "E1251.bottom", {"start": v(11.72, -5.74) * mm, "end": v(13.93, -5.74) * mm});
            skLineSegment(sketch, "E1251.top", {"start": v(11.72, -2.3) * mm, "end": v(13.93, -2.3) * mm});
            skLineSegment(sketch, "E1251.left", {"start": v(11.72, -5.74) * mm, "end": v(11.72, -2.3) * mm});
            skLineSegment(sketch, "E1251.right", {"start": v(13.93, -5.74) * mm, "end": v(13.93, -2.3) * mm});
            skLineSegment(sketch, "E1252.bottom", {"start": v(18.38, -5.16) * mm, "end": v(22.17, -5.16) * mm});
            skLineSegment(sketch, "E1252.top", {"start": v(18.38, -9.9) * mm, "end": v(22.17, -9.9) * mm});
            skLineSegment(sketch, "E1252.left", {"start": v(18.38, -5.16) * mm, "end": v(18.38, -9.9) * mm});
            skLineSegment(sketch, "E1252.right", {"start": v(22.17, -5.16) * mm, "end": v(22.17, -9.9) * mm});
            skLineSegment(sketch, "E1253.bottom", {"start": v(22.73, -5.18) * mm, "end": v(27.11, -5.18) * mm});
            skLineSegment(sketch, "E1253.top", {"start": v(22.73, -9.88) * mm, "end": v(27.11, -9.88) * mm});
            skLineSegment(sketch, "E1253.left", {"start": v(22.73, -5.18) * mm, "end": v(22.73, -9.88) * mm});
            skLineSegment(sketch, "E1253.right", {"start": v(27.11, -5.18) * mm, "end": v(27.11, -9.88) * mm});
            skLineSegment(sketch, "E1254.bottom", {"start": v(30.66, -3.36) * mm, "end": v(33.13, -3.36) * mm});
            skLineSegment(sketch, "E1254.top", {"start": v(30.66, -7) * mm, "end": v(33.13, -7) * mm});
            skLineSegment(sketch, "E1254.left", {"start": v(30.66, -3.36) * mm, "end": v(30.66, -7) * mm});
            skLineSegment(sketch, "E1254.right", {"start": v(33.13, -3.36) * mm, "end": v(33.13, -7) * mm});
            skLineSegment(sketch, "E1255", {"start": v(14.33, -3.7) * mm, "end": v(14.33, -7.12) * mm});
            skLineSegment(sketch, "E1256", {"start": v(17.9, -8.71) * mm, "end": v(17.9, -5.39) * mm});
            skLineSegment(sketch, "E1257", {"start": v(14.33, -3.7) * mm, "end": v(16, -3.7) * mm});
            skLineSegment(sketch, "E1258", {"start": v(16, -3.7) * mm, "end": v(16, -4.8) * mm});
            skLineSegment(sketch, "E1259", {"start": v(16, -4.8) * mm, "end": v(16.54, -5.3) * mm});
            skLineSegment(sketch, "E1260", {"start": v(16.54, -5.3) * mm, "end": v(17.9, -5.39) * mm});
            skLineSegment(sketch, "E1261", {"start": v(15.75, -8.27) * mm, "end": v(14.98, -7.47) * mm});
            skLineSegment(sketch, "E1262", {"start": v(14.98, -7.47) * mm, "end": v(14.33, -7.12) * mm});
            skLineSegment(sketch, "E1263", {"start": v(15.75, -8.27) * mm, "end": v(15.99, -8.71) * mm});
            skLineSegment(sketch, "E1264", {"start": v(15.99, -8.71) * mm, "end": v(17.9, -8.71) * mm});
            skLineSegment(sketch, "E1265", {"start": v(27.51, -5.15) * mm, "end": v(27.51, -9.45) * mm});
            skLineSegment(sketch, "E1266", {"start": v(27.51, -9.45) * mm, "end": v(29.44, -9.45) * mm});
            skLineSegment(sketch, "E1267", {"start": v(29.44, -9.45) * mm, "end": v(30.34, -8.24) * mm});
            skLineSegment(sketch, "E1268", {"start": v(30.34, -8.24) * mm, "end": v(30.34, -5.15) * mm});
            skLineSegment(sketch, "E1269", {"start": v(30.34, -5.15) * mm, "end": v(27.51, -5.15) * mm});
            skLineSegment(sketch, "E1270", {"start": v(14.33, -7.12) * mm, "end": v(14.98, -7.47) * mm});
            skLineSegment(sketch, "E1271", {"start": v(14.98, -7.47) * mm, "end": v(15.75, -8.26) * mm});
            skLineSegment(sketch, "E1272", {"start": v(15.75, -8.26) * mm, "end": v(15.99, -8.71) * mm});
            skLineSegment(sketch, "E1273", {"start": v(15.99, -8.71) * mm, "end": v(17.89, -8.7) * mm});
            skLineSegment(sketch, "E1274", {"start": v(17.89, -8.7) * mm, "end": v(17.89, -5.4) * mm});
            skLineSegment(sketch, "E1275", {"start": v(17.89, -5.4) * mm, "end": v(16.54, -5.3) * mm});
            skLineSegment(sketch, "E1276", {"start": v(16.54, -5.3) * mm, "end": v(16, -4.8) * mm});
            skLineSegment(sketch, "E1277", {"start": v(16, -4.8) * mm, "end": v(16, -3.7) * mm});
            skLineSegment(sketch, "E1278", {"start": v(16, -3.7) * mm, "end": v(14.33, -3.7) * mm});
            skLineSegment(sketch, "E1279.bottom", {"start": v(18.39, -9.9) * mm, "end": v(22.17, -9.9) * mm});
            skLineSegment(sketch, "E1279.top", {"start": v(18.39, -5.16) * mm, "end": v(22.17, -5.16) * mm});
            skLineSegment(sketch, "E1279.left", {"start": v(18.39, -9.9) * mm, "end": v(18.39, -5.16) * mm});
            skLineSegment(sketch, "E1279.right", {"start": v(22.17, -9.9) * mm, "end": v(22.17, -5.16) * mm});
            skLineSegment(sketch, "E1280.bottom", {"start": v(22.74, -9.88) * mm, "end": v(27.1, -9.88) * mm});
            skLineSegment(sketch, "E1280.top", {"start": v(22.74, -5.19) * mm, "end": v(27.1, -5.19) * mm});
            skLineSegment(sketch, "E1280.left", {"start": v(22.74, -9.88) * mm, "end": v(22.74, -5.19) * mm});
            skLineSegment(sketch, "E1280.right", {"start": v(27.1, -9.88) * mm, "end": v(27.1, -5.19) * mm});
            skLineSegment(sketch, "E1281.bottom", {"start": v(30.66, -7) * mm, "end": v(33.12, -7) * mm});
            skLineSegment(sketch, "E1281.top", {"start": v(30.66, -3.36) * mm, "end": v(33.12, -3.36) * mm});
            skLineSegment(sketch, "E1281.left", {"start": v(30.66, -7) * mm, "end": v(30.66, -3.36) * mm});
            skLineSegment(sketch, "E1281.right", {"start": v(33.12, -7) * mm, "end": v(33.12, -3.36) * mm});
            skLineSegment(sketch, "E1282", {"start": v(27.52, -5.15) * mm, "end": v(27.52, -9.44) * mm});
            skLineSegment(sketch, "E1283", {"start": v(27.52, -9.44) * mm, "end": v(29.44, -9.44) * mm});
            skLineSegment(sketch, "E1284", {"start": v(29.44, -9.44) * mm, "end": v(30.34, -8.24) * mm});
            skLineSegment(sketch, "E1285", {"start": v(30.34, -5.15) * mm, "end": v(27.52, -5.15) * mm});
            skLineSegment(sketch, "E1286", {"start": v(10.54, -43.95) * mm, "end": v(9.97, -45.8) * mm});
            skLineSegment(sketch, "E1287", {"start": v(9.97, -45.8) * mm, "end": v(9.72, -47.8) * mm});
            skLineSegment(sketch, "E1288", {"start": v(9.72, -47.8) * mm, "end": v(8.65, -49.15) * mm});
            skLineSegment(sketch, "E1289", {"start": v(8.65, -49.15) * mm, "end": v(8.37, -55.14) * mm});
            skLineSegment(sketch, "E1290", {"start": v(8.37, -55.14) * mm, "end": v(8.35, -55.2) * mm});
            skLineSegment(sketch, "E1291", {"start": v(8.35, -55.2) * mm, "end": v(7.22, -56.05) * mm});
            skLineSegment(sketch, "E1292", {"start": v(7.22, -56.05) * mm, "end": v(7.4, -62.12) * mm});
            skLineSegment(sketch, "E1293", {"start": v(7.4, -62.12) * mm, "end": v(9.04, -61.94) * mm});
            skLineSegment(sketch, "E1294", {"start": v(9.04, -61.94) * mm, "end": v(9.15, -56.68) * mm});
            skLineSegment(sketch, "E1295", {"start": v(9.15, -56.68) * mm, "end": v(10.48, -54.78) * mm});
            skLineSegment(sketch, "E1296", {"start": v(10.48, -54.78) * mm, "end": v(10.38, -49.57) * mm});
            skLineSegment(sketch, "E1297", {"start": v(10.38, -49.57) * mm, "end": v(12.5, -47) * mm});
            skLineSegment(sketch, "E1298", {"start": v(12.5, -47) * mm, "end": v(14.06, -48.38) * mm});
            skLineSegment(sketch, "E1299", {"start": v(14.06, -48.38) * mm, "end": v(12.78, -49.84) * mm});
            skLineSegment(sketch, "E1300", {"start": v(12.78, -49.84) * mm, "end": v(13.15, -55.2) * mm});
            skLineSegment(sketch, "E1301", {"start": v(13.15, -55.2) * mm, "end": v(11.9, -56.72) * mm});
            skLineSegment(sketch, "E1302", {"start": v(11.9, -56.72) * mm, "end": v(12, -62.25) * mm});
            skLineSegment(sketch, "E1303", {"start": v(12, -62.25) * mm, "end": v(12.76, -63.63) * mm});
            skLineSegment(sketch, "E1304", {"start": v(12.76, -63.63) * mm, "end": v(22.54, -63.75) * mm});
            skLineSegment(sketch, "E1305", {"start": v(22.54, -63.75) * mm, "end": v(22.93, -56.53) * mm});
            skLineSegment(sketch, "E1306", {"start": v(22.93, -56.53) * mm, "end": v(24.13, -56.37) * mm});
            skLineSegment(sketch, "E1307", {"start": v(24.13, -56.37) * mm, "end": v(24.34, -50.42) * mm});
            skLineSegment(sketch, "E1308", {"start": v(24.34, -50.42) * mm, "end": v(25.94, -49.04) * mm});
            skLineSegment(sketch, "E1309", {"start": v(25.94, -49.04) * mm, "end": v(27.95, -50.86) * mm});
            skLineSegment(sketch, "E1310", {"start": v(27.95, -50.86) * mm, "end": v(27.95, -54.02) * mm});
            skLineSegment(sketch, "E1311", {"start": v(27.95, -54.02) * mm, "end": v(29.57, -55.65) * mm});
            skLineSegment(sketch, "E1312", {"start": v(35.89, -63.21) * mm, "end": v(36.05, -59.4) * mm});
            skLineSegment(sketch, "E1313", {"start": v(36.05, -59.4) * mm, "end": v(34.55, -57.99) * mm});
            skLineSegment(sketch, "E1314", {"start": v(34.55, -57.99) * mm, "end": v(34.52, -57.94) * mm});
            skLineSegment(sketch, "E1315", {"start": v(34.52, -57.94) * mm, "end": v(34.71, -44.62) * mm});
            skLineSegment(sketch, "E1316", {"start": v(34.71, -44.62) * mm, "end": v(37.63, -44.73) * mm});
            skLineSegment(sketch, "E1317", {"start": v(37.63, -44.73) * mm, "end": v(37.63, -51.73) * mm});
            skLineSegment(sketch, "E1318", {"start": v(37.63, -51.73) * mm, "end": v(39.34, -53.16) * mm});
            skLineSegment(sketch, "E1319", {"start": v(39.34, -53.16) * mm, "end": v(38.6, -62.06) * mm});
            skLineSegment(sketch, "E1320", {"start": v(38.6, -62.06) * mm, "end": v(40.2, -63.48) * mm});
            skLineSegment(sketch, "E1321", {"start": v(40.2, -63.48) * mm, "end": v(42, -62.42) * mm});
            skLineSegment(sketch, "E1322", {"start": v(42, -62.42) * mm, "end": v(45.55, -62.35) * mm});
            skLineSegment(sketch, "E1323", {"start": v(45.55, -62.35) * mm, "end": v(45.5, -55.08) * mm});
            skLineSegment(sketch, "E1324", {"start": v(45.5, -55.08) * mm, "end": v(44.57, -54.02) * mm});
            skLineSegment(sketch, "E1325", {"start": v(44.57, -54.02) * mm, "end": v(44.38, -49.24) * mm});
            skLineSegment(sketch, "E1326", {"start": v(44.38, -49.24) * mm, "end": v(43.3, -46.27) * mm});
            skLineSegment(sketch, "E1327", {"start": v(43.3, -46.27) * mm, "end": v(43.69, -44.64) * mm});
            skLineSegment(sketch, "E1328", {"start": v(43.69, -44.64) * mm, "end": v(43.69, -41.7) * mm});
            skLineSegment(sketch, "E1329", {"start": v(43.69, -41.7) * mm, "end": v(42.95, -40.43) * mm});
            skLineSegment(sketch, "E1330", {"start": v(42.95, -40.43) * mm, "end": v(40.88, -41.15) * mm});
            skLineSegment(sketch, "E1331", {"start": v(40.88, -41.15) * mm, "end": v(38.59, -41.99) * mm});
            skLineSegment(sketch, "E1332", {"start": v(38.59, -41.99) * mm, "end": v(32.68, -41.66) * mm});
            skLineSegment(sketch, "E1333", {"start": v(32.68, -41.66) * mm, "end": v(28.8, -42) * mm});
            skLineSegment(sketch, "E1334", {"start": v(28.8, -42) * mm, "end": v(27.66, -42.02) * mm});
            skLineSegment(sketch, "E1335", {"start": v(27.66, -42.02) * mm, "end": v(26.78, -40.76) * mm});
            skLineSegment(sketch, "E1336", {"start": v(26.78, -40.76) * mm, "end": v(21.8, -40.92) * mm});
            skLineSegment(sketch, "E1337", {"start": v(21.8, -40.92) * mm, "end": v(20.41, -41.6) * mm});
            skLineSegment(sketch, "E1338", {"start": v(20.41, -41.6) * mm, "end": v(19.7, -42.64) * mm});
            skLineSegment(sketch, "E1339", {"start": v(19.7, -42.64) * mm, "end": v(19.62, -42.68) * mm});
            skLineSegment(sketch, "E1340", {"start": v(19.62, -42.68) * mm, "end": v(15.2, -42.77) * mm});
            skLineSegment(sketch, "E1341", {"start": v(15.2, -42.77) * mm, "end": v(13.61, -44.08) * mm});
            skLineSegment(sketch, "E1342", {"start": v(13.61, -44.08) * mm, "end": v(10.54, -43.95) * mm});
            skSolve(sketch);
        }
        {
            var Q0;
            Q0=makeQuery(id+"F2.imprint","IMPRINT",FACE,{"disambiguationData":[TD([[makeQuery(id+"F2.imprint","IMPRINT",EDGE,{"derivedFrom":sQuery(id+"F2.wireOp",EDGE,"E722")}),-1.0]])]});
            var Q1;
            Q1=makeQuery(id+"F2.imprint","IMPRINT",FACE,{"disambiguationData":[TD([[makeQuery(id+"F2.imprint","IMPRINT",EDGE,{"derivedFrom":sQuery(id+"F2.wireOp",EDGE,"E737")}),1.0]])]});
            var Q2;
            Q2=makeQuery(id+"F2.imprint","IMPRINT",FACE,{"disambiguationData":[TD([[makeQuery(id+"F2.imprint","IMPRINT",EDGE,{"derivedFrom":sQuery(id+"F2.wireOp",EDGE,"E967")}),-1.0]])]});
            var Q3;
            Q3=makeQuery(id+"F2.imprint","IMPRINT",FACE,{"disambiguationData":[TD([[makeQuery(id+"F2.imprint","IMPRINT",EDGE,{"derivedFrom":sQuery(id+"F2.wireOp",EDGE,"E1035")}),-1.0]])]});
            var Q4;
            Q4=makeQuery(id+"F2.imprint","IMPRINT",FACE,{"disambiguationData":[TD([[makeQuery(id+"F2.imprint","IMPRINT",EDGE,{"derivedFrom":sQuery(id+"F2.wireOp",EDGE,"E1046")}),1.0]])]});
            var Q5;
            Q5=makeQuery(id+"F2.imprint","IMPRINT",FACE,{"disambiguationData":[TD([[makeQuery(id+"F2.imprint","IMPRINT",EDGE,{"derivedFrom":sQuery(id+"F2.wireOp",EDGE,"E1054")}),1.0]])]});
            var Q6;
            Q6=makeQuery(id+"F2.imprint","IMPRINT",FACE,{"disambiguationData":[TD([[makeQuery(id+"F2.imprint","IMPRINT",EDGE,{"derivedFrom":sQuery(id+"F2.wireOp",EDGE,"E1058")}),1.0]])]});
            var Q7;
            Q7=makeQuery(id+"F2.imprint","IMPRINT",FACE,{"disambiguationData":[TD([[makeQuery(id+"F2.imprint","IMPRINT",EDGE,{"derivedFrom":sQuery(id+"F2.wireOp",EDGE,"E1070")}),-1.0]])]});
            var Q8;
            Q8=makeQuery(id+"F2.imprint","IMPRINT",FACE,{"disambiguationData":[TD([[makeQuery(id+"F2.imprint","IMPRINT",EDGE,{"derivedFrom":sQuery(id+"F2.wireOp",EDGE,"c1c82c28-52c2-4fab-9710-17f7591158fe")}),-1.0]])]});
            var Q9;
            Q9=makeQuery(id+"F2.imprint","IMPRINT",FACE,{"disambiguationData":[TD([[makeQuery(id+"F2.imprint","IMPRINT",EDGE,{"derivedFrom":sQuery(id+"F2.wireOp",EDGE,"4ee1179b-3031-4ee2-a42b-07435d50cfc0")}),1.0]])]});
            var Q10;
            Q10=makeQuery(id+"F2.imprint","IMPRINT",FACE,{"disambiguationData":[TD([[makeQuery(id+"F2.imprint","IMPRINT",EDGE,{"derivedFrom":sQuery(id+"F2.wireOp",EDGE,"10aeca11-c88a-4ddb-b15b-c2b15c4dfa68.bottom")}),-1.0]])]});
            var Q11;
            Q11=makeQuery(id+"F2.imprint","IMPRINT",FACE,{"disambiguationData":[TD([[makeQuery(id+"F2.imprint","IMPRINT",EDGE,{"derivedFrom":sQuery(id+"F2.wireOp",EDGE,"37253bd0-4693-48ca-a450-64db61d699f5")}),1.0]])]});
            var Q12;
            Q12=makeQuery(id+"F2.imprint","IMPRINT",FACE,{"disambiguationData":[TD([[makeQuery(id+"F2.imprint","IMPRINT",EDGE,{"derivedFrom":sQuery(id+"F2.wireOp",EDGE,"4021a4ca-61fd-4e59-a8d2-e24243b1d5b2.bottom")}),-1.0]])]});
            var Q13;
            Q13=makeQuery(id+"F2.imprint","IMPRINT",FACE,{"disambiguationData":[TD([[makeQuery(id+"F2.imprint","IMPRINT",EDGE,{"derivedFrom":sQuery(id+"F2.wireOp",EDGE,"E1089")}),1.0]])]});
            var Q14;
            Q14=makeQuery(id+"F2.imprint","IMPRINT",FACE,{"disambiguationData":[TD([[makeQuery(id+"F2.imprint","IMPRINT",EDGE,{"derivedFrom":sQuery(id+"F2.wireOp",EDGE,"E1113")}),-1.0]])]});
            var Q15;
            Q15=makeQuery(id+"F2.imprint","IMPRINT",FACE,{"disambiguationData":[TD([[makeQuery(id+"F2.imprint","IMPRINT",EDGE,{"derivedFrom":sQuery(id+"F2.wireOp",EDGE,"E1124")}),-1.0]])]});
            var Q16;
            Q16=makeQuery(id+"F2.imprint","IMPRINT",FACE,{"disambiguationData":[TD([[makeQuery(id+"F2.imprint","IMPRINT",EDGE,{"derivedFrom":sQuery(id+"F2.wireOp",EDGE,"E1145")}),-1.0]])]});
            var Q17;
            Q17=makeQuery(id+"F2.imprint","IMPRINT",FACE,{"disambiguationData":[TD([[makeQuery(id+"F2.imprint","IMPRINT",EDGE,{"derivedFrom":sQuery(id+"F2.wireOp",EDGE,"E863")}),1.0]])]});
            var Q18;
            Q18=makeQuery(id+"F2.imprint","IMPRINT",FACE,{"disambiguationData":[TD([[makeQuery(id+"F2.imprint","IMPRINT",EDGE,{"derivedFrom":sQuery(id+"F2.wireOp",EDGE,"E1148")}),1.0]])]});
            var Q19;
            Q19=makeQuery(id+"F2.imprint","IMPRINT",FACE,{"disambiguationData":[TD([[makeQuery(id+"F2.imprint","IMPRINT",EDGE,{"derivedFrom":sQuery(id+"F2.wireOp",EDGE,"E1154")}),1.0]])]});
            var Q20;
            Q20=makeQuery(id+"F2.imprint","IMPRINT",FACE,{"disambiguationData":[TD([[makeQuery(id+"F2.imprint","IMPRINT",EDGE,{"derivedFrom":sQuery(id+"F2.wireOp",EDGE,"E890")}),1.0]])]});
            var Q21;
            Q21=makeQuery(id+"F2.imprint","IMPRINT",FACE,{"disambiguationData":[TD([[makeQuery(id+"F2.imprint","IMPRINT",EDGE,{"derivedFrom":sQuery(id+"F2.wireOp",EDGE,"E1177")}),-1.0]])]});
            var Q22;
            Q22=makeQuery(id+"F2.imprint","IMPRINT",FACE,{"disambiguationData":[TD([[makeQuery(id+"F2.imprint","IMPRINT",EDGE,{"derivedFrom":sQuery(id+"F2.wireOp",EDGE,"E1167")}),-1.0]])]});
            var Q23;
            Q23=makeQuery(id+"F2.imprint","IMPRINT",FACE,{"disambiguationData":[TD([[makeQuery(id+"F2.imprint","IMPRINT",EDGE,{"derivedFrom":sQuery(id+"F2.wireOp",EDGE,"E1164")}),1.0]])]});
            var Q24;
            Q24=makeQuery(id+"F2.imprint","IMPRINT",FACE,{"disambiguationData":[TD([[makeQuery(id+"F2.imprint","IMPRINT",EDGE,{"derivedFrom":sQuery(id+"F2.wireOp",EDGE,"E1166.bottom")}),1.0]])]});
            var Q25;
            Q25=makeQuery(id+"F2.imprint","IMPRINT",FACE,{"disambiguationData":[TD([[makeQuery(id+"F2.imprint","IMPRINT",EDGE,{"derivedFrom":sQuery(id+"F2.wireOp",EDGE,"E1162")}),1.0]])]});
            var Q26;
            Q26=makeQuery(id+"F2.imprint","IMPRINT",FACE,{"disambiguationData":[TD([[makeQuery(id+"F2.imprint","IMPRINT",EDGE,{"derivedFrom":sQuery(id+"F2.wireOp",EDGE,"E952.top")}),1.0]])]});
            var Q27;
            Q27=makeQuery(id+"F2.imprint","IMPRINT",FACE,{"disambiguationData":[TD([[makeQuery(id+"F2.imprint","IMPRINT",EDGE,{"derivedFrom":sQuery(id+"F2.wireOp",EDGE,"E1124")}),-1.0]])]});
            var Q28;
            Q28=makeQuery(id+"F2.imprint","IMPRINT",FACE,{"disambiguationData":[TD([[makeQuery(id+"F2.imprint","IMPRINT",EDGE,{"derivedFrom":sQuery(id+"F2.wireOp",EDGE,"E1145")}),-1.0]])]});
            var Q29;
            Q29=makeQuery(id+"F2.imprint","IMPRINT",FACE,{"disambiguationData":[TD([[makeQuery(id+"F2.imprint","IMPRINT",EDGE,{"derivedFrom":sQuery(id+"F2.wireOp",EDGE,"E1223.top")}),1.0]])]});
            var Q30;
            Q30=makeQuery(id+"F2.imprint","IMPRINT",FACE,{"disambiguationData":[TD([[makeQuery(id+"F2.imprint","IMPRINT",EDGE,{"derivedFrom":sQuery(id+"F2.wireOp",EDGE,"E1225.bottom")}),-1.0]])]});
            var Q31;
            Q31=makeQuery(id+"F2.imprint","IMPRINT",FACE,{"disambiguationData":[TD([[makeQuery(id+"F2.imprint","IMPRINT",EDGE,{"derivedFrom":sQuery(id+"F2.wireOp",EDGE,"E1226")}),-1.0]])]});
            var Q32;
            Q32=makeQuery(id+"F2.imprint","IMPRINT",FACE,{"disambiguationData":[TD([[makeQuery(id+"F2.imprint","IMPRINT",EDGE,{"derivedFrom":sQuery(id+"F2.wireOp",EDGE,"E1251.bottom")}),1.0]])]});
            var Q33;
            Q33=makeQuery(id+"F2.imprint","IMPRINT",FACE,{"disambiguationData":[TD([[makeQuery(id+"F2.imprint","IMPRINT",EDGE,{"derivedFrom":sQuery(id+"F2.wireOp",EDGE,"E607")}),-1.0]])]});
            var Q34;
            Q34=makeQuery(id+"F2.imprint","IMPRINT",FACE,{"disambiguationData":[TD([[makeQuery(id+"F2.imprint","IMPRINT",EDGE,{"derivedFrom":sQuery(id+"F2.wireOp",EDGE,"6f6eea80-531d-413f-83e2-d218fd4cdfc1.bottom")}),-1.0]])]});
            var Q35;
            Q35=makeQuery(id+"F2.imprint","IMPRINT",FACE,{"disambiguationData":[TD([[makeQuery(id+"F2.imprint","IMPRINT",EDGE,{"derivedFrom":sQuery(id+"F2.wireOp",EDGE,"b7e1cb25-9bb9-44e2-b99a-fb5c20a56b0c.bottom")}),-1.0]])]});
            var Q36;
            Q36=makeQuery(id+"F2.imprint","IMPRINT",FACE,{"disambiguationData":[TD([[makeQuery(id+"F2.imprint","IMPRINT",EDGE,{"derivedFrom":sQuery(id+"F2.wireOp",EDGE,"ce22afcd-61db-4a55-a298-b4625a8987c8")}),1.0]])]});
            var Q37;
            Q37=makeQuery(id+"F2.imprint","IMPRINT",FACE,{"disambiguationData":[TD([[makeQuery(id+"F2.imprint","IMPRINT",EDGE,{"derivedFrom":sQuery(id+"F2.wireOp",EDGE,"780705e2-dc3a-4fd6-9091-f85142a16bed.bottom")}),1.0]])]});
            var Q38;
            Q38=makeQuery(id+"F2.imprint","IMPRINT",FACE,{"disambiguationData":[TD([[makeQuery(id+"F2.imprint","IMPRINT",EDGE,{"derivedFrom":sQuery(id+"F2.wireOp",EDGE,"c1c82c28-52c2-4fab-9710-17f7591158fe")}),1.0]])]});
            var Q39;
            Q39=makeQuery(id+"F2.imprint","IMPRINT",FACE,{"disambiguationData":[TD([[makeQuery(id+"F2.imprint","IMPRINT",EDGE,{"derivedFrom":sQuery(id+"F2.wireOp",EDGE,"e8153c08-a27a-4b41-8524-6b09fd277459")}),1.0]])]});
            var Q40;
            Q40=makeQuery(id+"F2.imprint","IMPRINT",FACE,{"disambiguationData":[TD([[makeQuery(id+"F2.imprint","IMPRINT",EDGE,{"derivedFrom":sQuery(id+"F2.wireOp",EDGE,"E745")}),-1.0]])]});
            var Q41;
            Q41=makeQuery(id+"F2.imprint","IMPRINT",FACE,{"disambiguationData":[TD([[makeQuery(id+"F2.imprint","IMPRINT",EDGE,{"derivedFrom":sQuery(id+"F2.wireOp",EDGE,"E1255")}),1.0]])]});
            var Q42;
            Q42=makeQuery(id+"F2.imprint","IMPRINT",FACE,{"disambiguationData":[TD([[makeQuery(id+"F2.imprint","IMPRINT",EDGE,{"derivedFrom":sQuery(id+"F2.wireOp",EDGE,"E1279.bottom")}),1.0]])]});
            var Q43;
            Q43=makeQuery(id+"F2.imprint","IMPRINT",FACE,{"disambiguationData":[TD([[makeQuery(id+"F2.imprint","IMPRINT",EDGE,{"derivedFrom":sQuery(id+"F2.wireOp",EDGE,"E1280.bottom")}),1.0]])]});
            var Q44;
            Q44=makeQuery(id+"F2.imprint","IMPRINT",FACE,{"disambiguationData":[TD([[makeQuery(id+"F2.imprint","IMPRINT",EDGE,{"derivedFrom":sQuery(id+"F2.wireOp",EDGE,"E1282")}),1.0]])]});
            var Q45;
            Q45=makeQuery(id+"F2.imprint","IMPRINT",FACE,{"disambiguationData":[TD([[makeQuery(id+"F2.imprint","IMPRINT",EDGE,{"derivedFrom":sQuery(id+"F2.wireOp",EDGE,"E1281.bottom")}),1.0]])]});
            var Q46;
            Q46=makeQuery(id+"F2.imprint","IMPRINT",FACE,{"disambiguationData":[TD([[makeQuery(id+"F2.imprint","IMPRINT",EDGE,{"derivedFrom":sQuery(id+"F2.wireOp",EDGE,"E639")}),-1.0]])]});
            var Q47;
            Q47=makeQuery(id+"F2.imprint","IMPRINT",FACE,{"disambiguationData":[TD([[makeQuery(id+"F2.imprint","IMPRINT",EDGE,{"derivedFrom":sQuery(id+"F2.wireOp",EDGE,"E1286")}),1.0]])]});
            extrude(context, id + "F3", {"entities" : qUnion([Q0, Q1, Q2, Q3, Q4, Q5, Q6, Q7, Q8, Q9, Q10, Q11, Q12, Q13, Q14, Q15, Q16, Q17, Q18, Q19, Q20, Q21, Q22, Q23, Q24, Q25, Q26, Q27, Q28, Q29, Q30, Q31, Q32, Q33, Q34, Q35, Q36, Q37, Q38, Q39, Q40, Q41, Q42, Q43, Q44, Q45, Q46, Q47]), "depth" : 12.7 * mm, "hasSecondDirection" : true, "secondDirectionOppositeDirection" : true, "secondDirectionDepth" : 12.7 * mm});
        }
        {
            var Q0;
            Q0=makeQuery(id+"F3.opExtrude","SWEPT_EDGE",EDGE,{"disambiguationData":[OSD([sQuery(id+"F2.wireOp",EDGE,"E612"),sQuery(id+"F2.wireOp",EDGE,"E613")])]});
            var Q1;
            Q1=makeQuery(id+"F3.opExtrude","SWEPT_EDGE",EDGE,{"disambiguationData":[OSD([sQuery(id+"F2.wireOp",EDGE,"E611"),sQuery(id+"F2.wireOp",EDGE,"E612")])]});
            var Q2;
            Q2=makeQuery(id+"F3.opExtrude","SWEPT_EDGE",EDGE,{"disambiguationData":[OSD([sQuery(id+"F2.wireOp",EDGE,"E610"),sQuery(id+"F2.wireOp",EDGE,"E611")])]});
            var Q3;
            Q3=makeQuery(id+"F3.opExtrude","SWEPT_EDGE",EDGE,{"disambiguationData":[OSD([sQuery(id+"F2.wireOp",EDGE,"E609"),sQuery(id+"F2.wireOp",EDGE,"E610")])]});
            var Q4;
            Q4=makeQuery(id+"F3.opExtrude","SWEPT_EDGE",EDGE,{"disambiguationData":[OSD([sQuery(id+"F2.wireOp",EDGE,"E608"),sQuery(id+"F2.wireOp",EDGE,"E609")])]});
            var Q5;
            Q5=makeQuery(id+"F3.opExtrude","SWEPT_EDGE",EDGE,{"disambiguationData":[OSD([sQuery(id+"F2.wireOp",EDGE,"E607"),sQuery(id+"F2.wireOp",EDGE,"E608")])]});
            var Q6;
            Q6=makeQuery(id+"F1.opExtrude","SWEPT_EDGE",EDGE,{"disambiguationData":[OSD([sQuery(id+"F0.wireOp",EDGE,"E167"),sQuery(id+"F0.wireOp",EDGE,"E168")])]});
            var Q7;
            Q7=makeQuery(id+"F1.opExtrude","SWEPT_EDGE",EDGE,{"disambiguationData":[OSD([sQuery(id+"F0.wireOp",EDGE,"E166"),sQuery(id+"F0.wireOp",EDGE,"E167")])]});
            var Q8;
            Q8=makeQuery(id+"F1.opExtrude","SWEPT_EDGE",EDGE,{"disambiguationData":[OSD([sQuery(id+"F0.wireOp",EDGE,"E165"),sQuery(id+"F0.wireOp",EDGE,"E166")])]});
            var Q9;
            Q9=makeQuery(id+"F1.opExtrude","SWEPT_EDGE",EDGE,{"disambiguationData":[OSD([sQuery(id+"F0.wireOp",EDGE,"E164"),sQuery(id+"F0.wireOp",EDGE,"E165")])]});
            var Q10;
            Q10=makeQuery(id+"F1.opExtrude","SWEPT_EDGE",EDGE,{"disambiguationData":[OSD([sQuery(id+"F0.wireOp",EDGE,"E163"),sQuery(id+"F0.wireOp",EDGE,"E164")])]});
            var Q11;
            Q11=makeQuery(id+"F1.opExtrude","SWEPT_EDGE",EDGE,{"disambiguationData":[OSD([sQuery(id+"F0.wireOp",EDGE,"E162"),sQuery(id+"F0.wireOp",EDGE,"E163")])]});
            fillet(context, id + "F4", {"entities" : qUnion([Q0, Q1, Q2, Q3, Q4, Q5, Q6, Q7, Q8, Q9, Q10, Q11]), "radius" : 3.52 * mm, "tangentPropagation" : true, "allowEdgeOverflow" : false});
        }
    });
